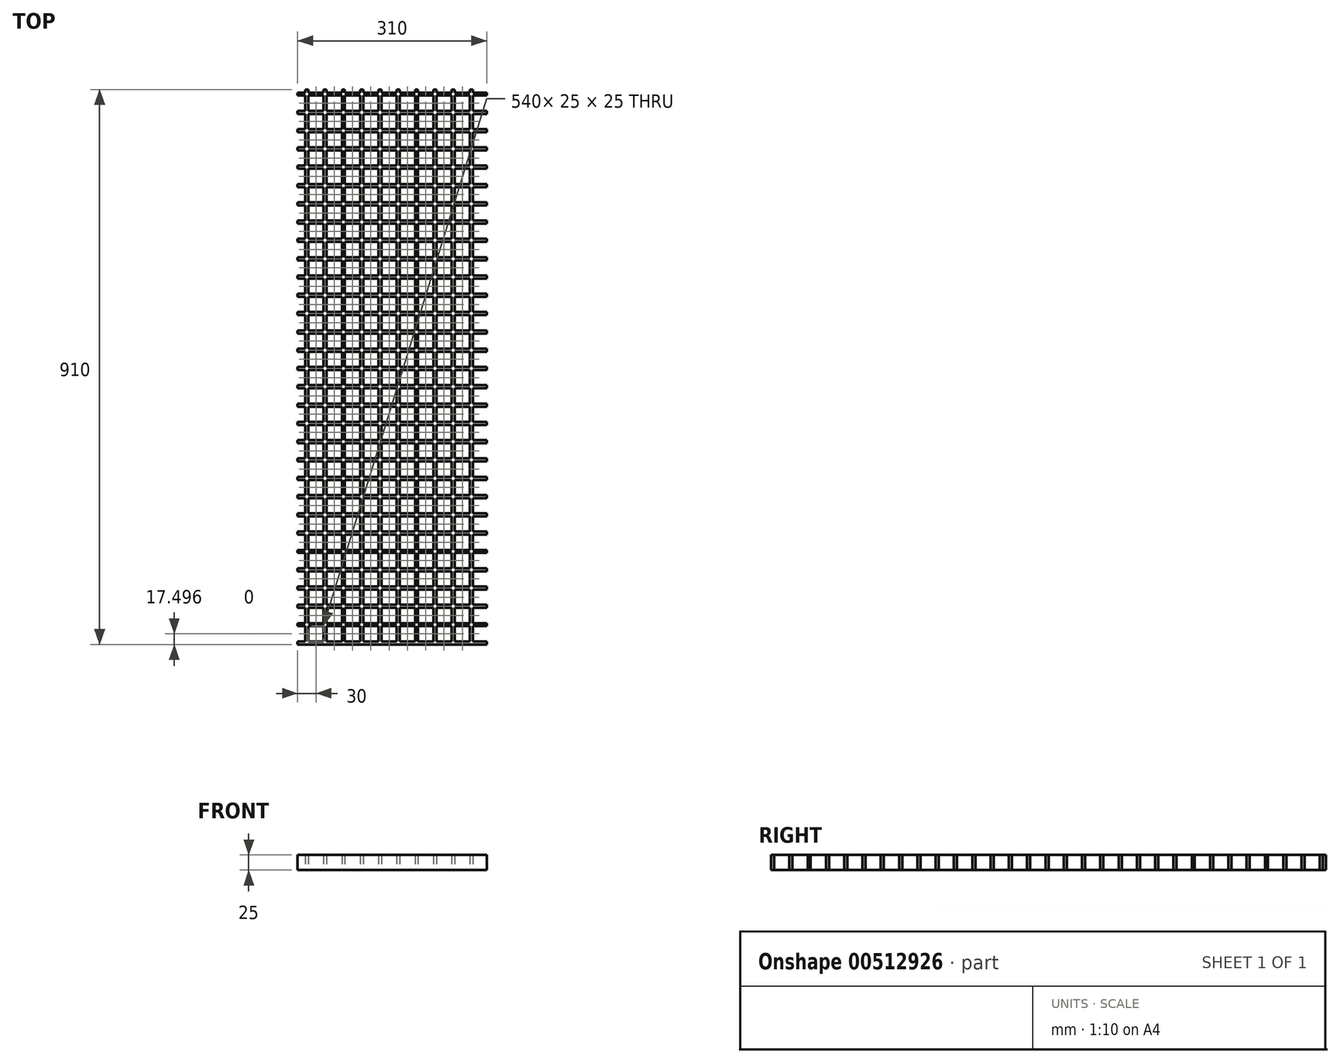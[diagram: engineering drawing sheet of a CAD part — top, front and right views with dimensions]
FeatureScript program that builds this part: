
annotation { "Feature Type Name" : "Feature", "Feature Type Description" : "" }
export const myFeature = defineFeature(function(context is Context, id is Id, definition is map)
    precondition{}
    {
        {
            var Q0;
            Q0=qCreatedBy(makeId("Top.planeOp"),FACE);
            var sketch = newSketch(context, id + "F0", { "sketchPlane" : qUnion([Q0])});
            skLineSegment(sketch, "E0.bottom", {"start": v(0, 20.3) * mm, "end": v(310, 20.3) * mm});
            skLineSegment(sketch, "E0.top", {"start": v(0, 930.3) * mm, "end": v(310, 930.3) * mm});
            skLineSegment(sketch, "E0.left", {"start": v(0, 20.3) * mm, "end": v(0, 930.3) * mm});
            skLineSegment(sketch, "E0.right", {"start": v(310, 20.3) * mm, "end": v(310, 930.3) * mm});
            skLineSegment(sketch, "E1.bottom", {"start": v(12.5, 25.3) * mm, "end": v(-12.5, 25.3) * mm});
            skLineSegment(sketch, "E1.top", {"start": v(12.5, 50.3) * mm, "end": v(-12.5, 50.3) * mm});
            skLineSegment(sketch, "E1.left", {"start": v(12.5, 25.3) * mm, "end": v(12.5, 50.3) * mm});
            skLineSegment(sketch, "E1.right", {"start": v(-12.5, 25.3) * mm, "end": v(-12.5, 50.3) * mm});
            skPoint(sketch, "E1.middle", {"position": v(0, 37.8) * mm});
            skLineSegment(sketch, "E2.0.1.0", {"start": v(12.5, 80.3) * mm, "end": v(-12.5, 80.3) * mm});
            skLineSegment(sketch, "E2.0.1.1", {"start": v(12.5, 55.3) * mm, "end": v(12.5, 80.3) * mm});
            skLineSegment(sketch, "E2.0.1.2", {"start": v(12.5, 55.3) * mm, "end": v(-12.5, 55.3) * mm});
            skLineSegment(sketch, "E2.0.1.3", {"start": v(-12.5, 55.3) * mm, "end": v(-12.5, 80.3) * mm});
            skLineSegment(sketch, "E2.0.2.0", {"start": v(12.5, 110.3) * mm, "end": v(-12.5, 110.3) * mm});
            skLineSegment(sketch, "E2.0.2.1", {"start": v(12.5, 85.3) * mm, "end": v(12.5, 110.3) * mm});
            skLineSegment(sketch, "E2.0.2.2", {"start": v(12.5, 85.3) * mm, "end": v(-12.5, 85.3) * mm});
            skLineSegment(sketch, "E2.0.2.3", {"start": v(-12.5, 85.3) * mm, "end": v(-12.5, 110.3) * mm});
            skLineSegment(sketch, "E2.0.3.0", {"start": v(12.5, 140.3) * mm, "end": v(-12.5, 140.3) * mm});
            skLineSegment(sketch, "E2.0.3.1", {"start": v(12.5, 115.3) * mm, "end": v(12.5, 140.3) * mm});
            skLineSegment(sketch, "E2.0.3.2", {"start": v(12.5, 115.3) * mm, "end": v(-12.5, 115.3) * mm});
            skLineSegment(sketch, "E2.0.3.3", {"start": v(-12.5, 115.3) * mm, "end": v(-12.5, 140.3) * mm});
            skLineSegment(sketch, "E2.0.4.0", {"start": v(12.5, 170.3) * mm, "end": v(-12.5, 170.3) * mm});
            skLineSegment(sketch, "E2.0.4.1", {"start": v(12.5, 145.3) * mm, "end": v(12.5, 170.3) * mm});
            skLineSegment(sketch, "E2.0.4.2", {"start": v(12.5, 145.3) * mm, "end": v(-12.5, 145.3) * mm});
            skLineSegment(sketch, "E2.0.4.3", {"start": v(-12.5, 145.3) * mm, "end": v(-12.5, 170.3) * mm});
            skLineSegment(sketch, "E2.0.5.0", {"start": v(12.5, 200.3) * mm, "end": v(-12.5, 200.3) * mm});
            skLineSegment(sketch, "E2.0.5.1", {"start": v(12.5, 175.3) * mm, "end": v(12.5, 200.3) * mm});
            skLineSegment(sketch, "E2.0.5.2", {"start": v(12.5, 175.3) * mm, "end": v(-12.5, 175.3) * mm});
            skLineSegment(sketch, "E2.0.5.3", {"start": v(-12.5, 175.3) * mm, "end": v(-12.5, 200.3) * mm});
            skLineSegment(sketch, "E2.0.6.0", {"start": v(12.5, 230.3) * mm, "end": v(-12.5, 230.3) * mm});
            skLineSegment(sketch, "E2.0.6.1", {"start": v(12.5, 205.3) * mm, "end": v(12.5, 230.3) * mm});
            skLineSegment(sketch, "E2.0.6.2", {"start": v(12.5, 205.3) * mm, "end": v(-12.5, 205.3) * mm});
            skLineSegment(sketch, "E2.0.6.3", {"start": v(-12.5, 205.3) * mm, "end": v(-12.5, 230.3) * mm});
            skLineSegment(sketch, "E2.0.7.0", {"start": v(12.5, 260.3) * mm, "end": v(-12.5, 260.3) * mm});
            skLineSegment(sketch, "E2.0.7.1", {"start": v(12.5, 235.3) * mm, "end": v(12.5, 260.3) * mm});
            skLineSegment(sketch, "E2.0.7.2", {"start": v(12.5, 235.3) * mm, "end": v(-12.5, 235.3) * mm});
            skLineSegment(sketch, "E2.0.7.3", {"start": v(-12.5, 235.3) * mm, "end": v(-12.5, 260.3) * mm});
            skLineSegment(sketch, "E2.0.8.0", {"start": v(12.5, 290.3) * mm, "end": v(-12.5, 290.3) * mm});
            skLineSegment(sketch, "E2.0.8.1", {"start": v(12.5, 265.3) * mm, "end": v(12.5, 290.3) * mm});
            skLineSegment(sketch, "E2.0.8.2", {"start": v(12.5, 265.3) * mm, "end": v(-12.5, 265.3) * mm});
            skLineSegment(sketch, "E2.0.8.3", {"start": v(-12.5, 265.3) * mm, "end": v(-12.5, 290.3) * mm});
            skLineSegment(sketch, "E2.0.9.0", {"start": v(12.5, 320.3) * mm, "end": v(-12.5, 320.3) * mm});
            skLineSegment(sketch, "E2.0.9.1", {"start": v(12.5, 295.3) * mm, "end": v(12.5, 320.3) * mm});
            skLineSegment(sketch, "E2.0.9.2", {"start": v(12.5, 295.3) * mm, "end": v(-12.5, 295.3) * mm});
            skLineSegment(sketch, "E2.0.9.3", {"start": v(-12.5, 295.3) * mm, "end": v(-12.5, 320.3) * mm});
            skLineSegment(sketch, "E2.0.10.0", {"start": v(12.5, 350.3) * mm, "end": v(-12.5, 350.3) * mm});
            skLineSegment(sketch, "E2.0.10.1", {"start": v(12.5, 325.3) * mm, "end": v(12.5, 350.3) * mm});
            skLineSegment(sketch, "E2.0.10.2", {"start": v(12.5, 325.3) * mm, "end": v(-12.5, 325.3) * mm});
            skLineSegment(sketch, "E2.0.10.3", {"start": v(-12.5, 325.3) * mm, "end": v(-12.5, 350.3) * mm});
            skLineSegment(sketch, "E2.0.11.0", {"start": v(12.5, 380.3) * mm, "end": v(-12.5, 380.3) * mm});
            skLineSegment(sketch, "E2.0.11.1", {"start": v(12.5, 355.3) * mm, "end": v(12.5, 380.3) * mm});
            skLineSegment(sketch, "E2.0.11.2", {"start": v(12.5, 355.3) * mm, "end": v(-12.5, 355.3) * mm});
            skLineSegment(sketch, "E2.0.11.3", {"start": v(-12.5, 355.3) * mm, "end": v(-12.5, 380.3) * mm});
            skLineSegment(sketch, "E2.0.12.0", {"start": v(12.5, 410.3) * mm, "end": v(-12.5, 410.3) * mm});
            skLineSegment(sketch, "E2.0.12.1", {"start": v(12.5, 385.3) * mm, "end": v(12.5, 410.3) * mm});
            skLineSegment(sketch, "E2.0.12.2", {"start": v(12.5, 385.3) * mm, "end": v(-12.5, 385.3) * mm});
            skLineSegment(sketch, "E2.0.12.3", {"start": v(-12.5, 385.3) * mm, "end": v(-12.5, 410.3) * mm});
            skLineSegment(sketch, "E2.0.13.0", {"start": v(12.5, 440.3) * mm, "end": v(-12.5, 440.3) * mm});
            skLineSegment(sketch, "E2.0.13.1", {"start": v(12.5, 415.3) * mm, "end": v(12.5, 440.3) * mm});
            skLineSegment(sketch, "E2.0.13.2", {"start": v(12.5, 415.3) * mm, "end": v(-12.5, 415.3) * mm});
            skLineSegment(sketch, "E2.0.13.3", {"start": v(-12.5, 415.3) * mm, "end": v(-12.5, 440.3) * mm});
            skLineSegment(sketch, "E2.0.14.0", {"start": v(12.5, 470.3) * mm, "end": v(-12.5, 470.3) * mm});
            skLineSegment(sketch, "E2.0.14.1", {"start": v(12.5, 445.3) * mm, "end": v(12.5, 470.3) * mm});
            skLineSegment(sketch, "E2.0.14.2", {"start": v(12.5, 445.3) * mm, "end": v(-12.5, 445.3) * mm});
            skLineSegment(sketch, "E2.0.14.3", {"start": v(-12.5, 445.3) * mm, "end": v(-12.5, 470.3) * mm});
            skLineSegment(sketch, "E2.0.15.0", {"start": v(12.5, 500.3) * mm, "end": v(-12.5, 500.3) * mm});
            skLineSegment(sketch, "E2.0.15.1", {"start": v(12.5, 475.3) * mm, "end": v(12.5, 500.3) * mm});
            skLineSegment(sketch, "E2.0.15.2", {"start": v(12.5, 475.3) * mm, "end": v(-12.5, 475.3) * mm});
            skLineSegment(sketch, "E2.0.15.3", {"start": v(-12.5, 475.3) * mm, "end": v(-12.5, 500.3) * mm});
            skLineSegment(sketch, "E2.0.16.0", {"start": v(12.5, 530.3) * mm, "end": v(-12.5, 530.3) * mm});
            skLineSegment(sketch, "E2.0.16.1", {"start": v(12.5, 505.3) * mm, "end": v(12.5, 530.3) * mm});
            skLineSegment(sketch, "E2.0.16.2", {"start": v(12.5, 505.3) * mm, "end": v(-12.5, 505.3) * mm});
            skLineSegment(sketch, "E2.0.16.3", {"start": v(-12.5, 505.3) * mm, "end": v(-12.5, 530.3) * mm});
            skLineSegment(sketch, "E2.0.17.0", {"start": v(12.5, 560.3) * mm, "end": v(-12.5, 560.3) * mm});
            skLineSegment(sketch, "E2.0.17.1", {"start": v(12.5, 535.3) * mm, "end": v(12.5, 560.3) * mm});
            skLineSegment(sketch, "E2.0.17.2", {"start": v(12.5, 535.3) * mm, "end": v(-12.5, 535.3) * mm});
            skLineSegment(sketch, "E2.0.17.3", {"start": v(-12.5, 535.3) * mm, "end": v(-12.5, 560.3) * mm});
            skLineSegment(sketch, "E2.0.18.0", {"start": v(12.5, 590.3) * mm, "end": v(-12.5, 590.3) * mm});
            skLineSegment(sketch, "E2.0.18.1", {"start": v(12.5, 565.3) * mm, "end": v(12.5, 590.3) * mm});
            skLineSegment(sketch, "E2.0.18.2", {"start": v(12.5, 565.3) * mm, "end": v(-12.5, 565.3) * mm});
            skLineSegment(sketch, "E2.0.18.3", {"start": v(-12.5, 565.3) * mm, "end": v(-12.5, 590.3) * mm});
            skLineSegment(sketch, "E2.0.19.0", {"start": v(12.5, 620.3) * mm, "end": v(-12.5, 620.3) * mm});
            skLineSegment(sketch, "E2.0.19.1", {"start": v(12.5, 595.3) * mm, "end": v(12.5, 620.3) * mm});
            skLineSegment(sketch, "E2.0.19.2", {"start": v(12.5, 595.3) * mm, "end": v(-12.5, 595.3) * mm});
            skLineSegment(sketch, "E2.0.19.3", {"start": v(-12.5, 595.3) * mm, "end": v(-12.5, 620.3) * mm});
            skLineSegment(sketch, "E2.0.20.0", {"start": v(12.5, 650.3) * mm, "end": v(-12.5, 650.3) * mm});
            skLineSegment(sketch, "E2.0.20.1", {"start": v(12.5, 625.3) * mm, "end": v(12.5, 650.3) * mm});
            skLineSegment(sketch, "E2.0.20.2", {"start": v(12.5, 625.3) * mm, "end": v(-12.5, 625.3) * mm});
            skLineSegment(sketch, "E2.0.20.3", {"start": v(-12.5, 625.3) * mm, "end": v(-12.5, 650.3) * mm});
            skLineSegment(sketch, "E2.0.21.0", {"start": v(12.5, 680.3) * mm, "end": v(-12.5, 680.3) * mm});
            skLineSegment(sketch, "E2.0.21.1", {"start": v(12.5, 655.3) * mm, "end": v(12.5, 680.3) * mm});
            skLineSegment(sketch, "E2.0.21.2", {"start": v(12.5, 655.3) * mm, "end": v(-12.5, 655.3) * mm});
            skLineSegment(sketch, "E2.0.21.3", {"start": v(-12.5, 655.3) * mm, "end": v(-12.5, 680.3) * mm});
            skLineSegment(sketch, "E2.0.22.0", {"start": v(12.5, 710.3) * mm, "end": v(-12.5, 710.3) * mm});
            skLineSegment(sketch, "E2.0.22.1", {"start": v(12.5, 685.3) * mm, "end": v(12.5, 710.3) * mm});
            skLineSegment(sketch, "E2.0.22.2", {"start": v(12.5, 685.3) * mm, "end": v(-12.5, 685.3) * mm});
            skLineSegment(sketch, "E2.0.22.3", {"start": v(-12.5, 685.3) * mm, "end": v(-12.5, 710.3) * mm});
            skLineSegment(sketch, "E2.0.23.0", {"start": v(12.5, 740.3) * mm, "end": v(-12.5, 740.3) * mm});
            skLineSegment(sketch, "E2.0.23.1", {"start": v(12.5, 715.3) * mm, "end": v(12.5, 740.3) * mm});
            skLineSegment(sketch, "E2.0.23.2", {"start": v(12.5, 715.3) * mm, "end": v(-12.5, 715.3) * mm});
            skLineSegment(sketch, "E2.0.23.3", {"start": v(-12.5, 715.3) * mm, "end": v(-12.5, 740.3) * mm});
            skLineSegment(sketch, "E2.0.24.0", {"start": v(12.5, 770.3) * mm, "end": v(-12.5, 770.3) * mm});
            skLineSegment(sketch, "E2.0.24.1", {"start": v(12.5, 745.3) * mm, "end": v(12.5, 770.3) * mm});
            skLineSegment(sketch, "E2.0.24.2", {"start": v(12.5, 745.3) * mm, "end": v(-12.5, 745.3) * mm});
            skLineSegment(sketch, "E2.0.24.3", {"start": v(-12.5, 745.3) * mm, "end": v(-12.5, 770.3) * mm});
            skLineSegment(sketch, "E2.0.25.0", {"start": v(12.5, 800.3) * mm, "end": v(-12.5, 800.3) * mm});
            skLineSegment(sketch, "E2.0.25.1", {"start": v(12.5, 775.3) * mm, "end": v(12.5, 800.3) * mm});
            skLineSegment(sketch, "E2.0.25.2", {"start": v(12.5, 775.3) * mm, "end": v(-12.5, 775.3) * mm});
            skLineSegment(sketch, "E2.0.25.3", {"start": v(-12.5, 775.3) * mm, "end": v(-12.5, 800.3) * mm});
            skLineSegment(sketch, "E2.0.26.0", {"start": v(12.5, 830.3) * mm, "end": v(-12.5, 830.3) * mm});
            skLineSegment(sketch, "E2.0.26.1", {"start": v(12.5, 805.3) * mm, "end": v(12.5, 830.3) * mm});
            skLineSegment(sketch, "E2.0.26.2", {"start": v(12.5, 805.3) * mm, "end": v(-12.5, 805.3) * mm});
            skLineSegment(sketch, "E2.0.26.3", {"start": v(-12.5, 805.3) * mm, "end": v(-12.5, 830.3) * mm});
            skLineSegment(sketch, "E2.0.27.0", {"start": v(12.5, 860.3) * mm, "end": v(-12.5, 860.3) * mm});
            skLineSegment(sketch, "E2.0.27.1", {"start": v(12.5, 835.3) * mm, "end": v(12.5, 860.3) * mm});
            skLineSegment(sketch, "E2.0.27.2", {"start": v(12.5, 835.3) * mm, "end": v(-12.5, 835.3) * mm});
            skLineSegment(sketch, "E2.0.27.3", {"start": v(-12.5, 835.3) * mm, "end": v(-12.5, 860.3) * mm});
            skLineSegment(sketch, "E2.0.28.0", {"start": v(12.5, 890.3) * mm, "end": v(-12.5, 890.3) * mm});
            skLineSegment(sketch, "E2.0.28.1", {"start": v(12.5, 865.3) * mm, "end": v(12.5, 890.3) * mm});
            skLineSegment(sketch, "E2.0.28.2", {"start": v(12.5, 865.3) * mm, "end": v(-12.5, 865.3) * mm});
            skLineSegment(sketch, "E2.0.28.3", {"start": v(-12.5, 865.3) * mm, "end": v(-12.5, 890.3) * mm});
            skLineSegment(sketch, "E2.0.29.0", {"start": v(12.5, 920.3) * mm, "end": v(-12.5, 920.3) * mm});
            skLineSegment(sketch, "E2.0.29.1", {"start": v(12.5, 895.3) * mm, "end": v(12.5, 920.3) * mm});
            skLineSegment(sketch, "E2.0.29.2", {"start": v(12.5, 895.3) * mm, "end": v(-12.5, 895.3) * mm});
            skLineSegment(sketch, "E2.0.29.3", {"start": v(-12.5, 895.3) * mm, "end": v(-12.5, 920.3) * mm});
            skLineSegment(sketch, "E2.0.30.0", {"start": v(12.5, 950.3) * mm, "end": v(-12.5, 950.3) * mm});
            skLineSegment(sketch, "E2.0.30.1", {"start": v(12.5, 925.3) * mm, "end": v(12.5, 950.3) * mm});
            skLineSegment(sketch, "E2.0.30.2", {"start": v(12.5, 925.3) * mm, "end": v(-12.5, 925.3) * mm});
            skLineSegment(sketch, "E2.0.30.3", {"start": v(-12.5, 925.3) * mm, "end": v(-12.5, 950.3) * mm});
            skLineSegment(sketch, "E2.1.0.0", {"start": v(42.5, 50.3) * mm, "end": v(17.5, 50.3) * mm});
            skLineSegment(sketch, "E2.1.0.1", {"start": v(42.5, 25.3) * mm, "end": v(42.5, 50.3) * mm});
            skLineSegment(sketch, "E2.1.0.2", {"start": v(42.5, 25.3) * mm, "end": v(17.5, 25.3) * mm});
            skLineSegment(sketch, "E2.1.0.3", {"start": v(17.5, 25.3) * mm, "end": v(17.5, 50.3) * mm});
            skLineSegment(sketch, "E2.1.1.0", {"start": v(42.5, 80.3) * mm, "end": v(17.5, 80.3) * mm});
            skLineSegment(sketch, "E2.1.1.1", {"start": v(42.5, 55.3) * mm, "end": v(42.5, 80.3) * mm});
            skLineSegment(sketch, "E2.1.1.2", {"start": v(42.5, 55.3) * mm, "end": v(17.5, 55.3) * mm});
            skLineSegment(sketch, "E2.1.1.3", {"start": v(17.5, 55.3) * mm, "end": v(17.5, 80.3) * mm});
            skLineSegment(sketch, "E2.1.2.0", {"start": v(42.5, 110.3) * mm, "end": v(17.5, 110.3) * mm});
            skLineSegment(sketch, "E2.1.2.1", {"start": v(42.5, 85.3) * mm, "end": v(42.5, 110.3) * mm});
            skLineSegment(sketch, "E2.1.2.2", {"start": v(42.5, 85.3) * mm, "end": v(17.5, 85.3) * mm});
            skLineSegment(sketch, "E2.1.2.3", {"start": v(17.5, 85.3) * mm, "end": v(17.5, 110.3) * mm});
            skLineSegment(sketch, "E2.1.3.0", {"start": v(42.5, 140.3) * mm, "end": v(17.5, 140.3) * mm});
            skLineSegment(sketch, "E2.1.3.1", {"start": v(42.5, 115.3) * mm, "end": v(42.5, 140.3) * mm});
            skLineSegment(sketch, "E2.1.3.2", {"start": v(42.5, 115.3) * mm, "end": v(17.5, 115.3) * mm});
            skLineSegment(sketch, "E2.1.3.3", {"start": v(17.5, 115.3) * mm, "end": v(17.5, 140.3) * mm});
            skLineSegment(sketch, "E2.1.4.0", {"start": v(42.5, 170.3) * mm, "end": v(17.5, 170.3) * mm});
            skLineSegment(sketch, "E2.1.4.1", {"start": v(42.5, 145.3) * mm, "end": v(42.5, 170.3) * mm});
            skLineSegment(sketch, "E2.1.4.2", {"start": v(42.5, 145.3) * mm, "end": v(17.5, 145.3) * mm});
            skLineSegment(sketch, "E2.1.4.3", {"start": v(17.5, 145.3) * mm, "end": v(17.5, 170.3) * mm});
            skLineSegment(sketch, "E2.1.5.0", {"start": v(42.5, 200.3) * mm, "end": v(17.5, 200.3) * mm});
            skLineSegment(sketch, "E2.1.5.1", {"start": v(42.5, 175.3) * mm, "end": v(42.5, 200.3) * mm});
            skLineSegment(sketch, "E2.1.5.2", {"start": v(42.5, 175.3) * mm, "end": v(17.5, 175.3) * mm});
            skLineSegment(sketch, "E2.1.5.3", {"start": v(17.5, 175.3) * mm, "end": v(17.5, 200.3) * mm});
            skLineSegment(sketch, "E2.1.6.0", {"start": v(42.5, 230.3) * mm, "end": v(17.5, 230.3) * mm});
            skLineSegment(sketch, "E2.1.6.1", {"start": v(42.5, 205.3) * mm, "end": v(42.5, 230.3) * mm});
            skLineSegment(sketch, "E2.1.6.2", {"start": v(42.5, 205.3) * mm, "end": v(17.5, 205.3) * mm});
            skLineSegment(sketch, "E2.1.6.3", {"start": v(17.5, 205.3) * mm, "end": v(17.5, 230.3) * mm});
            skLineSegment(sketch, "E2.1.7.0", {"start": v(42.5, 260.3) * mm, "end": v(17.5, 260.3) * mm});
            skLineSegment(sketch, "E2.1.7.1", {"start": v(42.5, 235.3) * mm, "end": v(42.5, 260.3) * mm});
            skLineSegment(sketch, "E2.1.7.2", {"start": v(42.5, 235.3) * mm, "end": v(17.5, 235.3) * mm});
            skLineSegment(sketch, "E2.1.7.3", {"start": v(17.5, 235.3) * mm, "end": v(17.5, 260.3) * mm});
            skLineSegment(sketch, "E2.1.8.0", {"start": v(42.5, 290.3) * mm, "end": v(17.5, 290.3) * mm});
            skLineSegment(sketch, "E2.1.8.1", {"start": v(42.5, 265.3) * mm, "end": v(42.5, 290.3) * mm});
            skLineSegment(sketch, "E2.1.8.2", {"start": v(42.5, 265.3) * mm, "end": v(17.5, 265.3) * mm});
            skLineSegment(sketch, "E2.1.8.3", {"start": v(17.5, 265.3) * mm, "end": v(17.5, 290.3) * mm});
            skLineSegment(sketch, "E2.1.9.0", {"start": v(42.5, 320.3) * mm, "end": v(17.5, 320.3) * mm});
            skLineSegment(sketch, "E2.1.9.1", {"start": v(42.5, 295.3) * mm, "end": v(42.5, 320.3) * mm});
            skLineSegment(sketch, "E2.1.9.2", {"start": v(42.5, 295.3) * mm, "end": v(17.5, 295.3) * mm});
            skLineSegment(sketch, "E2.1.9.3", {"start": v(17.5, 295.3) * mm, "end": v(17.5, 320.3) * mm});
            skLineSegment(sketch, "E2.1.10.0", {"start": v(42.5, 350.3) * mm, "end": v(17.5, 350.3) * mm});
            skLineSegment(sketch, "E2.1.10.1", {"start": v(42.5, 325.3) * mm, "end": v(42.5, 350.3) * mm});
            skLineSegment(sketch, "E2.1.10.2", {"start": v(42.5, 325.3) * mm, "end": v(17.5, 325.3) * mm});
            skLineSegment(sketch, "E2.1.10.3", {"start": v(17.5, 325.3) * mm, "end": v(17.5, 350.3) * mm});
            skLineSegment(sketch, "E2.1.11.0", {"start": v(42.5, 380.3) * mm, "end": v(17.5, 380.3) * mm});
            skLineSegment(sketch, "E2.1.11.1", {"start": v(42.5, 355.3) * mm, "end": v(42.5, 380.3) * mm});
            skLineSegment(sketch, "E2.1.11.2", {"start": v(42.5, 355.3) * mm, "end": v(17.5, 355.3) * mm});
            skLineSegment(sketch, "E2.1.11.3", {"start": v(17.5, 355.3) * mm, "end": v(17.5, 380.3) * mm});
            skLineSegment(sketch, "E2.1.12.0", {"start": v(42.5, 410.3) * mm, "end": v(17.5, 410.3) * mm});
            skLineSegment(sketch, "E2.1.12.1", {"start": v(42.5, 385.3) * mm, "end": v(42.5, 410.3) * mm});
            skLineSegment(sketch, "E2.1.12.2", {"start": v(42.5, 385.3) * mm, "end": v(17.5, 385.3) * mm});
            skLineSegment(sketch, "E2.1.12.3", {"start": v(17.5, 385.3) * mm, "end": v(17.5, 410.3) * mm});
            skLineSegment(sketch, "E2.1.13.0", {"start": v(42.5, 440.3) * mm, "end": v(17.5, 440.3) * mm});
            skLineSegment(sketch, "E2.1.13.1", {"start": v(42.5, 415.3) * mm, "end": v(42.5, 440.3) * mm});
            skLineSegment(sketch, "E2.1.13.2", {"start": v(42.5, 415.3) * mm, "end": v(17.5, 415.3) * mm});
            skLineSegment(sketch, "E2.1.13.3", {"start": v(17.5, 415.3) * mm, "end": v(17.5, 440.3) * mm});
            skLineSegment(sketch, "E2.1.14.0", {"start": v(42.5, 470.3) * mm, "end": v(17.5, 470.3) * mm});
            skLineSegment(sketch, "E2.1.14.1", {"start": v(42.5, 445.3) * mm, "end": v(42.5, 470.3) * mm});
            skLineSegment(sketch, "E2.1.14.2", {"start": v(42.5, 445.3) * mm, "end": v(17.5, 445.3) * mm});
            skLineSegment(sketch, "E2.1.14.3", {"start": v(17.5, 445.3) * mm, "end": v(17.5, 470.3) * mm});
            skLineSegment(sketch, "E2.1.15.0", {"start": v(42.5, 500.3) * mm, "end": v(17.5, 500.3) * mm});
            skLineSegment(sketch, "E2.1.15.1", {"start": v(42.5, 475.3) * mm, "end": v(42.5, 500.3) * mm});
            skLineSegment(sketch, "E2.1.15.2", {"start": v(42.5, 475.3) * mm, "end": v(17.5, 475.3) * mm});
            skLineSegment(sketch, "E2.1.15.3", {"start": v(17.5, 475.3) * mm, "end": v(17.5, 500.3) * mm});
            skLineSegment(sketch, "E2.1.16.0", {"start": v(42.5, 530.3) * mm, "end": v(17.5, 530.3) * mm});
            skLineSegment(sketch, "E2.1.16.1", {"start": v(42.5, 505.3) * mm, "end": v(42.5, 530.3) * mm});
            skLineSegment(sketch, "E2.1.16.2", {"start": v(42.5, 505.3) * mm, "end": v(17.5, 505.3) * mm});
            skLineSegment(sketch, "E2.1.16.3", {"start": v(17.5, 505.3) * mm, "end": v(17.5, 530.3) * mm});
            skLineSegment(sketch, "E2.1.17.0", {"start": v(42.5, 560.3) * mm, "end": v(17.5, 560.3) * mm});
            skLineSegment(sketch, "E2.1.17.1", {"start": v(42.5, 535.3) * mm, "end": v(42.5, 560.3) * mm});
            skLineSegment(sketch, "E2.1.17.2", {"start": v(42.5, 535.3) * mm, "end": v(17.5, 535.3) * mm});
            skLineSegment(sketch, "E2.1.17.3", {"start": v(17.5, 535.3) * mm, "end": v(17.5, 560.3) * mm});
            skLineSegment(sketch, "E2.1.18.0", {"start": v(42.5, 590.3) * mm, "end": v(17.5, 590.3) * mm});
            skLineSegment(sketch, "E2.1.18.1", {"start": v(42.5, 565.3) * mm, "end": v(42.5, 590.3) * mm});
            skLineSegment(sketch, "E2.1.18.2", {"start": v(42.5, 565.3) * mm, "end": v(17.5, 565.3) * mm});
            skLineSegment(sketch, "E2.1.18.3", {"start": v(17.5, 565.3) * mm, "end": v(17.5, 590.3) * mm});
            skLineSegment(sketch, "E2.1.19.0", {"start": v(42.5, 620.3) * mm, "end": v(17.5, 620.3) * mm});
            skLineSegment(sketch, "E2.1.19.1", {"start": v(42.5, 595.3) * mm, "end": v(42.5, 620.3) * mm});
            skLineSegment(sketch, "E2.1.19.2", {"start": v(42.5, 595.3) * mm, "end": v(17.5, 595.3) * mm});
            skLineSegment(sketch, "E2.1.19.3", {"start": v(17.5, 595.3) * mm, "end": v(17.5, 620.3) * mm});
            skLineSegment(sketch, "E2.1.20.0", {"start": v(42.5, 650.3) * mm, "end": v(17.5, 650.3) * mm});
            skLineSegment(sketch, "E2.1.20.1", {"start": v(42.5, 625.3) * mm, "end": v(42.5, 650.3) * mm});
            skLineSegment(sketch, "E2.1.20.2", {"start": v(42.5, 625.3) * mm, "end": v(17.5, 625.3) * mm});
            skLineSegment(sketch, "E2.1.20.3", {"start": v(17.5, 625.3) * mm, "end": v(17.5, 650.3) * mm});
            skLineSegment(sketch, "E2.1.21.0", {"start": v(42.5, 680.3) * mm, "end": v(17.5, 680.3) * mm});
            skLineSegment(sketch, "E2.1.21.1", {"start": v(42.5, 655.3) * mm, "end": v(42.5, 680.3) * mm});
            skLineSegment(sketch, "E2.1.21.2", {"start": v(42.5, 655.3) * mm, "end": v(17.5, 655.3) * mm});
            skLineSegment(sketch, "E2.1.21.3", {"start": v(17.5, 655.3) * mm, "end": v(17.5, 680.3) * mm});
            skLineSegment(sketch, "E2.1.22.0", {"start": v(42.5, 710.3) * mm, "end": v(17.5, 710.3) * mm});
            skLineSegment(sketch, "E2.1.22.1", {"start": v(42.5, 685.3) * mm, "end": v(42.5, 710.3) * mm});
            skLineSegment(sketch, "E2.1.22.2", {"start": v(42.5, 685.3) * mm, "end": v(17.5, 685.3) * mm});
            skLineSegment(sketch, "E2.1.22.3", {"start": v(17.5, 685.3) * mm, "end": v(17.5, 710.3) * mm});
            skLineSegment(sketch, "E2.1.23.0", {"start": v(42.5, 740.3) * mm, "end": v(17.5, 740.3) * mm});
            skLineSegment(sketch, "E2.1.23.1", {"start": v(42.5, 715.3) * mm, "end": v(42.5, 740.3) * mm});
            skLineSegment(sketch, "E2.1.23.2", {"start": v(42.5, 715.3) * mm, "end": v(17.5, 715.3) * mm});
            skLineSegment(sketch, "E2.1.23.3", {"start": v(17.5, 715.3) * mm, "end": v(17.5, 740.3) * mm});
            skLineSegment(sketch, "E2.1.24.0", {"start": v(42.5, 770.3) * mm, "end": v(17.5, 770.3) * mm});
            skLineSegment(sketch, "E2.1.24.1", {"start": v(42.5, 745.3) * mm, "end": v(42.5, 770.3) * mm});
            skLineSegment(sketch, "E2.1.24.2", {"start": v(42.5, 745.3) * mm, "end": v(17.5, 745.3) * mm});
            skLineSegment(sketch, "E2.1.24.3", {"start": v(17.5, 745.3) * mm, "end": v(17.5, 770.3) * mm});
            skLineSegment(sketch, "E2.1.25.0", {"start": v(42.5, 800.3) * mm, "end": v(17.5, 800.3) * mm});
            skLineSegment(sketch, "E2.1.25.1", {"start": v(42.5, 775.3) * mm, "end": v(42.5, 800.3) * mm});
            skLineSegment(sketch, "E2.1.25.2", {"start": v(42.5, 775.3) * mm, "end": v(17.5, 775.3) * mm});
            skLineSegment(sketch, "E2.1.25.3", {"start": v(17.5, 775.3) * mm, "end": v(17.5, 800.3) * mm});
            skLineSegment(sketch, "E2.1.26.0", {"start": v(42.5, 830.3) * mm, "end": v(17.5, 830.3) * mm});
            skLineSegment(sketch, "E2.1.26.1", {"start": v(42.5, 805.3) * mm, "end": v(42.5, 830.3) * mm});
            skLineSegment(sketch, "E2.1.26.2", {"start": v(42.5, 805.3) * mm, "end": v(17.5, 805.3) * mm});
            skLineSegment(sketch, "E2.1.26.3", {"start": v(17.5, 805.3) * mm, "end": v(17.5, 830.3) * mm});
            skLineSegment(sketch, "E2.1.27.0", {"start": v(42.5, 860.3) * mm, "end": v(17.5, 860.3) * mm});
            skLineSegment(sketch, "E2.1.27.1", {"start": v(42.5, 835.3) * mm, "end": v(42.5, 860.3) * mm});
            skLineSegment(sketch, "E2.1.27.2", {"start": v(42.5, 835.3) * mm, "end": v(17.5, 835.3) * mm});
            skLineSegment(sketch, "E2.1.27.3", {"start": v(17.5, 835.3) * mm, "end": v(17.5, 860.3) * mm});
            skLineSegment(sketch, "E2.1.28.0", {"start": v(42.5, 890.3) * mm, "end": v(17.5, 890.3) * mm});
            skLineSegment(sketch, "E2.1.28.1", {"start": v(42.5, 865.3) * mm, "end": v(42.5, 890.3) * mm});
            skLineSegment(sketch, "E2.1.28.2", {"start": v(42.5, 865.3) * mm, "end": v(17.5, 865.3) * mm});
            skLineSegment(sketch, "E2.1.28.3", {"start": v(17.5, 865.3) * mm, "end": v(17.5, 890.3) * mm});
            skLineSegment(sketch, "E2.1.29.0", {"start": v(42.5, 920.3) * mm, "end": v(17.5, 920.3) * mm});
            skLineSegment(sketch, "E2.1.29.1", {"start": v(42.5, 895.3) * mm, "end": v(42.5, 920.3) * mm});
            skLineSegment(sketch, "E2.1.29.2", {"start": v(42.5, 895.3) * mm, "end": v(17.5, 895.3) * mm});
            skLineSegment(sketch, "E2.1.29.3", {"start": v(17.5, 895.3) * mm, "end": v(17.5, 920.3) * mm});
            skLineSegment(sketch, "E2.1.30.0", {"start": v(42.5, 950.3) * mm, "end": v(17.5, 950.3) * mm});
            skLineSegment(sketch, "E2.1.30.1", {"start": v(42.5, 925.3) * mm, "end": v(42.5, 950.3) * mm});
            skLineSegment(sketch, "E2.1.30.2", {"start": v(42.5, 925.3) * mm, "end": v(17.5, 925.3) * mm});
            skLineSegment(sketch, "E2.1.30.3", {"start": v(17.5, 925.3) * mm, "end": v(17.5, 950.3) * mm});
            skLineSegment(sketch, "E2.2.0.0", {"start": v(72.5, 50.3) * mm, "end": v(47.5, 50.3) * mm});
            skLineSegment(sketch, "E2.2.0.1", {"start": v(72.5, 25.3) * mm, "end": v(72.5, 50.3) * mm});
            skLineSegment(sketch, "E2.2.0.2", {"start": v(72.5, 25.3) * mm, "end": v(47.5, 25.3) * mm});
            skLineSegment(sketch, "E2.2.0.3", {"start": v(47.5, 25.3) * mm, "end": v(47.5, 50.3) * mm});
            skLineSegment(sketch, "E2.2.1.0", {"start": v(72.5, 80.3) * mm, "end": v(47.5, 80.3) * mm});
            skLineSegment(sketch, "E2.2.1.1", {"start": v(72.5, 55.3) * mm, "end": v(72.5, 80.3) * mm});
            skLineSegment(sketch, "E2.2.1.2", {"start": v(72.5, 55.3) * mm, "end": v(47.5, 55.3) * mm});
            skLineSegment(sketch, "E2.2.1.3", {"start": v(47.5, 55.3) * mm, "end": v(47.5, 80.3) * mm});
            skLineSegment(sketch, "E2.2.2.0", {"start": v(72.5, 110.3) * mm, "end": v(47.5, 110.3) * mm});
            skLineSegment(sketch, "E2.2.2.1", {"start": v(72.5, 85.3) * mm, "end": v(72.5, 110.3) * mm});
            skLineSegment(sketch, "E2.2.2.2", {"start": v(72.5, 85.3) * mm, "end": v(47.5, 85.3) * mm});
            skLineSegment(sketch, "E2.2.2.3", {"start": v(47.5, 85.3) * mm, "end": v(47.5, 110.3) * mm});
            skLineSegment(sketch, "E2.2.3.0", {"start": v(72.5, 140.3) * mm, "end": v(47.5, 140.3) * mm});
            skLineSegment(sketch, "E2.2.3.1", {"start": v(72.5, 115.3) * mm, "end": v(72.5, 140.3) * mm});
            skLineSegment(sketch, "E2.2.3.2", {"start": v(72.5, 115.3) * mm, "end": v(47.5, 115.3) * mm});
            skLineSegment(sketch, "E2.2.3.3", {"start": v(47.5, 115.3) * mm, "end": v(47.5, 140.3) * mm});
            skLineSegment(sketch, "E2.2.4.0", {"start": v(72.5, 170.3) * mm, "end": v(47.5, 170.3) * mm});
            skLineSegment(sketch, "E2.2.4.1", {"start": v(72.5, 145.3) * mm, "end": v(72.5, 170.3) * mm});
            skLineSegment(sketch, "E2.2.4.2", {"start": v(72.5, 145.3) * mm, "end": v(47.5, 145.3) * mm});
            skLineSegment(sketch, "E2.2.4.3", {"start": v(47.5, 145.3) * mm, "end": v(47.5, 170.3) * mm});
            skLineSegment(sketch, "E2.2.5.0", {"start": v(72.5, 200.3) * mm, "end": v(47.5, 200.3) * mm});
            skLineSegment(sketch, "E2.2.5.1", {"start": v(72.5, 175.3) * mm, "end": v(72.5, 200.3) * mm});
            skLineSegment(sketch, "E2.2.5.2", {"start": v(72.5, 175.3) * mm, "end": v(47.5, 175.3) * mm});
            skLineSegment(sketch, "E2.2.5.3", {"start": v(47.5, 175.3) * mm, "end": v(47.5, 200.3) * mm});
            skLineSegment(sketch, "E2.2.6.0", {"start": v(72.5, 230.3) * mm, "end": v(47.5, 230.3) * mm});
            skLineSegment(sketch, "E2.2.6.1", {"start": v(72.5, 205.3) * mm, "end": v(72.5, 230.3) * mm});
            skLineSegment(sketch, "E2.2.6.2", {"start": v(72.5, 205.3) * mm, "end": v(47.5, 205.3) * mm});
            skLineSegment(sketch, "E2.2.6.3", {"start": v(47.5, 205.3) * mm, "end": v(47.5, 230.3) * mm});
            skLineSegment(sketch, "E2.2.7.0", {"start": v(72.5, 260.3) * mm, "end": v(47.5, 260.3) * mm});
            skLineSegment(sketch, "E2.2.7.1", {"start": v(72.5, 235.3) * mm, "end": v(72.5, 260.3) * mm});
            skLineSegment(sketch, "E2.2.7.2", {"start": v(72.5, 235.3) * mm, "end": v(47.5, 235.3) * mm});
            skLineSegment(sketch, "E2.2.7.3", {"start": v(47.5, 235.3) * mm, "end": v(47.5, 260.3) * mm});
            skLineSegment(sketch, "E2.2.8.0", {"start": v(72.5, 290.3) * mm, "end": v(47.5, 290.3) * mm});
            skLineSegment(sketch, "E2.2.8.1", {"start": v(72.5, 265.3) * mm, "end": v(72.5, 290.3) * mm});
            skLineSegment(sketch, "E2.2.8.2", {"start": v(72.5, 265.3) * mm, "end": v(47.5, 265.3) * mm});
            skLineSegment(sketch, "E2.2.8.3", {"start": v(47.5, 265.3) * mm, "end": v(47.5, 290.3) * mm});
            skLineSegment(sketch, "E2.2.9.0", {"start": v(72.5, 320.3) * mm, "end": v(47.5, 320.3) * mm});
            skLineSegment(sketch, "E2.2.9.1", {"start": v(72.5, 295.3) * mm, "end": v(72.5, 320.3) * mm});
            skLineSegment(sketch, "E2.2.9.2", {"start": v(72.5, 295.3) * mm, "end": v(47.5, 295.3) * mm});
            skLineSegment(sketch, "E2.2.9.3", {"start": v(47.5, 295.3) * mm, "end": v(47.5, 320.3) * mm});
            skLineSegment(sketch, "E2.2.10.0", {"start": v(72.5, 350.3) * mm, "end": v(47.5, 350.3) * mm});
            skLineSegment(sketch, "E2.2.10.1", {"start": v(72.5, 325.3) * mm, "end": v(72.5, 350.3) * mm});
            skLineSegment(sketch, "E2.2.10.2", {"start": v(72.5, 325.3) * mm, "end": v(47.5, 325.3) * mm});
            skLineSegment(sketch, "E2.2.10.3", {"start": v(47.5, 325.3) * mm, "end": v(47.5, 350.3) * mm});
            skLineSegment(sketch, "E2.2.11.0", {"start": v(72.5, 380.3) * mm, "end": v(47.5, 380.3) * mm});
            skLineSegment(sketch, "E2.2.11.1", {"start": v(72.5, 355.3) * mm, "end": v(72.5, 380.3) * mm});
            skLineSegment(sketch, "E2.2.11.2", {"start": v(72.5, 355.3) * mm, "end": v(47.5, 355.3) * mm});
            skLineSegment(sketch, "E2.2.11.3", {"start": v(47.5, 355.3) * mm, "end": v(47.5, 380.3) * mm});
            skLineSegment(sketch, "E2.2.12.0", {"start": v(72.5, 410.3) * mm, "end": v(47.5, 410.3) * mm});
            skLineSegment(sketch, "E2.2.12.1", {"start": v(72.5, 385.3) * mm, "end": v(72.5, 410.3) * mm});
            skLineSegment(sketch, "E2.2.12.2", {"start": v(72.5, 385.3) * mm, "end": v(47.5, 385.3) * mm});
            skLineSegment(sketch, "E2.2.12.3", {"start": v(47.5, 385.3) * mm, "end": v(47.5, 410.3) * mm});
            skLineSegment(sketch, "E2.2.13.0", {"start": v(72.5, 440.3) * mm, "end": v(47.5, 440.3) * mm});
            skLineSegment(sketch, "E2.2.13.1", {"start": v(72.5, 415.3) * mm, "end": v(72.5, 440.3) * mm});
            skLineSegment(sketch, "E2.2.13.2", {"start": v(72.5, 415.3) * mm, "end": v(47.5, 415.3) * mm});
            skLineSegment(sketch, "E2.2.13.3", {"start": v(47.5, 415.3) * mm, "end": v(47.5, 440.3) * mm});
            skLineSegment(sketch, "E2.2.14.0", {"start": v(72.5, 470.3) * mm, "end": v(47.5, 470.3) * mm});
            skLineSegment(sketch, "E2.2.14.1", {"start": v(72.5, 445.3) * mm, "end": v(72.5, 470.3) * mm});
            skLineSegment(sketch, "E2.2.14.2", {"start": v(72.5, 445.3) * mm, "end": v(47.5, 445.3) * mm});
            skLineSegment(sketch, "E2.2.14.3", {"start": v(47.5, 445.3) * mm, "end": v(47.5, 470.3) * mm});
            skLineSegment(sketch, "E2.2.15.0", {"start": v(72.5, 500.3) * mm, "end": v(47.5, 500.3) * mm});
            skLineSegment(sketch, "E2.2.15.1", {"start": v(72.5, 475.3) * mm, "end": v(72.5, 500.3) * mm});
            skLineSegment(sketch, "E2.2.15.2", {"start": v(72.5, 475.3) * mm, "end": v(47.5, 475.3) * mm});
            skLineSegment(sketch, "E2.2.15.3", {"start": v(47.5, 475.3) * mm, "end": v(47.5, 500.3) * mm});
            skLineSegment(sketch, "E2.2.16.0", {"start": v(72.5, 530.3) * mm, "end": v(47.5, 530.3) * mm});
            skLineSegment(sketch, "E2.2.16.1", {"start": v(72.5, 505.3) * mm, "end": v(72.5, 530.3) * mm});
            skLineSegment(sketch, "E2.2.16.2", {"start": v(72.5, 505.3) * mm, "end": v(47.5, 505.3) * mm});
            skLineSegment(sketch, "E2.2.16.3", {"start": v(47.5, 505.3) * mm, "end": v(47.5, 530.3) * mm});
            skLineSegment(sketch, "E2.2.17.0", {"start": v(72.5, 560.3) * mm, "end": v(47.5, 560.3) * mm});
            skLineSegment(sketch, "E2.2.17.1", {"start": v(72.5, 535.3) * mm, "end": v(72.5, 560.3) * mm});
            skLineSegment(sketch, "E2.2.17.2", {"start": v(72.5, 535.3) * mm, "end": v(47.5, 535.3) * mm});
            skLineSegment(sketch, "E2.2.17.3", {"start": v(47.5, 535.3) * mm, "end": v(47.5, 560.3) * mm});
            skLineSegment(sketch, "E2.2.18.0", {"start": v(72.5, 590.3) * mm, "end": v(47.5, 590.3) * mm});
            skLineSegment(sketch, "E2.2.18.1", {"start": v(72.5, 565.3) * mm, "end": v(72.5, 590.3) * mm});
            skLineSegment(sketch, "E2.2.18.2", {"start": v(72.5, 565.3) * mm, "end": v(47.5, 565.3) * mm});
            skLineSegment(sketch, "E2.2.18.3", {"start": v(47.5, 565.3) * mm, "end": v(47.5, 590.3) * mm});
            skLineSegment(sketch, "E2.2.19.0", {"start": v(72.5, 620.3) * mm, "end": v(47.5, 620.3) * mm});
            skLineSegment(sketch, "E2.2.19.1", {"start": v(72.5, 595.3) * mm, "end": v(72.5, 620.3) * mm});
            skLineSegment(sketch, "E2.2.19.2", {"start": v(72.5, 595.3) * mm, "end": v(47.5, 595.3) * mm});
            skLineSegment(sketch, "E2.2.19.3", {"start": v(47.5, 595.3) * mm, "end": v(47.5, 620.3) * mm});
            skLineSegment(sketch, "E2.2.20.0", {"start": v(72.5, 650.3) * mm, "end": v(47.5, 650.3) * mm});
            skLineSegment(sketch, "E2.2.20.1", {"start": v(72.5, 625.3) * mm, "end": v(72.5, 650.3) * mm});
            skLineSegment(sketch, "E2.2.20.2", {"start": v(72.5, 625.3) * mm, "end": v(47.5, 625.3) * mm});
            skLineSegment(sketch, "E2.2.20.3", {"start": v(47.5, 625.3) * mm, "end": v(47.5, 650.3) * mm});
            skLineSegment(sketch, "E2.2.21.0", {"start": v(72.5, 680.3) * mm, "end": v(47.5, 680.3) * mm});
            skLineSegment(sketch, "E2.2.21.1", {"start": v(72.5, 655.3) * mm, "end": v(72.5, 680.3) * mm});
            skLineSegment(sketch, "E2.2.21.2", {"start": v(72.5, 655.3) * mm, "end": v(47.5, 655.3) * mm});
            skLineSegment(sketch, "E2.2.21.3", {"start": v(47.5, 655.3) * mm, "end": v(47.5, 680.3) * mm});
            skLineSegment(sketch, "E2.2.22.0", {"start": v(72.5, 710.3) * mm, "end": v(47.5, 710.3) * mm});
            skLineSegment(sketch, "E2.2.22.1", {"start": v(72.5, 685.3) * mm, "end": v(72.5, 710.3) * mm});
            skLineSegment(sketch, "E2.2.22.2", {"start": v(72.5, 685.3) * mm, "end": v(47.5, 685.3) * mm});
            skLineSegment(sketch, "E2.2.22.3", {"start": v(47.5, 685.3) * mm, "end": v(47.5, 710.3) * mm});
            skLineSegment(sketch, "E2.2.23.0", {"start": v(72.5, 740.3) * mm, "end": v(47.5, 740.3) * mm});
            skLineSegment(sketch, "E2.2.23.1", {"start": v(72.5, 715.3) * mm, "end": v(72.5, 740.3) * mm});
            skLineSegment(sketch, "E2.2.23.2", {"start": v(72.5, 715.3) * mm, "end": v(47.5, 715.3) * mm});
            skLineSegment(sketch, "E2.2.23.3", {"start": v(47.5, 715.3) * mm, "end": v(47.5, 740.3) * mm});
            skLineSegment(sketch, "E2.2.24.0", {"start": v(72.5, 770.3) * mm, "end": v(47.5, 770.3) * mm});
            skLineSegment(sketch, "E2.2.24.1", {"start": v(72.5, 745.3) * mm, "end": v(72.5, 770.3) * mm});
            skLineSegment(sketch, "E2.2.24.2", {"start": v(72.5, 745.3) * mm, "end": v(47.5, 745.3) * mm});
            skLineSegment(sketch, "E2.2.24.3", {"start": v(47.5, 745.3) * mm, "end": v(47.5, 770.3) * mm});
            skLineSegment(sketch, "E2.2.25.0", {"start": v(72.5, 800.3) * mm, "end": v(47.5, 800.3) * mm});
            skLineSegment(sketch, "E2.2.25.1", {"start": v(72.5, 775.3) * mm, "end": v(72.5, 800.3) * mm});
            skLineSegment(sketch, "E2.2.25.2", {"start": v(72.5, 775.3) * mm, "end": v(47.5, 775.3) * mm});
            skLineSegment(sketch, "E2.2.25.3", {"start": v(47.5, 775.3) * mm, "end": v(47.5, 800.3) * mm});
            skLineSegment(sketch, "E2.2.26.0", {"start": v(72.5, 830.3) * mm, "end": v(47.5, 830.3) * mm});
            skLineSegment(sketch, "E2.2.26.1", {"start": v(72.5, 805.3) * mm, "end": v(72.5, 830.3) * mm});
            skLineSegment(sketch, "E2.2.26.2", {"start": v(72.5, 805.3) * mm, "end": v(47.5, 805.3) * mm});
            skLineSegment(sketch, "E2.2.26.3", {"start": v(47.5, 805.3) * mm, "end": v(47.5, 830.3) * mm});
            skLineSegment(sketch, "E2.2.27.0", {"start": v(72.5, 860.3) * mm, "end": v(47.5, 860.3) * mm});
            skLineSegment(sketch, "E2.2.27.1", {"start": v(72.5, 835.3) * mm, "end": v(72.5, 860.3) * mm});
            skLineSegment(sketch, "E2.2.27.2", {"start": v(72.5, 835.3) * mm, "end": v(47.5, 835.3) * mm});
            skLineSegment(sketch, "E2.2.27.3", {"start": v(47.5, 835.3) * mm, "end": v(47.5, 860.3) * mm});
            skLineSegment(sketch, "E2.2.28.0", {"start": v(72.5, 890.3) * mm, "end": v(47.5, 890.3) * mm});
            skLineSegment(sketch, "E2.2.28.1", {"start": v(72.5, 865.3) * mm, "end": v(72.5, 890.3) * mm});
            skLineSegment(sketch, "E2.2.28.2", {"start": v(72.5, 865.3) * mm, "end": v(47.5, 865.3) * mm});
            skLineSegment(sketch, "E2.2.28.3", {"start": v(47.5, 865.3) * mm, "end": v(47.5, 890.3) * mm});
            skLineSegment(sketch, "E2.2.29.0", {"start": v(72.5, 920.3) * mm, "end": v(47.5, 920.3) * mm});
            skLineSegment(sketch, "E2.2.29.1", {"start": v(72.5, 895.3) * mm, "end": v(72.5, 920.3) * mm});
            skLineSegment(sketch, "E2.2.29.2", {"start": v(72.5, 895.3) * mm, "end": v(47.5, 895.3) * mm});
            skLineSegment(sketch, "E2.2.29.3", {"start": v(47.5, 895.3) * mm, "end": v(47.5, 920.3) * mm});
            skLineSegment(sketch, "E2.2.30.0", {"start": v(72.5, 950.3) * mm, "end": v(47.5, 950.3) * mm});
            skLineSegment(sketch, "E2.2.30.1", {"start": v(72.5, 925.3) * mm, "end": v(72.5, 950.3) * mm});
            skLineSegment(sketch, "E2.2.30.2", {"start": v(72.5, 925.3) * mm, "end": v(47.5, 925.3) * mm});
            skLineSegment(sketch, "E2.2.30.3", {"start": v(47.5, 925.3) * mm, "end": v(47.5, 950.3) * mm});
            skLineSegment(sketch, "E2.3.0.0", {"start": v(102.5, 50.3) * mm, "end": v(77.5, 50.3) * mm});
            skLineSegment(sketch, "E2.3.0.1", {"start": v(102.5, 25.3) * mm, "end": v(102.5, 50.3) * mm});
            skLineSegment(sketch, "E2.3.0.2", {"start": v(102.5, 25.3) * mm, "end": v(77.5, 25.3) * mm});
            skLineSegment(sketch, "E2.3.0.3", {"start": v(77.5, 25.3) * mm, "end": v(77.5, 50.3) * mm});
            skLineSegment(sketch, "E2.3.1.0", {"start": v(102.5, 80.3) * mm, "end": v(77.5, 80.3) * mm});
            skLineSegment(sketch, "E2.3.1.1", {"start": v(102.5, 55.3) * mm, "end": v(102.5, 80.3) * mm});
            skLineSegment(sketch, "E2.3.1.2", {"start": v(102.5, 55.3) * mm, "end": v(77.5, 55.3) * mm});
            skLineSegment(sketch, "E2.3.1.3", {"start": v(77.5, 55.3) * mm, "end": v(77.5, 80.3) * mm});
            skLineSegment(sketch, "E2.3.2.0", {"start": v(102.5, 110.3) * mm, "end": v(77.5, 110.3) * mm});
            skLineSegment(sketch, "E2.3.2.1", {"start": v(102.5, 85.3) * mm, "end": v(102.5, 110.3) * mm});
            skLineSegment(sketch, "E2.3.2.2", {"start": v(102.5, 85.3) * mm, "end": v(77.5, 85.3) * mm});
            skLineSegment(sketch, "E2.3.2.3", {"start": v(77.5, 85.3) * mm, "end": v(77.5, 110.3) * mm});
            skLineSegment(sketch, "E2.3.3.0", {"start": v(102.5, 140.3) * mm, "end": v(77.5, 140.3) * mm});
            skLineSegment(sketch, "E2.3.3.1", {"start": v(102.5, 115.3) * mm, "end": v(102.5, 140.3) * mm});
            skLineSegment(sketch, "E2.3.3.2", {"start": v(102.5, 115.3) * mm, "end": v(77.5, 115.3) * mm});
            skLineSegment(sketch, "E2.3.3.3", {"start": v(77.5, 115.3) * mm, "end": v(77.5, 140.3) * mm});
            skLineSegment(sketch, "E2.3.4.0", {"start": v(102.5, 170.3) * mm, "end": v(77.5, 170.3) * mm});
            skLineSegment(sketch, "E2.3.4.1", {"start": v(102.5, 145.3) * mm, "end": v(102.5, 170.3) * mm});
            skLineSegment(sketch, "E2.3.4.2", {"start": v(102.5, 145.3) * mm, "end": v(77.5, 145.3) * mm});
            skLineSegment(sketch, "E2.3.4.3", {"start": v(77.5, 145.3) * mm, "end": v(77.5, 170.3) * mm});
            skLineSegment(sketch, "E2.3.5.0", {"start": v(102.5, 200.3) * mm, "end": v(77.5, 200.3) * mm});
            skLineSegment(sketch, "E2.3.5.1", {"start": v(102.5, 175.3) * mm, "end": v(102.5, 200.3) * mm});
            skLineSegment(sketch, "E2.3.5.2", {"start": v(102.5, 175.3) * mm, "end": v(77.5, 175.3) * mm});
            skLineSegment(sketch, "E2.3.5.3", {"start": v(77.5, 175.3) * mm, "end": v(77.5, 200.3) * mm});
            skLineSegment(sketch, "E2.3.6.0", {"start": v(102.5, 230.3) * mm, "end": v(77.5, 230.3) * mm});
            skLineSegment(sketch, "E2.3.6.1", {"start": v(102.5, 205.3) * mm, "end": v(102.5, 230.3) * mm});
            skLineSegment(sketch, "E2.3.6.2", {"start": v(102.5, 205.3) * mm, "end": v(77.5, 205.3) * mm});
            skLineSegment(sketch, "E2.3.6.3", {"start": v(77.5, 205.3) * mm, "end": v(77.5, 230.3) * mm});
            skLineSegment(sketch, "E2.3.7.0", {"start": v(102.5, 260.3) * mm, "end": v(77.5, 260.3) * mm});
            skLineSegment(sketch, "E2.3.7.1", {"start": v(102.5, 235.3) * mm, "end": v(102.5, 260.3) * mm});
            skLineSegment(sketch, "E2.3.7.2", {"start": v(102.5, 235.3) * mm, "end": v(77.5, 235.3) * mm});
            skLineSegment(sketch, "E2.3.7.3", {"start": v(77.5, 235.3) * mm, "end": v(77.5, 260.3) * mm});
            skLineSegment(sketch, "E2.3.8.0", {"start": v(102.5, 290.3) * mm, "end": v(77.5, 290.3) * mm});
            skLineSegment(sketch, "E2.3.8.1", {"start": v(102.5, 265.3) * mm, "end": v(102.5, 290.3) * mm});
            skLineSegment(sketch, "E2.3.8.2", {"start": v(102.5, 265.3) * mm, "end": v(77.5, 265.3) * mm});
            skLineSegment(sketch, "E2.3.8.3", {"start": v(77.5, 265.3) * mm, "end": v(77.5, 290.3) * mm});
            skLineSegment(sketch, "E2.3.9.0", {"start": v(102.5, 320.3) * mm, "end": v(77.5, 320.3) * mm});
            skLineSegment(sketch, "E2.3.9.1", {"start": v(102.5, 295.3) * mm, "end": v(102.5, 320.3) * mm});
            skLineSegment(sketch, "E2.3.9.2", {"start": v(102.5, 295.3) * mm, "end": v(77.5, 295.3) * mm});
            skLineSegment(sketch, "E2.3.9.3", {"start": v(77.5, 295.3) * mm, "end": v(77.5, 320.3) * mm});
            skLineSegment(sketch, "E2.3.10.0", {"start": v(102.5, 350.3) * mm, "end": v(77.5, 350.3) * mm});
            skLineSegment(sketch, "E2.3.10.1", {"start": v(102.5, 325.3) * mm, "end": v(102.5, 350.3) * mm});
            skLineSegment(sketch, "E2.3.10.2", {"start": v(102.5, 325.3) * mm, "end": v(77.5, 325.3) * mm});
            skLineSegment(sketch, "E2.3.10.3", {"start": v(77.5, 325.3) * mm, "end": v(77.5, 350.3) * mm});
            skLineSegment(sketch, "E2.3.11.0", {"start": v(102.5, 380.3) * mm, "end": v(77.5, 380.3) * mm});
            skLineSegment(sketch, "E2.3.11.1", {"start": v(102.5, 355.3) * mm, "end": v(102.5, 380.3) * mm});
            skLineSegment(sketch, "E2.3.11.2", {"start": v(102.5, 355.3) * mm, "end": v(77.5, 355.3) * mm});
            skLineSegment(sketch, "E2.3.11.3", {"start": v(77.5, 355.3) * mm, "end": v(77.5, 380.3) * mm});
            skLineSegment(sketch, "E2.3.12.0", {"start": v(102.5, 410.3) * mm, "end": v(77.5, 410.3) * mm});
            skLineSegment(sketch, "E2.3.12.1", {"start": v(102.5, 385.3) * mm, "end": v(102.5, 410.3) * mm});
            skLineSegment(sketch, "E2.3.12.2", {"start": v(102.5, 385.3) * mm, "end": v(77.5, 385.3) * mm});
            skLineSegment(sketch, "E2.3.12.3", {"start": v(77.5, 385.3) * mm, "end": v(77.5, 410.3) * mm});
            skLineSegment(sketch, "E2.3.13.0", {"start": v(102.5, 440.3) * mm, "end": v(77.5, 440.3) * mm});
            skLineSegment(sketch, "E2.3.13.1", {"start": v(102.5, 415.3) * mm, "end": v(102.5, 440.3) * mm});
            skLineSegment(sketch, "E2.3.13.2", {"start": v(102.5, 415.3) * mm, "end": v(77.5, 415.3) * mm});
            skLineSegment(sketch, "E2.3.13.3", {"start": v(77.5, 415.3) * mm, "end": v(77.5, 440.3) * mm});
            skLineSegment(sketch, "E2.3.14.0", {"start": v(102.5, 470.3) * mm, "end": v(77.5, 470.3) * mm});
            skLineSegment(sketch, "E2.3.14.1", {"start": v(102.5, 445.3) * mm, "end": v(102.5, 470.3) * mm});
            skLineSegment(sketch, "E2.3.14.2", {"start": v(102.5, 445.3) * mm, "end": v(77.5, 445.3) * mm});
            skLineSegment(sketch, "E2.3.14.3", {"start": v(77.5, 445.3) * mm, "end": v(77.5, 470.3) * mm});
            skLineSegment(sketch, "E2.3.15.0", {"start": v(102.5, 500.3) * mm, "end": v(77.5, 500.3) * mm});
            skLineSegment(sketch, "E2.3.15.1", {"start": v(102.5, 475.3) * mm, "end": v(102.5, 500.3) * mm});
            skLineSegment(sketch, "E2.3.15.2", {"start": v(102.5, 475.3) * mm, "end": v(77.5, 475.3) * mm});
            skLineSegment(sketch, "E2.3.15.3", {"start": v(77.5, 475.3) * mm, "end": v(77.5, 500.3) * mm});
            skLineSegment(sketch, "E2.3.16.0", {"start": v(102.5, 530.3) * mm, "end": v(77.5, 530.3) * mm});
            skLineSegment(sketch, "E2.3.16.1", {"start": v(102.5, 505.3) * mm, "end": v(102.5, 530.3) * mm});
            skLineSegment(sketch, "E2.3.16.2", {"start": v(102.5, 505.3) * mm, "end": v(77.5, 505.3) * mm});
            skLineSegment(sketch, "E2.3.16.3", {"start": v(77.5, 505.3) * mm, "end": v(77.5, 530.3) * mm});
            skLineSegment(sketch, "E2.3.17.0", {"start": v(102.5, 560.3) * mm, "end": v(77.5, 560.3) * mm});
            skLineSegment(sketch, "E2.3.17.1", {"start": v(102.5, 535.3) * mm, "end": v(102.5, 560.3) * mm});
            skLineSegment(sketch, "E2.3.17.2", {"start": v(102.5, 535.3) * mm, "end": v(77.5, 535.3) * mm});
            skLineSegment(sketch, "E2.3.17.3", {"start": v(77.5, 535.3) * mm, "end": v(77.5, 560.3) * mm});
            skLineSegment(sketch, "E2.3.18.0", {"start": v(102.5, 590.3) * mm, "end": v(77.5, 590.3) * mm});
            skLineSegment(sketch, "E2.3.18.1", {"start": v(102.5, 565.3) * mm, "end": v(102.5, 590.3) * mm});
            skLineSegment(sketch, "E2.3.18.2", {"start": v(102.5, 565.3) * mm, "end": v(77.5, 565.3) * mm});
            skLineSegment(sketch, "E2.3.18.3", {"start": v(77.5, 565.3) * mm, "end": v(77.5, 590.3) * mm});
            skLineSegment(sketch, "E2.3.19.0", {"start": v(102.5, 620.3) * mm, "end": v(77.5, 620.3) * mm});
            skLineSegment(sketch, "E2.3.19.1", {"start": v(102.5, 595.3) * mm, "end": v(102.5, 620.3) * mm});
            skLineSegment(sketch, "E2.3.19.2", {"start": v(102.5, 595.3) * mm, "end": v(77.5, 595.3) * mm});
            skLineSegment(sketch, "E2.3.19.3", {"start": v(77.5, 595.3) * mm, "end": v(77.5, 620.3) * mm});
            skLineSegment(sketch, "E2.3.20.0", {"start": v(102.5, 650.3) * mm, "end": v(77.5, 650.3) * mm});
            skLineSegment(sketch, "E2.3.20.1", {"start": v(102.5, 625.3) * mm, "end": v(102.5, 650.3) * mm});
            skLineSegment(sketch, "E2.3.20.2", {"start": v(102.5, 625.3) * mm, "end": v(77.5, 625.3) * mm});
            skLineSegment(sketch, "E2.3.20.3", {"start": v(77.5, 625.3) * mm, "end": v(77.5, 650.3) * mm});
            skLineSegment(sketch, "E2.3.21.0", {"start": v(102.5, 680.3) * mm, "end": v(77.5, 680.3) * mm});
            skLineSegment(sketch, "E2.3.21.1", {"start": v(102.5, 655.3) * mm, "end": v(102.5, 680.3) * mm});
            skLineSegment(sketch, "E2.3.21.2", {"start": v(102.5, 655.3) * mm, "end": v(77.5, 655.3) * mm});
            skLineSegment(sketch, "E2.3.21.3", {"start": v(77.5, 655.3) * mm, "end": v(77.5, 680.3) * mm});
            skLineSegment(sketch, "E2.3.22.0", {"start": v(102.5, 710.3) * mm, "end": v(77.5, 710.3) * mm});
            skLineSegment(sketch, "E2.3.22.1", {"start": v(102.5, 685.3) * mm, "end": v(102.5, 710.3) * mm});
            skLineSegment(sketch, "E2.3.22.2", {"start": v(102.5, 685.3) * mm, "end": v(77.5, 685.3) * mm});
            skLineSegment(sketch, "E2.3.22.3", {"start": v(77.5, 685.3) * mm, "end": v(77.5, 710.3) * mm});
            skLineSegment(sketch, "E2.3.23.0", {"start": v(102.5, 740.3) * mm, "end": v(77.5, 740.3) * mm});
            skLineSegment(sketch, "E2.3.23.1", {"start": v(102.5, 715.3) * mm, "end": v(102.5, 740.3) * mm});
            skLineSegment(sketch, "E2.3.23.2", {"start": v(102.5, 715.3) * mm, "end": v(77.5, 715.3) * mm});
            skLineSegment(sketch, "E2.3.23.3", {"start": v(77.5, 715.3) * mm, "end": v(77.5, 740.3) * mm});
            skLineSegment(sketch, "E2.3.24.0", {"start": v(102.5, 770.3) * mm, "end": v(77.5, 770.3) * mm});
            skLineSegment(sketch, "E2.3.24.1", {"start": v(102.5, 745.3) * mm, "end": v(102.5, 770.3) * mm});
            skLineSegment(sketch, "E2.3.24.2", {"start": v(102.5, 745.3) * mm, "end": v(77.5, 745.3) * mm});
            skLineSegment(sketch, "E2.3.24.3", {"start": v(77.5, 745.3) * mm, "end": v(77.5, 770.3) * mm});
            skLineSegment(sketch, "E2.3.25.0", {"start": v(102.5, 800.3) * mm, "end": v(77.5, 800.3) * mm});
            skLineSegment(sketch, "E2.3.25.1", {"start": v(102.5, 775.3) * mm, "end": v(102.5, 800.3) * mm});
            skLineSegment(sketch, "E2.3.25.2", {"start": v(102.5, 775.3) * mm, "end": v(77.5, 775.3) * mm});
            skLineSegment(sketch, "E2.3.25.3", {"start": v(77.5, 775.3) * mm, "end": v(77.5, 800.3) * mm});
            skLineSegment(sketch, "E2.3.26.0", {"start": v(102.5, 830.3) * mm, "end": v(77.5, 830.3) * mm});
            skLineSegment(sketch, "E2.3.26.1", {"start": v(102.5, 805.3) * mm, "end": v(102.5, 830.3) * mm});
            skLineSegment(sketch, "E2.3.26.2", {"start": v(102.5, 805.3) * mm, "end": v(77.5, 805.3) * mm});
            skLineSegment(sketch, "E2.3.26.3", {"start": v(77.5, 805.3) * mm, "end": v(77.5, 830.3) * mm});
            skLineSegment(sketch, "E2.3.27.0", {"start": v(102.5, 860.3) * mm, "end": v(77.5, 860.3) * mm});
            skLineSegment(sketch, "E2.3.27.1", {"start": v(102.5, 835.3) * mm, "end": v(102.5, 860.3) * mm});
            skLineSegment(sketch, "E2.3.27.2", {"start": v(102.5, 835.3) * mm, "end": v(77.5, 835.3) * mm});
            skLineSegment(sketch, "E2.3.27.3", {"start": v(77.5, 835.3) * mm, "end": v(77.5, 860.3) * mm});
            skLineSegment(sketch, "E2.3.28.0", {"start": v(102.5, 890.3) * mm, "end": v(77.5, 890.3) * mm});
            skLineSegment(sketch, "E2.3.28.1", {"start": v(102.5, 865.3) * mm, "end": v(102.5, 890.3) * mm});
            skLineSegment(sketch, "E2.3.28.2", {"start": v(102.5, 865.3) * mm, "end": v(77.5, 865.3) * mm});
            skLineSegment(sketch, "E2.3.28.3", {"start": v(77.5, 865.3) * mm, "end": v(77.5, 890.3) * mm});
            skLineSegment(sketch, "E2.3.29.0", {"start": v(102.5, 920.3) * mm, "end": v(77.5, 920.3) * mm});
            skLineSegment(sketch, "E2.3.29.1", {"start": v(102.5, 895.3) * mm, "end": v(102.5, 920.3) * mm});
            skLineSegment(sketch, "E2.3.29.2", {"start": v(102.5, 895.3) * mm, "end": v(77.5, 895.3) * mm});
            skLineSegment(sketch, "E2.3.29.3", {"start": v(77.5, 895.3) * mm, "end": v(77.5, 920.3) * mm});
            skLineSegment(sketch, "E2.3.30.0", {"start": v(102.5, 950.3) * mm, "end": v(77.5, 950.3) * mm});
            skLineSegment(sketch, "E2.3.30.1", {"start": v(102.5, 925.3) * mm, "end": v(102.5, 950.3) * mm});
            skLineSegment(sketch, "E2.3.30.2", {"start": v(102.5, 925.3) * mm, "end": v(77.5, 925.3) * mm});
            skLineSegment(sketch, "E2.3.30.3", {"start": v(77.5, 925.3) * mm, "end": v(77.5, 950.3) * mm});
            skLineSegment(sketch, "E2.4.0.0", {"start": v(132.5, 50.3) * mm, "end": v(107.5, 50.3) * mm});
            skLineSegment(sketch, "E2.4.0.1", {"start": v(132.5, 25.3) * mm, "end": v(132.5, 50.3) * mm});
            skLineSegment(sketch, "E2.4.0.2", {"start": v(132.5, 25.3) * mm, "end": v(107.5, 25.3) * mm});
            skLineSegment(sketch, "E2.4.0.3", {"start": v(107.5, 25.3) * mm, "end": v(107.5, 50.3) * mm});
            skLineSegment(sketch, "E2.4.1.0", {"start": v(132.5, 80.3) * mm, "end": v(107.5, 80.3) * mm});
            skLineSegment(sketch, "E2.4.1.1", {"start": v(132.5, 55.3) * mm, "end": v(132.5, 80.3) * mm});
            skLineSegment(sketch, "E2.4.1.2", {"start": v(132.5, 55.3) * mm, "end": v(107.5, 55.3) * mm});
            skLineSegment(sketch, "E2.4.1.3", {"start": v(107.5, 55.3) * mm, "end": v(107.5, 80.3) * mm});
            skLineSegment(sketch, "E2.4.2.0", {"start": v(132.5, 110.3) * mm, "end": v(107.5, 110.3) * mm});
            skLineSegment(sketch, "E2.4.2.1", {"start": v(132.5, 85.3) * mm, "end": v(132.5, 110.3) * mm});
            skLineSegment(sketch, "E2.4.2.2", {"start": v(132.5, 85.3) * mm, "end": v(107.5, 85.3) * mm});
            skLineSegment(sketch, "E2.4.2.3", {"start": v(107.5, 85.3) * mm, "end": v(107.5, 110.3) * mm});
            skLineSegment(sketch, "E2.4.3.0", {"start": v(132.5, 140.3) * mm, "end": v(107.5, 140.3) * mm});
            skLineSegment(sketch, "E2.4.3.1", {"start": v(132.5, 115.3) * mm, "end": v(132.5, 140.3) * mm});
            skLineSegment(sketch, "E2.4.3.2", {"start": v(132.5, 115.3) * mm, "end": v(107.5, 115.3) * mm});
            skLineSegment(sketch, "E2.4.3.3", {"start": v(107.5, 115.3) * mm, "end": v(107.5, 140.3) * mm});
            skLineSegment(sketch, "E2.4.4.0", {"start": v(132.5, 170.3) * mm, "end": v(107.5, 170.3) * mm});
            skLineSegment(sketch, "E2.4.4.1", {"start": v(132.5, 145.3) * mm, "end": v(132.5, 170.3) * mm});
            skLineSegment(sketch, "E2.4.4.2", {"start": v(132.5, 145.3) * mm, "end": v(107.5, 145.3) * mm});
            skLineSegment(sketch, "E2.4.4.3", {"start": v(107.5, 145.3) * mm, "end": v(107.5, 170.3) * mm});
            skLineSegment(sketch, "E2.4.5.0", {"start": v(132.5, 200.3) * mm, "end": v(107.5, 200.3) * mm});
            skLineSegment(sketch, "E2.4.5.1", {"start": v(132.5, 175.3) * mm, "end": v(132.5, 200.3) * mm});
            skLineSegment(sketch, "E2.4.5.2", {"start": v(132.5, 175.3) * mm, "end": v(107.5, 175.3) * mm});
            skLineSegment(sketch, "E2.4.5.3", {"start": v(107.5, 175.3) * mm, "end": v(107.5, 200.3) * mm});
            skLineSegment(sketch, "E2.4.6.0", {"start": v(132.5, 230.3) * mm, "end": v(107.5, 230.3) * mm});
            skLineSegment(sketch, "E2.4.6.1", {"start": v(132.5, 205.3) * mm, "end": v(132.5, 230.3) * mm});
            skLineSegment(sketch, "E2.4.6.2", {"start": v(132.5, 205.3) * mm, "end": v(107.5, 205.3) * mm});
            skLineSegment(sketch, "E2.4.6.3", {"start": v(107.5, 205.3) * mm, "end": v(107.5, 230.3) * mm});
            skLineSegment(sketch, "E2.4.7.0", {"start": v(132.5, 260.3) * mm, "end": v(107.5, 260.3) * mm});
            skLineSegment(sketch, "E2.4.7.1", {"start": v(132.5, 235.3) * mm, "end": v(132.5, 260.3) * mm});
            skLineSegment(sketch, "E2.4.7.2", {"start": v(132.5, 235.3) * mm, "end": v(107.5, 235.3) * mm});
            skLineSegment(sketch, "E2.4.7.3", {"start": v(107.5, 235.3) * mm, "end": v(107.5, 260.3) * mm});
            skLineSegment(sketch, "E2.4.8.0", {"start": v(132.5, 290.3) * mm, "end": v(107.5, 290.3) * mm});
            skLineSegment(sketch, "E2.4.8.1", {"start": v(132.5, 265.3) * mm, "end": v(132.5, 290.3) * mm});
            skLineSegment(sketch, "E2.4.8.2", {"start": v(132.5, 265.3) * mm, "end": v(107.5, 265.3) * mm});
            skLineSegment(sketch, "E2.4.8.3", {"start": v(107.5, 265.3) * mm, "end": v(107.5, 290.3) * mm});
            skLineSegment(sketch, "E2.4.9.0", {"start": v(132.5, 320.3) * mm, "end": v(107.5, 320.3) * mm});
            skLineSegment(sketch, "E2.4.9.1", {"start": v(132.5, 295.3) * mm, "end": v(132.5, 320.3) * mm});
            skLineSegment(sketch, "E2.4.9.2", {"start": v(132.5, 295.3) * mm, "end": v(107.5, 295.3) * mm});
            skLineSegment(sketch, "E2.4.9.3", {"start": v(107.5, 295.3) * mm, "end": v(107.5, 320.3) * mm});
            skLineSegment(sketch, "E2.4.10.0", {"start": v(132.5, 350.3) * mm, "end": v(107.5, 350.3) * mm});
            skLineSegment(sketch, "E2.4.10.1", {"start": v(132.5, 325.3) * mm, "end": v(132.5, 350.3) * mm});
            skLineSegment(sketch, "E2.4.10.2", {"start": v(132.5, 325.3) * mm, "end": v(107.5, 325.3) * mm});
            skLineSegment(sketch, "E2.4.10.3", {"start": v(107.5, 325.3) * mm, "end": v(107.5, 350.3) * mm});
            skLineSegment(sketch, "E2.4.11.0", {"start": v(132.5, 380.3) * mm, "end": v(107.5, 380.3) * mm});
            skLineSegment(sketch, "E2.4.11.1", {"start": v(132.5, 355.3) * mm, "end": v(132.5, 380.3) * mm});
            skLineSegment(sketch, "E2.4.11.2", {"start": v(132.5, 355.3) * mm, "end": v(107.5, 355.3) * mm});
            skLineSegment(sketch, "E2.4.11.3", {"start": v(107.5, 355.3) * mm, "end": v(107.5, 380.3) * mm});
            skLineSegment(sketch, "E2.4.12.0", {"start": v(132.5, 410.3) * mm, "end": v(107.5, 410.3) * mm});
            skLineSegment(sketch, "E2.4.12.1", {"start": v(132.5, 385.3) * mm, "end": v(132.5, 410.3) * mm});
            skLineSegment(sketch, "E2.4.12.2", {"start": v(132.5, 385.3) * mm, "end": v(107.5, 385.3) * mm});
            skLineSegment(sketch, "E2.4.12.3", {"start": v(107.5, 385.3) * mm, "end": v(107.5, 410.3) * mm});
            skLineSegment(sketch, "E2.4.13.0", {"start": v(132.5, 440.3) * mm, "end": v(107.5, 440.3) * mm});
            skLineSegment(sketch, "E2.4.13.1", {"start": v(132.5, 415.3) * mm, "end": v(132.5, 440.3) * mm});
            skLineSegment(sketch, "E2.4.13.2", {"start": v(132.5, 415.3) * mm, "end": v(107.5, 415.3) * mm});
            skLineSegment(sketch, "E2.4.13.3", {"start": v(107.5, 415.3) * mm, "end": v(107.5, 440.3) * mm});
            skLineSegment(sketch, "E2.4.14.0", {"start": v(132.5, 470.3) * mm, "end": v(107.5, 470.3) * mm});
            skLineSegment(sketch, "E2.4.14.1", {"start": v(132.5, 445.3) * mm, "end": v(132.5, 470.3) * mm});
            skLineSegment(sketch, "E2.4.14.2", {"start": v(132.5, 445.3) * mm, "end": v(107.5, 445.3) * mm});
            skLineSegment(sketch, "E2.4.14.3", {"start": v(107.5, 445.3) * mm, "end": v(107.5, 470.3) * mm});
            skLineSegment(sketch, "E2.4.15.0", {"start": v(132.5, 500.3) * mm, "end": v(107.5, 500.3) * mm});
            skLineSegment(sketch, "E2.4.15.1", {"start": v(132.5, 475.3) * mm, "end": v(132.5, 500.3) * mm});
            skLineSegment(sketch, "E2.4.15.2", {"start": v(132.5, 475.3) * mm, "end": v(107.5, 475.3) * mm});
            skLineSegment(sketch, "E2.4.15.3", {"start": v(107.5, 475.3) * mm, "end": v(107.5, 500.3) * mm});
            skLineSegment(sketch, "E2.4.16.0", {"start": v(132.5, 530.3) * mm, "end": v(107.5, 530.3) * mm});
            skLineSegment(sketch, "E2.4.16.1", {"start": v(132.5, 505.3) * mm, "end": v(132.5, 530.3) * mm});
            skLineSegment(sketch, "E2.4.16.2", {"start": v(132.5, 505.3) * mm, "end": v(107.5, 505.3) * mm});
            skLineSegment(sketch, "E2.4.16.3", {"start": v(107.5, 505.3) * mm, "end": v(107.5, 530.3) * mm});
            skLineSegment(sketch, "E2.4.17.0", {"start": v(132.5, 560.3) * mm, "end": v(107.5, 560.3) * mm});
            skLineSegment(sketch, "E2.4.17.1", {"start": v(132.5, 535.3) * mm, "end": v(132.5, 560.3) * mm});
            skLineSegment(sketch, "E2.4.17.2", {"start": v(132.5, 535.3) * mm, "end": v(107.5, 535.3) * mm});
            skLineSegment(sketch, "E2.4.17.3", {"start": v(107.5, 535.3) * mm, "end": v(107.5, 560.3) * mm});
            skLineSegment(sketch, "E2.4.18.0", {"start": v(132.5, 590.3) * mm, "end": v(107.5, 590.3) * mm});
            skLineSegment(sketch, "E2.4.18.1", {"start": v(132.5, 565.3) * mm, "end": v(132.5, 590.3) * mm});
            skLineSegment(sketch, "E2.4.18.2", {"start": v(132.5, 565.3) * mm, "end": v(107.5, 565.3) * mm});
            skLineSegment(sketch, "E2.4.18.3", {"start": v(107.5, 565.3) * mm, "end": v(107.5, 590.3) * mm});
            skLineSegment(sketch, "E2.4.19.0", {"start": v(132.5, 620.3) * mm, "end": v(107.5, 620.3) * mm});
            skLineSegment(sketch, "E2.4.19.1", {"start": v(132.5, 595.3) * mm, "end": v(132.5, 620.3) * mm});
            skLineSegment(sketch, "E2.4.19.2", {"start": v(132.5, 595.3) * mm, "end": v(107.5, 595.3) * mm});
            skLineSegment(sketch, "E2.4.19.3", {"start": v(107.5, 595.3) * mm, "end": v(107.5, 620.3) * mm});
            skLineSegment(sketch, "E2.4.20.0", {"start": v(132.5, 650.3) * mm, "end": v(107.5, 650.3) * mm});
            skLineSegment(sketch, "E2.4.20.1", {"start": v(132.5, 625.3) * mm, "end": v(132.5, 650.3) * mm});
            skLineSegment(sketch, "E2.4.20.2", {"start": v(132.5, 625.3) * mm, "end": v(107.5, 625.3) * mm});
            skLineSegment(sketch, "E2.4.20.3", {"start": v(107.5, 625.3) * mm, "end": v(107.5, 650.3) * mm});
            skLineSegment(sketch, "E2.4.21.0", {"start": v(132.5, 680.3) * mm, "end": v(107.5, 680.3) * mm});
            skLineSegment(sketch, "E2.4.21.1", {"start": v(132.5, 655.3) * mm, "end": v(132.5, 680.3) * mm});
            skLineSegment(sketch, "E2.4.21.2", {"start": v(132.5, 655.3) * mm, "end": v(107.5, 655.3) * mm});
            skLineSegment(sketch, "E2.4.21.3", {"start": v(107.5, 655.3) * mm, "end": v(107.5, 680.3) * mm});
            skLineSegment(sketch, "E2.4.22.0", {"start": v(132.5, 710.3) * mm, "end": v(107.5, 710.3) * mm});
            skLineSegment(sketch, "E2.4.22.1", {"start": v(132.5, 685.3) * mm, "end": v(132.5, 710.3) * mm});
            skLineSegment(sketch, "E2.4.22.2", {"start": v(132.5, 685.3) * mm, "end": v(107.5, 685.3) * mm});
            skLineSegment(sketch, "E2.4.22.3", {"start": v(107.5, 685.3) * mm, "end": v(107.5, 710.3) * mm});
            skLineSegment(sketch, "E2.4.23.0", {"start": v(132.5, 740.3) * mm, "end": v(107.5, 740.3) * mm});
            skLineSegment(sketch, "E2.4.23.1", {"start": v(132.5, 715.3) * mm, "end": v(132.5, 740.3) * mm});
            skLineSegment(sketch, "E2.4.23.2", {"start": v(132.5, 715.3) * mm, "end": v(107.5, 715.3) * mm});
            skLineSegment(sketch, "E2.4.23.3", {"start": v(107.5, 715.3) * mm, "end": v(107.5, 740.3) * mm});
            skLineSegment(sketch, "E2.4.24.0", {"start": v(132.5, 770.3) * mm, "end": v(107.5, 770.3) * mm});
            skLineSegment(sketch, "E2.4.24.1", {"start": v(132.5, 745.3) * mm, "end": v(132.5, 770.3) * mm});
            skLineSegment(sketch, "E2.4.24.2", {"start": v(132.5, 745.3) * mm, "end": v(107.5, 745.3) * mm});
            skLineSegment(sketch, "E2.4.24.3", {"start": v(107.5, 745.3) * mm, "end": v(107.5, 770.3) * mm});
            skLineSegment(sketch, "E2.4.25.0", {"start": v(132.5, 800.3) * mm, "end": v(107.5, 800.3) * mm});
            skLineSegment(sketch, "E2.4.25.1", {"start": v(132.5, 775.3) * mm, "end": v(132.5, 800.3) * mm});
            skLineSegment(sketch, "E2.4.25.2", {"start": v(132.5, 775.3) * mm, "end": v(107.5, 775.3) * mm});
            skLineSegment(sketch, "E2.4.25.3", {"start": v(107.5, 775.3) * mm, "end": v(107.5, 800.3) * mm});
            skLineSegment(sketch, "E2.4.26.0", {"start": v(132.5, 830.3) * mm, "end": v(107.5, 830.3) * mm});
            skLineSegment(sketch, "E2.4.26.1", {"start": v(132.5, 805.3) * mm, "end": v(132.5, 830.3) * mm});
            skLineSegment(sketch, "E2.4.26.2", {"start": v(132.5, 805.3) * mm, "end": v(107.5, 805.3) * mm});
            skLineSegment(sketch, "E2.4.26.3", {"start": v(107.5, 805.3) * mm, "end": v(107.5, 830.3) * mm});
            skLineSegment(sketch, "E2.4.27.0", {"start": v(132.5, 860.3) * mm, "end": v(107.5, 860.3) * mm});
            skLineSegment(sketch, "E2.4.27.1", {"start": v(132.5, 835.3) * mm, "end": v(132.5, 860.3) * mm});
            skLineSegment(sketch, "E2.4.27.2", {"start": v(132.5, 835.3) * mm, "end": v(107.5, 835.3) * mm});
            skLineSegment(sketch, "E2.4.27.3", {"start": v(107.5, 835.3) * mm, "end": v(107.5, 860.3) * mm});
            skLineSegment(sketch, "E2.4.28.0", {"start": v(132.5, 890.3) * mm, "end": v(107.5, 890.3) * mm});
            skLineSegment(sketch, "E2.4.28.1", {"start": v(132.5, 865.3) * mm, "end": v(132.5, 890.3) * mm});
            skLineSegment(sketch, "E2.4.28.2", {"start": v(132.5, 865.3) * mm, "end": v(107.5, 865.3) * mm});
            skLineSegment(sketch, "E2.4.28.3", {"start": v(107.5, 865.3) * mm, "end": v(107.5, 890.3) * mm});
            skLineSegment(sketch, "E2.4.29.0", {"start": v(132.5, 920.3) * mm, "end": v(107.5, 920.3) * mm});
            skLineSegment(sketch, "E2.4.29.1", {"start": v(132.5, 895.3) * mm, "end": v(132.5, 920.3) * mm});
            skLineSegment(sketch, "E2.4.29.2", {"start": v(132.5, 895.3) * mm, "end": v(107.5, 895.3) * mm});
            skLineSegment(sketch, "E2.4.29.3", {"start": v(107.5, 895.3) * mm, "end": v(107.5, 920.3) * mm});
            skLineSegment(sketch, "E2.4.30.0", {"start": v(132.5, 950.3) * mm, "end": v(107.5, 950.3) * mm});
            skLineSegment(sketch, "E2.4.30.1", {"start": v(132.5, 925.3) * mm, "end": v(132.5, 950.3) * mm});
            skLineSegment(sketch, "E2.4.30.2", {"start": v(132.5, 925.3) * mm, "end": v(107.5, 925.3) * mm});
            skLineSegment(sketch, "E2.4.30.3", {"start": v(107.5, 925.3) * mm, "end": v(107.5, 950.3) * mm});
            skLineSegment(sketch, "E2.5.0.0", {"start": v(162.5, 50.3) * mm, "end": v(137.5, 50.3) * mm});
            skLineSegment(sketch, "E2.5.0.1", {"start": v(162.5, 25.3) * mm, "end": v(162.5, 50.3) * mm});
            skLineSegment(sketch, "E2.5.0.2", {"start": v(162.5, 25.3) * mm, "end": v(137.5, 25.3) * mm});
            skLineSegment(sketch, "E2.5.0.3", {"start": v(137.5, 25.3) * mm, "end": v(137.5, 50.3) * mm});
            skLineSegment(sketch, "E2.5.1.0", {"start": v(162.5, 80.3) * mm, "end": v(137.5, 80.3) * mm});
            skLineSegment(sketch, "E2.5.1.1", {"start": v(162.5, 55.3) * mm, "end": v(162.5, 80.3) * mm});
            skLineSegment(sketch, "E2.5.1.2", {"start": v(162.5, 55.3) * mm, "end": v(137.5, 55.3) * mm});
            skLineSegment(sketch, "E2.5.1.3", {"start": v(137.5, 55.3) * mm, "end": v(137.5, 80.3) * mm});
            skLineSegment(sketch, "E2.5.2.0", {"start": v(162.5, 110.3) * mm, "end": v(137.5, 110.3) * mm});
            skLineSegment(sketch, "E2.5.2.1", {"start": v(162.5, 85.3) * mm, "end": v(162.5, 110.3) * mm});
            skLineSegment(sketch, "E2.5.2.2", {"start": v(162.5, 85.3) * mm, "end": v(137.5, 85.3) * mm});
            skLineSegment(sketch, "E2.5.2.3", {"start": v(137.5, 85.3) * mm, "end": v(137.5, 110.3) * mm});
            skLineSegment(sketch, "E2.5.3.0", {"start": v(162.5, 140.3) * mm, "end": v(137.5, 140.3) * mm});
            skLineSegment(sketch, "E2.5.3.1", {"start": v(162.5, 115.3) * mm, "end": v(162.5, 140.3) * mm});
            skLineSegment(sketch, "E2.5.3.2", {"start": v(162.5, 115.3) * mm, "end": v(137.5, 115.3) * mm});
            skLineSegment(sketch, "E2.5.3.3", {"start": v(137.5, 115.3) * mm, "end": v(137.5, 140.3) * mm});
            skLineSegment(sketch, "E2.5.4.0", {"start": v(162.5, 170.3) * mm, "end": v(137.5, 170.3) * mm});
            skLineSegment(sketch, "E2.5.4.1", {"start": v(162.5, 145.3) * mm, "end": v(162.5, 170.3) * mm});
            skLineSegment(sketch, "E2.5.4.2", {"start": v(162.5, 145.3) * mm, "end": v(137.5, 145.3) * mm});
            skLineSegment(sketch, "E2.5.4.3", {"start": v(137.5, 145.3) * mm, "end": v(137.5, 170.3) * mm});
            skLineSegment(sketch, "E2.5.5.0", {"start": v(162.5, 200.3) * mm, "end": v(137.5, 200.3) * mm});
            skLineSegment(sketch, "E2.5.5.1", {"start": v(162.5, 175.3) * mm, "end": v(162.5, 200.3) * mm});
            skLineSegment(sketch, "E2.5.5.2", {"start": v(162.5, 175.3) * mm, "end": v(137.5, 175.3) * mm});
            skLineSegment(sketch, "E2.5.5.3", {"start": v(137.5, 175.3) * mm, "end": v(137.5, 200.3) * mm});
            skLineSegment(sketch, "E2.5.6.0", {"start": v(162.5, 230.3) * mm, "end": v(137.5, 230.3) * mm});
            skLineSegment(sketch, "E2.5.6.1", {"start": v(162.5, 205.3) * mm, "end": v(162.5, 230.3) * mm});
            skLineSegment(sketch, "E2.5.6.2", {"start": v(162.5, 205.3) * mm, "end": v(137.5, 205.3) * mm});
            skLineSegment(sketch, "E2.5.6.3", {"start": v(137.5, 205.3) * mm, "end": v(137.5, 230.3) * mm});
            skLineSegment(sketch, "E2.5.7.0", {"start": v(162.5, 260.3) * mm, "end": v(137.5, 260.3) * mm});
            skLineSegment(sketch, "E2.5.7.1", {"start": v(162.5, 235.3) * mm, "end": v(162.5, 260.3) * mm});
            skLineSegment(sketch, "E2.5.7.2", {"start": v(162.5, 235.3) * mm, "end": v(137.5, 235.3) * mm});
            skLineSegment(sketch, "E2.5.7.3", {"start": v(137.5, 235.3) * mm, "end": v(137.5, 260.3) * mm});
            skLineSegment(sketch, "E2.5.8.0", {"start": v(162.5, 290.3) * mm, "end": v(137.5, 290.3) * mm});
            skLineSegment(sketch, "E2.5.8.1", {"start": v(162.5, 265.3) * mm, "end": v(162.5, 290.3) * mm});
            skLineSegment(sketch, "E2.5.8.2", {"start": v(162.5, 265.3) * mm, "end": v(137.5, 265.3) * mm});
            skLineSegment(sketch, "E2.5.8.3", {"start": v(137.5, 265.3) * mm, "end": v(137.5, 290.3) * mm});
            skLineSegment(sketch, "E2.5.9.0", {"start": v(162.5, 320.3) * mm, "end": v(137.5, 320.3) * mm});
            skLineSegment(sketch, "E2.5.9.1", {"start": v(162.5, 295.3) * mm, "end": v(162.5, 320.3) * mm});
            skLineSegment(sketch, "E2.5.9.2", {"start": v(162.5, 295.3) * mm, "end": v(137.5, 295.3) * mm});
            skLineSegment(sketch, "E2.5.9.3", {"start": v(137.5, 295.3) * mm, "end": v(137.5, 320.3) * mm});
            skLineSegment(sketch, "E2.5.10.0", {"start": v(162.5, 350.3) * mm, "end": v(137.5, 350.3) * mm});
            skLineSegment(sketch, "E2.5.10.1", {"start": v(162.5, 325.3) * mm, "end": v(162.5, 350.3) * mm});
            skLineSegment(sketch, "E2.5.10.2", {"start": v(162.5, 325.3) * mm, "end": v(137.5, 325.3) * mm});
            skLineSegment(sketch, "E2.5.10.3", {"start": v(137.5, 325.3) * mm, "end": v(137.5, 350.3) * mm});
            skLineSegment(sketch, "E2.5.11.0", {"start": v(162.5, 380.3) * mm, "end": v(137.5, 380.3) * mm});
            skLineSegment(sketch, "E2.5.11.1", {"start": v(162.5, 355.3) * mm, "end": v(162.5, 380.3) * mm});
            skLineSegment(sketch, "E2.5.11.2", {"start": v(162.5, 355.3) * mm, "end": v(137.5, 355.3) * mm});
            skLineSegment(sketch, "E2.5.11.3", {"start": v(137.5, 355.3) * mm, "end": v(137.5, 380.3) * mm});
            skLineSegment(sketch, "E2.5.12.0", {"start": v(162.5, 410.3) * mm, "end": v(137.5, 410.3) * mm});
            skLineSegment(sketch, "E2.5.12.1", {"start": v(162.5, 385.3) * mm, "end": v(162.5, 410.3) * mm});
            skLineSegment(sketch, "E2.5.12.2", {"start": v(162.5, 385.3) * mm, "end": v(137.5, 385.3) * mm});
            skLineSegment(sketch, "E2.5.12.3", {"start": v(137.5, 385.3) * mm, "end": v(137.5, 410.3) * mm});
            skLineSegment(sketch, "E2.5.13.0", {"start": v(162.5, 440.3) * mm, "end": v(137.5, 440.3) * mm});
            skLineSegment(sketch, "E2.5.13.1", {"start": v(162.5, 415.3) * mm, "end": v(162.5, 440.3) * mm});
            skLineSegment(sketch, "E2.5.13.2", {"start": v(162.5, 415.3) * mm, "end": v(137.5, 415.3) * mm});
            skLineSegment(sketch, "E2.5.13.3", {"start": v(137.5, 415.3) * mm, "end": v(137.5, 440.3) * mm});
            skLineSegment(sketch, "E2.5.14.0", {"start": v(162.5, 470.3) * mm, "end": v(137.5, 470.3) * mm});
            skLineSegment(sketch, "E2.5.14.1", {"start": v(162.5, 445.3) * mm, "end": v(162.5, 470.3) * mm});
            skLineSegment(sketch, "E2.5.14.2", {"start": v(162.5, 445.3) * mm, "end": v(137.5, 445.3) * mm});
            skLineSegment(sketch, "E2.5.14.3", {"start": v(137.5, 445.3) * mm, "end": v(137.5, 470.3) * mm});
            skLineSegment(sketch, "E2.5.15.0", {"start": v(162.5, 500.3) * mm, "end": v(137.5, 500.3) * mm});
            skLineSegment(sketch, "E2.5.15.1", {"start": v(162.5, 475.3) * mm, "end": v(162.5, 500.3) * mm});
            skLineSegment(sketch, "E2.5.15.2", {"start": v(162.5, 475.3) * mm, "end": v(137.5, 475.3) * mm});
            skLineSegment(sketch, "E2.5.15.3", {"start": v(137.5, 475.3) * mm, "end": v(137.5, 500.3) * mm});
            skLineSegment(sketch, "E2.5.16.0", {"start": v(162.5, 530.3) * mm, "end": v(137.5, 530.3) * mm});
            skLineSegment(sketch, "E2.5.16.1", {"start": v(162.5, 505.3) * mm, "end": v(162.5, 530.3) * mm});
            skLineSegment(sketch, "E2.5.16.2", {"start": v(162.5, 505.3) * mm, "end": v(137.5, 505.3) * mm});
            skLineSegment(sketch, "E2.5.16.3", {"start": v(137.5, 505.3) * mm, "end": v(137.5, 530.3) * mm});
            skLineSegment(sketch, "E2.5.17.0", {"start": v(162.5, 560.3) * mm, "end": v(137.5, 560.3) * mm});
            skLineSegment(sketch, "E2.5.17.1", {"start": v(162.5, 535.3) * mm, "end": v(162.5, 560.3) * mm});
            skLineSegment(sketch, "E2.5.17.2", {"start": v(162.5, 535.3) * mm, "end": v(137.5, 535.3) * mm});
            skLineSegment(sketch, "E2.5.17.3", {"start": v(137.5, 535.3) * mm, "end": v(137.5, 560.3) * mm});
            skLineSegment(sketch, "E2.5.18.0", {"start": v(162.5, 590.3) * mm, "end": v(137.5, 590.3) * mm});
            skLineSegment(sketch, "E2.5.18.1", {"start": v(162.5, 565.3) * mm, "end": v(162.5, 590.3) * mm});
            skLineSegment(sketch, "E2.5.18.2", {"start": v(162.5, 565.3) * mm, "end": v(137.5, 565.3) * mm});
            skLineSegment(sketch, "E2.5.18.3", {"start": v(137.5, 565.3) * mm, "end": v(137.5, 590.3) * mm});
            skLineSegment(sketch, "E2.5.19.0", {"start": v(162.5, 620.3) * mm, "end": v(137.5, 620.3) * mm});
            skLineSegment(sketch, "E2.5.19.1", {"start": v(162.5, 595.3) * mm, "end": v(162.5, 620.3) * mm});
            skLineSegment(sketch, "E2.5.19.2", {"start": v(162.5, 595.3) * mm, "end": v(137.5, 595.3) * mm});
            skLineSegment(sketch, "E2.5.19.3", {"start": v(137.5, 595.3) * mm, "end": v(137.5, 620.3) * mm});
            skLineSegment(sketch, "E2.5.20.0", {"start": v(162.5, 650.3) * mm, "end": v(137.5, 650.3) * mm});
            skLineSegment(sketch, "E2.5.20.1", {"start": v(162.5, 625.3) * mm, "end": v(162.5, 650.3) * mm});
            skLineSegment(sketch, "E2.5.20.2", {"start": v(162.5, 625.3) * mm, "end": v(137.5, 625.3) * mm});
            skLineSegment(sketch, "E2.5.20.3", {"start": v(137.5, 625.3) * mm, "end": v(137.5, 650.3) * mm});
            skLineSegment(sketch, "E2.5.21.0", {"start": v(162.5, 680.3) * mm, "end": v(137.5, 680.3) * mm});
            skLineSegment(sketch, "E2.5.21.1", {"start": v(162.5, 655.3) * mm, "end": v(162.5, 680.3) * mm});
            skLineSegment(sketch, "E2.5.21.2", {"start": v(162.5, 655.3) * mm, "end": v(137.5, 655.3) * mm});
            skLineSegment(sketch, "E2.5.21.3", {"start": v(137.5, 655.3) * mm, "end": v(137.5, 680.3) * mm});
            skLineSegment(sketch, "E2.5.22.0", {"start": v(162.5, 710.3) * mm, "end": v(137.5, 710.3) * mm});
            skLineSegment(sketch, "E2.5.22.1", {"start": v(162.5, 685.3) * mm, "end": v(162.5, 710.3) * mm});
            skLineSegment(sketch, "E2.5.22.2", {"start": v(162.5, 685.3) * mm, "end": v(137.5, 685.3) * mm});
            skLineSegment(sketch, "E2.5.22.3", {"start": v(137.5, 685.3) * mm, "end": v(137.5, 710.3) * mm});
            skLineSegment(sketch, "E2.5.23.0", {"start": v(162.5, 740.3) * mm, "end": v(137.5, 740.3) * mm});
            skLineSegment(sketch, "E2.5.23.1", {"start": v(162.5, 715.3) * mm, "end": v(162.5, 740.3) * mm});
            skLineSegment(sketch, "E2.5.23.2", {"start": v(162.5, 715.3) * mm, "end": v(137.5, 715.3) * mm});
            skLineSegment(sketch, "E2.5.23.3", {"start": v(137.5, 715.3) * mm, "end": v(137.5, 740.3) * mm});
            skLineSegment(sketch, "E2.5.24.0", {"start": v(162.5, 770.3) * mm, "end": v(137.5, 770.3) * mm});
            skLineSegment(sketch, "E2.5.24.1", {"start": v(162.5, 745.3) * mm, "end": v(162.5, 770.3) * mm});
            skLineSegment(sketch, "E2.5.24.2", {"start": v(162.5, 745.3) * mm, "end": v(137.5, 745.3) * mm});
            skLineSegment(sketch, "E2.5.24.3", {"start": v(137.5, 745.3) * mm, "end": v(137.5, 770.3) * mm});
            skLineSegment(sketch, "E2.5.25.0", {"start": v(162.5, 800.3) * mm, "end": v(137.5, 800.3) * mm});
            skLineSegment(sketch, "E2.5.25.1", {"start": v(162.5, 775.3) * mm, "end": v(162.5, 800.3) * mm});
            skLineSegment(sketch, "E2.5.25.2", {"start": v(162.5, 775.3) * mm, "end": v(137.5, 775.3) * mm});
            skLineSegment(sketch, "E2.5.25.3", {"start": v(137.5, 775.3) * mm, "end": v(137.5, 800.3) * mm});
            skLineSegment(sketch, "E2.5.26.0", {"start": v(162.5, 830.3) * mm, "end": v(137.5, 830.3) * mm});
            skLineSegment(sketch, "E2.5.26.1", {"start": v(162.5, 805.3) * mm, "end": v(162.5, 830.3) * mm});
            skLineSegment(sketch, "E2.5.26.2", {"start": v(162.5, 805.3) * mm, "end": v(137.5, 805.3) * mm});
            skLineSegment(sketch, "E2.5.26.3", {"start": v(137.5, 805.3) * mm, "end": v(137.5, 830.3) * mm});
            skLineSegment(sketch, "E2.5.27.0", {"start": v(162.5, 860.3) * mm, "end": v(137.5, 860.3) * mm});
            skLineSegment(sketch, "E2.5.27.1", {"start": v(162.5, 835.3) * mm, "end": v(162.5, 860.3) * mm});
            skLineSegment(sketch, "E2.5.27.2", {"start": v(162.5, 835.3) * mm, "end": v(137.5, 835.3) * mm});
            skLineSegment(sketch, "E2.5.27.3", {"start": v(137.5, 835.3) * mm, "end": v(137.5, 860.3) * mm});
            skLineSegment(sketch, "E2.5.28.0", {"start": v(162.5, 890.3) * mm, "end": v(137.5, 890.3) * mm});
            skLineSegment(sketch, "E2.5.28.1", {"start": v(162.5, 865.3) * mm, "end": v(162.5, 890.3) * mm});
            skLineSegment(sketch, "E2.5.28.2", {"start": v(162.5, 865.3) * mm, "end": v(137.5, 865.3) * mm});
            skLineSegment(sketch, "E2.5.28.3", {"start": v(137.5, 865.3) * mm, "end": v(137.5, 890.3) * mm});
            skLineSegment(sketch, "E2.5.29.0", {"start": v(162.5, 920.3) * mm, "end": v(137.5, 920.3) * mm});
            skLineSegment(sketch, "E2.5.29.1", {"start": v(162.5, 895.3) * mm, "end": v(162.5, 920.3) * mm});
            skLineSegment(sketch, "E2.5.29.2", {"start": v(162.5, 895.3) * mm, "end": v(137.5, 895.3) * mm});
            skLineSegment(sketch, "E2.5.29.3", {"start": v(137.5, 895.3) * mm, "end": v(137.5, 920.3) * mm});
            skLineSegment(sketch, "E2.5.30.0", {"start": v(162.5, 950.3) * mm, "end": v(137.5, 950.3) * mm});
            skLineSegment(sketch, "E2.5.30.1", {"start": v(162.5, 925.3) * mm, "end": v(162.5, 950.3) * mm});
            skLineSegment(sketch, "E2.5.30.2", {"start": v(162.5, 925.3) * mm, "end": v(137.5, 925.3) * mm});
            skLineSegment(sketch, "E2.5.30.3", {"start": v(137.5, 925.3) * mm, "end": v(137.5, 950.3) * mm});
            skLineSegment(sketch, "E2.6.0.0", {"start": v(192.5, 50.3) * mm, "end": v(167.5, 50.3) * mm});
            skLineSegment(sketch, "E2.6.0.1", {"start": v(192.5, 25.3) * mm, "end": v(192.5, 50.3) * mm});
            skLineSegment(sketch, "E2.6.0.2", {"start": v(192.5, 25.3) * mm, "end": v(167.5, 25.3) * mm});
            skLineSegment(sketch, "E2.6.0.3", {"start": v(167.5, 25.3) * mm, "end": v(167.5, 50.3) * mm});
            skLineSegment(sketch, "E2.6.1.0", {"start": v(192.5, 80.3) * mm, "end": v(167.5, 80.3) * mm});
            skLineSegment(sketch, "E2.6.1.1", {"start": v(192.5, 55.3) * mm, "end": v(192.5, 80.3) * mm});
            skLineSegment(sketch, "E2.6.1.2", {"start": v(192.5, 55.3) * mm, "end": v(167.5, 55.3) * mm});
            skLineSegment(sketch, "E2.6.1.3", {"start": v(167.5, 55.3) * mm, "end": v(167.5, 80.3) * mm});
            skLineSegment(sketch, "E2.6.2.0", {"start": v(192.5, 110.3) * mm, "end": v(167.5, 110.3) * mm});
            skLineSegment(sketch, "E2.6.2.1", {"start": v(192.5, 85.3) * mm, "end": v(192.5, 110.3) * mm});
            skLineSegment(sketch, "E2.6.2.2", {"start": v(192.5, 85.3) * mm, "end": v(167.5, 85.3) * mm});
            skLineSegment(sketch, "E2.6.2.3", {"start": v(167.5, 85.3) * mm, "end": v(167.5, 110.3) * mm});
            skLineSegment(sketch, "E2.6.3.0", {"start": v(192.5, 140.3) * mm, "end": v(167.5, 140.3) * mm});
            skLineSegment(sketch, "E2.6.3.1", {"start": v(192.5, 115.3) * mm, "end": v(192.5, 140.3) * mm});
            skLineSegment(sketch, "E2.6.3.2", {"start": v(192.5, 115.3) * mm, "end": v(167.5, 115.3) * mm});
            skLineSegment(sketch, "E2.6.3.3", {"start": v(167.5, 115.3) * mm, "end": v(167.5, 140.3) * mm});
            skLineSegment(sketch, "E2.6.4.0", {"start": v(192.5, 170.3) * mm, "end": v(167.5, 170.3) * mm});
            skLineSegment(sketch, "E2.6.4.1", {"start": v(192.5, 145.3) * mm, "end": v(192.5, 170.3) * mm});
            skLineSegment(sketch, "E2.6.4.2", {"start": v(192.5, 145.3) * mm, "end": v(167.5, 145.3) * mm});
            skLineSegment(sketch, "E2.6.4.3", {"start": v(167.5, 145.3) * mm, "end": v(167.5, 170.3) * mm});
            skLineSegment(sketch, "E2.6.5.0", {"start": v(192.5, 200.3) * mm, "end": v(167.5, 200.3) * mm});
            skLineSegment(sketch, "E2.6.5.1", {"start": v(192.5, 175.3) * mm, "end": v(192.5, 200.3) * mm});
            skLineSegment(sketch, "E2.6.5.2", {"start": v(192.5, 175.3) * mm, "end": v(167.5, 175.3) * mm});
            skLineSegment(sketch, "E2.6.5.3", {"start": v(167.5, 175.3) * mm, "end": v(167.5, 200.3) * mm});
            skLineSegment(sketch, "E2.6.6.0", {"start": v(192.5, 230.3) * mm, "end": v(167.5, 230.3) * mm});
            skLineSegment(sketch, "E2.6.6.1", {"start": v(192.5, 205.3) * mm, "end": v(192.5, 230.3) * mm});
            skLineSegment(sketch, "E2.6.6.2", {"start": v(192.5, 205.3) * mm, "end": v(167.5, 205.3) * mm});
            skLineSegment(sketch, "E2.6.6.3", {"start": v(167.5, 205.3) * mm, "end": v(167.5, 230.3) * mm});
            skLineSegment(sketch, "E2.6.7.0", {"start": v(192.5, 260.3) * mm, "end": v(167.5, 260.3) * mm});
            skLineSegment(sketch, "E2.6.7.1", {"start": v(192.5, 235.3) * mm, "end": v(192.5, 260.3) * mm});
            skLineSegment(sketch, "E2.6.7.2", {"start": v(192.5, 235.3) * mm, "end": v(167.5, 235.3) * mm});
            skLineSegment(sketch, "E2.6.7.3", {"start": v(167.5, 235.3) * mm, "end": v(167.5, 260.3) * mm});
            skLineSegment(sketch, "E2.6.8.0", {"start": v(192.5, 290.3) * mm, "end": v(167.5, 290.3) * mm});
            skLineSegment(sketch, "E2.6.8.1", {"start": v(192.5, 265.3) * mm, "end": v(192.5, 290.3) * mm});
            skLineSegment(sketch, "E2.6.8.2", {"start": v(192.5, 265.3) * mm, "end": v(167.5, 265.3) * mm});
            skLineSegment(sketch, "E2.6.8.3", {"start": v(167.5, 265.3) * mm, "end": v(167.5, 290.3) * mm});
            skLineSegment(sketch, "E2.6.9.0", {"start": v(192.5, 320.3) * mm, "end": v(167.5, 320.3) * mm});
            skLineSegment(sketch, "E2.6.9.1", {"start": v(192.5, 295.3) * mm, "end": v(192.5, 320.3) * mm});
            skLineSegment(sketch, "E2.6.9.2", {"start": v(192.5, 295.3) * mm, "end": v(167.5, 295.3) * mm});
            skLineSegment(sketch, "E2.6.9.3", {"start": v(167.5, 295.3) * mm, "end": v(167.5, 320.3) * mm});
            skLineSegment(sketch, "E2.6.10.0", {"start": v(192.5, 350.3) * mm, "end": v(167.5, 350.3) * mm});
            skLineSegment(sketch, "E2.6.10.1", {"start": v(192.5, 325.3) * mm, "end": v(192.5, 350.3) * mm});
            skLineSegment(sketch, "E2.6.10.2", {"start": v(192.5, 325.3) * mm, "end": v(167.5, 325.3) * mm});
            skLineSegment(sketch, "E2.6.10.3", {"start": v(167.5, 325.3) * mm, "end": v(167.5, 350.3) * mm});
            skLineSegment(sketch, "E2.6.11.0", {"start": v(192.5, 380.3) * mm, "end": v(167.5, 380.3) * mm});
            skLineSegment(sketch, "E2.6.11.1", {"start": v(192.5, 355.3) * mm, "end": v(192.5, 380.3) * mm});
            skLineSegment(sketch, "E2.6.11.2", {"start": v(192.5, 355.3) * mm, "end": v(167.5, 355.3) * mm});
            skLineSegment(sketch, "E2.6.11.3", {"start": v(167.5, 355.3) * mm, "end": v(167.5, 380.3) * mm});
            skLineSegment(sketch, "E2.6.12.0", {"start": v(192.5, 410.3) * mm, "end": v(167.5, 410.3) * mm});
            skLineSegment(sketch, "E2.6.12.1", {"start": v(192.5, 385.3) * mm, "end": v(192.5, 410.3) * mm});
            skLineSegment(sketch, "E2.6.12.2", {"start": v(192.5, 385.3) * mm, "end": v(167.5, 385.3) * mm});
            skLineSegment(sketch, "E2.6.12.3", {"start": v(167.5, 385.3) * mm, "end": v(167.5, 410.3) * mm});
            skLineSegment(sketch, "E2.6.13.0", {"start": v(192.5, 440.3) * mm, "end": v(167.5, 440.3) * mm});
            skLineSegment(sketch, "E2.6.13.1", {"start": v(192.5, 415.3) * mm, "end": v(192.5, 440.3) * mm});
            skLineSegment(sketch, "E2.6.13.2", {"start": v(192.5, 415.3) * mm, "end": v(167.5, 415.3) * mm});
            skLineSegment(sketch, "E2.6.13.3", {"start": v(167.5, 415.3) * mm, "end": v(167.5, 440.3) * mm});
            skLineSegment(sketch, "E2.6.14.0", {"start": v(192.5, 470.3) * mm, "end": v(167.5, 470.3) * mm});
            skLineSegment(sketch, "E2.6.14.1", {"start": v(192.5, 445.3) * mm, "end": v(192.5, 470.3) * mm});
            skLineSegment(sketch, "E2.6.14.2", {"start": v(192.5, 445.3) * mm, "end": v(167.5, 445.3) * mm});
            skLineSegment(sketch, "E2.6.14.3", {"start": v(167.5, 445.3) * mm, "end": v(167.5, 470.3) * mm});
            skLineSegment(sketch, "E2.6.15.0", {"start": v(192.5, 500.3) * mm, "end": v(167.5, 500.3) * mm});
            skLineSegment(sketch, "E2.6.15.1", {"start": v(192.5, 475.3) * mm, "end": v(192.5, 500.3) * mm});
            skLineSegment(sketch, "E2.6.15.2", {"start": v(192.5, 475.3) * mm, "end": v(167.5, 475.3) * mm});
            skLineSegment(sketch, "E2.6.15.3", {"start": v(167.5, 475.3) * mm, "end": v(167.5, 500.3) * mm});
            skLineSegment(sketch, "E2.6.16.0", {"start": v(192.5, 530.3) * mm, "end": v(167.5, 530.3) * mm});
            skLineSegment(sketch, "E2.6.16.1", {"start": v(192.5, 505.3) * mm, "end": v(192.5, 530.3) * mm});
            skLineSegment(sketch, "E2.6.16.2", {"start": v(192.5, 505.3) * mm, "end": v(167.5, 505.3) * mm});
            skLineSegment(sketch, "E2.6.16.3", {"start": v(167.5, 505.3) * mm, "end": v(167.5, 530.3) * mm});
            skLineSegment(sketch, "E2.6.17.0", {"start": v(192.5, 560.3) * mm, "end": v(167.5, 560.3) * mm});
            skLineSegment(sketch, "E2.6.17.1", {"start": v(192.5, 535.3) * mm, "end": v(192.5, 560.3) * mm});
            skLineSegment(sketch, "E2.6.17.2", {"start": v(192.5, 535.3) * mm, "end": v(167.5, 535.3) * mm});
            skLineSegment(sketch, "E2.6.17.3", {"start": v(167.5, 535.3) * mm, "end": v(167.5, 560.3) * mm});
            skLineSegment(sketch, "E2.6.18.0", {"start": v(192.5, 590.3) * mm, "end": v(167.5, 590.3) * mm});
            skLineSegment(sketch, "E2.6.18.1", {"start": v(192.5, 565.3) * mm, "end": v(192.5, 590.3) * mm});
            skLineSegment(sketch, "E2.6.18.2", {"start": v(192.5, 565.3) * mm, "end": v(167.5, 565.3) * mm});
            skLineSegment(sketch, "E2.6.18.3", {"start": v(167.5, 565.3) * mm, "end": v(167.5, 590.3) * mm});
            skLineSegment(sketch, "E2.6.19.0", {"start": v(192.5, 620.3) * mm, "end": v(167.5, 620.3) * mm});
            skLineSegment(sketch, "E2.6.19.1", {"start": v(192.5, 595.3) * mm, "end": v(192.5, 620.3) * mm});
            skLineSegment(sketch, "E2.6.19.2", {"start": v(192.5, 595.3) * mm, "end": v(167.5, 595.3) * mm});
            skLineSegment(sketch, "E2.6.19.3", {"start": v(167.5, 595.3) * mm, "end": v(167.5, 620.3) * mm});
            skLineSegment(sketch, "E2.6.20.0", {"start": v(192.5, 650.3) * mm, "end": v(167.5, 650.3) * mm});
            skLineSegment(sketch, "E2.6.20.1", {"start": v(192.5, 625.3) * mm, "end": v(192.5, 650.3) * mm});
            skLineSegment(sketch, "E2.6.20.2", {"start": v(192.5, 625.3) * mm, "end": v(167.5, 625.3) * mm});
            skLineSegment(sketch, "E2.6.20.3", {"start": v(167.5, 625.3) * mm, "end": v(167.5, 650.3) * mm});
            skLineSegment(sketch, "E2.6.21.0", {"start": v(192.5, 680.3) * mm, "end": v(167.5, 680.3) * mm});
            skLineSegment(sketch, "E2.6.21.1", {"start": v(192.5, 655.3) * mm, "end": v(192.5, 680.3) * mm});
            skLineSegment(sketch, "E2.6.21.2", {"start": v(192.5, 655.3) * mm, "end": v(167.5, 655.3) * mm});
            skLineSegment(sketch, "E2.6.21.3", {"start": v(167.5, 655.3) * mm, "end": v(167.5, 680.3) * mm});
            skLineSegment(sketch, "E2.6.22.0", {"start": v(192.5, 710.3) * mm, "end": v(167.5, 710.3) * mm});
            skLineSegment(sketch, "E2.6.22.1", {"start": v(192.5, 685.3) * mm, "end": v(192.5, 710.3) * mm});
            skLineSegment(sketch, "E2.6.22.2", {"start": v(192.5, 685.3) * mm, "end": v(167.5, 685.3) * mm});
            skLineSegment(sketch, "E2.6.22.3", {"start": v(167.5, 685.3) * mm, "end": v(167.5, 710.3) * mm});
            skLineSegment(sketch, "E2.6.23.0", {"start": v(192.5, 740.3) * mm, "end": v(167.5, 740.3) * mm});
            skLineSegment(sketch, "E2.6.23.1", {"start": v(192.5, 715.3) * mm, "end": v(192.5, 740.3) * mm});
            skLineSegment(sketch, "E2.6.23.2", {"start": v(192.5, 715.3) * mm, "end": v(167.5, 715.3) * mm});
            skLineSegment(sketch, "E2.6.23.3", {"start": v(167.5, 715.3) * mm, "end": v(167.5, 740.3) * mm});
            skLineSegment(sketch, "E2.6.24.0", {"start": v(192.5, 770.3) * mm, "end": v(167.5, 770.3) * mm});
            skLineSegment(sketch, "E2.6.24.1", {"start": v(192.5, 745.3) * mm, "end": v(192.5, 770.3) * mm});
            skLineSegment(sketch, "E2.6.24.2", {"start": v(192.5, 745.3) * mm, "end": v(167.5, 745.3) * mm});
            skLineSegment(sketch, "E2.6.24.3", {"start": v(167.5, 745.3) * mm, "end": v(167.5, 770.3) * mm});
            skLineSegment(sketch, "E2.6.25.0", {"start": v(192.5, 800.3) * mm, "end": v(167.5, 800.3) * mm});
            skLineSegment(sketch, "E2.6.25.1", {"start": v(192.5, 775.3) * mm, "end": v(192.5, 800.3) * mm});
            skLineSegment(sketch, "E2.6.25.2", {"start": v(192.5, 775.3) * mm, "end": v(167.5, 775.3) * mm});
            skLineSegment(sketch, "E2.6.25.3", {"start": v(167.5, 775.3) * mm, "end": v(167.5, 800.3) * mm});
            skLineSegment(sketch, "E2.6.26.0", {"start": v(192.5, 830.3) * mm, "end": v(167.5, 830.3) * mm});
            skLineSegment(sketch, "E2.6.26.1", {"start": v(192.5, 805.3) * mm, "end": v(192.5, 830.3) * mm});
            skLineSegment(sketch, "E2.6.26.2", {"start": v(192.5, 805.3) * mm, "end": v(167.5, 805.3) * mm});
            skLineSegment(sketch, "E2.6.26.3", {"start": v(167.5, 805.3) * mm, "end": v(167.5, 830.3) * mm});
            skLineSegment(sketch, "E2.6.27.0", {"start": v(192.5, 860.3) * mm, "end": v(167.5, 860.3) * mm});
            skLineSegment(sketch, "E2.6.27.1", {"start": v(192.5, 835.3) * mm, "end": v(192.5, 860.3) * mm});
            skLineSegment(sketch, "E2.6.27.2", {"start": v(192.5, 835.3) * mm, "end": v(167.5, 835.3) * mm});
            skLineSegment(sketch, "E2.6.27.3", {"start": v(167.5, 835.3) * mm, "end": v(167.5, 860.3) * mm});
            skLineSegment(sketch, "E2.6.28.0", {"start": v(192.5, 890.3) * mm, "end": v(167.5, 890.3) * mm});
            skLineSegment(sketch, "E2.6.28.1", {"start": v(192.5, 865.3) * mm, "end": v(192.5, 890.3) * mm});
            skLineSegment(sketch, "E2.6.28.2", {"start": v(192.5, 865.3) * mm, "end": v(167.5, 865.3) * mm});
            skLineSegment(sketch, "E2.6.28.3", {"start": v(167.5, 865.3) * mm, "end": v(167.5, 890.3) * mm});
            skLineSegment(sketch, "E2.6.29.0", {"start": v(192.5, 920.3) * mm, "end": v(167.5, 920.3) * mm});
            skLineSegment(sketch, "E2.6.29.1", {"start": v(192.5, 895.3) * mm, "end": v(192.5, 920.3) * mm});
            skLineSegment(sketch, "E2.6.29.2", {"start": v(192.5, 895.3) * mm, "end": v(167.5, 895.3) * mm});
            skLineSegment(sketch, "E2.6.29.3", {"start": v(167.5, 895.3) * mm, "end": v(167.5, 920.3) * mm});
            skLineSegment(sketch, "E2.6.30.0", {"start": v(192.5, 950.3) * mm, "end": v(167.5, 950.3) * mm});
            skLineSegment(sketch, "E2.6.30.1", {"start": v(192.5, 925.3) * mm, "end": v(192.5, 950.3) * mm});
            skLineSegment(sketch, "E2.6.30.2", {"start": v(192.5, 925.3) * mm, "end": v(167.5, 925.3) * mm});
            skLineSegment(sketch, "E2.6.30.3", {"start": v(167.5, 925.3) * mm, "end": v(167.5, 950.3) * mm});
            skLineSegment(sketch, "E2.7.0.0", {"start": v(222.5, 50.3) * mm, "end": v(197.5, 50.3) * mm});
            skLineSegment(sketch, "E2.7.0.1", {"start": v(222.5, 25.3) * mm, "end": v(222.5, 50.3) * mm});
            skLineSegment(sketch, "E2.7.0.2", {"start": v(222.5, 25.3) * mm, "end": v(197.5, 25.3) * mm});
            skLineSegment(sketch, "E2.7.0.3", {"start": v(197.5, 25.3) * mm, "end": v(197.5, 50.3) * mm});
            skLineSegment(sketch, "E2.7.1.0", {"start": v(222.5, 80.3) * mm, "end": v(197.5, 80.3) * mm});
            skLineSegment(sketch, "E2.7.1.1", {"start": v(222.5, 55.3) * mm, "end": v(222.5, 80.3) * mm});
            skLineSegment(sketch, "E2.7.1.2", {"start": v(222.5, 55.3) * mm, "end": v(197.5, 55.3) * mm});
            skLineSegment(sketch, "E2.7.1.3", {"start": v(197.5, 55.3) * mm, "end": v(197.5, 80.3) * mm});
            skLineSegment(sketch, "E2.7.2.0", {"start": v(222.5, 110.3) * mm, "end": v(197.5, 110.3) * mm});
            skLineSegment(sketch, "E2.7.2.1", {"start": v(222.5, 85.3) * mm, "end": v(222.5, 110.3) * mm});
            skLineSegment(sketch, "E2.7.2.2", {"start": v(222.5, 85.3) * mm, "end": v(197.5, 85.3) * mm});
            skLineSegment(sketch, "E2.7.2.3", {"start": v(197.5, 85.3) * mm, "end": v(197.5, 110.3) * mm});
            skLineSegment(sketch, "E2.7.3.0", {"start": v(222.5, 140.3) * mm, "end": v(197.5, 140.3) * mm});
            skLineSegment(sketch, "E2.7.3.1", {"start": v(222.5, 115.3) * mm, "end": v(222.5, 140.3) * mm});
            skLineSegment(sketch, "E2.7.3.2", {"start": v(222.5, 115.3) * mm, "end": v(197.5, 115.3) * mm});
            skLineSegment(sketch, "E2.7.3.3", {"start": v(197.5, 115.3) * mm, "end": v(197.5, 140.3) * mm});
            skLineSegment(sketch, "E2.7.4.0", {"start": v(222.5, 170.3) * mm, "end": v(197.5, 170.3) * mm});
            skLineSegment(sketch, "E2.7.4.1", {"start": v(222.5, 145.3) * mm, "end": v(222.5, 170.3) * mm});
            skLineSegment(sketch, "E2.7.4.2", {"start": v(222.5, 145.3) * mm, "end": v(197.5, 145.3) * mm});
            skLineSegment(sketch, "E2.7.4.3", {"start": v(197.5, 145.3) * mm, "end": v(197.5, 170.3) * mm});
            skLineSegment(sketch, "E2.7.5.0", {"start": v(222.5, 200.3) * mm, "end": v(197.5, 200.3) * mm});
            skLineSegment(sketch, "E2.7.5.1", {"start": v(222.5, 175.3) * mm, "end": v(222.5, 200.3) * mm});
            skLineSegment(sketch, "E2.7.5.2", {"start": v(222.5, 175.3) * mm, "end": v(197.5, 175.3) * mm});
            skLineSegment(sketch, "E2.7.5.3", {"start": v(197.5, 175.3) * mm, "end": v(197.5, 200.3) * mm});
            skLineSegment(sketch, "E2.7.6.0", {"start": v(222.5, 230.3) * mm, "end": v(197.5, 230.3) * mm});
            skLineSegment(sketch, "E2.7.6.1", {"start": v(222.5, 205.3) * mm, "end": v(222.5, 230.3) * mm});
            skLineSegment(sketch, "E2.7.6.2", {"start": v(222.5, 205.3) * mm, "end": v(197.5, 205.3) * mm});
            skLineSegment(sketch, "E2.7.6.3", {"start": v(197.5, 205.3) * mm, "end": v(197.5, 230.3) * mm});
            skLineSegment(sketch, "E2.7.7.0", {"start": v(222.5, 260.3) * mm, "end": v(197.5, 260.3) * mm});
            skLineSegment(sketch, "E2.7.7.1", {"start": v(222.5, 235.3) * mm, "end": v(222.5, 260.3) * mm});
            skLineSegment(sketch, "E2.7.7.2", {"start": v(222.5, 235.3) * mm, "end": v(197.5, 235.3) * mm});
            skLineSegment(sketch, "E2.7.7.3", {"start": v(197.5, 235.3) * mm, "end": v(197.5, 260.3) * mm});
            skLineSegment(sketch, "E2.7.8.0", {"start": v(222.5, 290.3) * mm, "end": v(197.5, 290.3) * mm});
            skLineSegment(sketch, "E2.7.8.1", {"start": v(222.5, 265.3) * mm, "end": v(222.5, 290.3) * mm});
            skLineSegment(sketch, "E2.7.8.2", {"start": v(222.5, 265.3) * mm, "end": v(197.5, 265.3) * mm});
            skLineSegment(sketch, "E2.7.8.3", {"start": v(197.5, 265.3) * mm, "end": v(197.5, 290.3) * mm});
            skLineSegment(sketch, "E2.7.9.0", {"start": v(222.5, 320.3) * mm, "end": v(197.5, 320.3) * mm});
            skLineSegment(sketch, "E2.7.9.1", {"start": v(222.5, 295.3) * mm, "end": v(222.5, 320.3) * mm});
            skLineSegment(sketch, "E2.7.9.2", {"start": v(222.5, 295.3) * mm, "end": v(197.5, 295.3) * mm});
            skLineSegment(sketch, "E2.7.9.3", {"start": v(197.5, 295.3) * mm, "end": v(197.5, 320.3) * mm});
            skLineSegment(sketch, "E2.7.10.0", {"start": v(222.5, 350.3) * mm, "end": v(197.5, 350.3) * mm});
            skLineSegment(sketch, "E2.7.10.1", {"start": v(222.5, 325.3) * mm, "end": v(222.5, 350.3) * mm});
            skLineSegment(sketch, "E2.7.10.2", {"start": v(222.5, 325.3) * mm, "end": v(197.5, 325.3) * mm});
            skLineSegment(sketch, "E2.7.10.3", {"start": v(197.5, 325.3) * mm, "end": v(197.5, 350.3) * mm});
            skLineSegment(sketch, "E2.7.11.0", {"start": v(222.5, 380.3) * mm, "end": v(197.5, 380.3) * mm});
            skLineSegment(sketch, "E2.7.11.1", {"start": v(222.5, 355.3) * mm, "end": v(222.5, 380.3) * mm});
            skLineSegment(sketch, "E2.7.11.2", {"start": v(222.5, 355.3) * mm, "end": v(197.5, 355.3) * mm});
            skLineSegment(sketch, "E2.7.11.3", {"start": v(197.5, 355.3) * mm, "end": v(197.5, 380.3) * mm});
            skLineSegment(sketch, "E2.7.12.0", {"start": v(222.5, 410.3) * mm, "end": v(197.5, 410.3) * mm});
            skLineSegment(sketch, "E2.7.12.1", {"start": v(222.5, 385.3) * mm, "end": v(222.5, 410.3) * mm});
            skLineSegment(sketch, "E2.7.12.2", {"start": v(222.5, 385.3) * mm, "end": v(197.5, 385.3) * mm});
            skLineSegment(sketch, "E2.7.12.3", {"start": v(197.5, 385.3) * mm, "end": v(197.5, 410.3) * mm});
            skLineSegment(sketch, "E2.7.13.0", {"start": v(222.5, 440.3) * mm, "end": v(197.5, 440.3) * mm});
            skLineSegment(sketch, "E2.7.13.1", {"start": v(222.5, 415.3) * mm, "end": v(222.5, 440.3) * mm});
            skLineSegment(sketch, "E2.7.13.2", {"start": v(222.5, 415.3) * mm, "end": v(197.5, 415.3) * mm});
            skLineSegment(sketch, "E2.7.13.3", {"start": v(197.5, 415.3) * mm, "end": v(197.5, 440.3) * mm});
            skLineSegment(sketch, "E2.7.14.0", {"start": v(222.5, 470.3) * mm, "end": v(197.5, 470.3) * mm});
            skLineSegment(sketch, "E2.7.14.1", {"start": v(222.5, 445.3) * mm, "end": v(222.5, 470.3) * mm});
            skLineSegment(sketch, "E2.7.14.2", {"start": v(222.5, 445.3) * mm, "end": v(197.5, 445.3) * mm});
            skLineSegment(sketch, "E2.7.14.3", {"start": v(197.5, 445.3) * mm, "end": v(197.5, 470.3) * mm});
            skLineSegment(sketch, "E2.7.15.0", {"start": v(222.5, 500.3) * mm, "end": v(197.5, 500.3) * mm});
            skLineSegment(sketch, "E2.7.15.1", {"start": v(222.5, 475.3) * mm, "end": v(222.5, 500.3) * mm});
            skLineSegment(sketch, "E2.7.15.2", {"start": v(222.5, 475.3) * mm, "end": v(197.5, 475.3) * mm});
            skLineSegment(sketch, "E2.7.15.3", {"start": v(197.5, 475.3) * mm, "end": v(197.5, 500.3) * mm});
            skLineSegment(sketch, "E2.7.16.0", {"start": v(222.5, 530.3) * mm, "end": v(197.5, 530.3) * mm});
            skLineSegment(sketch, "E2.7.16.1", {"start": v(222.5, 505.3) * mm, "end": v(222.5, 530.3) * mm});
            skLineSegment(sketch, "E2.7.16.2", {"start": v(222.5, 505.3) * mm, "end": v(197.5, 505.3) * mm});
            skLineSegment(sketch, "E2.7.16.3", {"start": v(197.5, 505.3) * mm, "end": v(197.5, 530.3) * mm});
            skLineSegment(sketch, "E2.7.17.0", {"start": v(222.5, 560.3) * mm, "end": v(197.5, 560.3) * mm});
            skLineSegment(sketch, "E2.7.17.1", {"start": v(222.5, 535.3) * mm, "end": v(222.5, 560.3) * mm});
            skLineSegment(sketch, "E2.7.17.2", {"start": v(222.5, 535.3) * mm, "end": v(197.5, 535.3) * mm});
            skLineSegment(sketch, "E2.7.17.3", {"start": v(197.5, 535.3) * mm, "end": v(197.5, 560.3) * mm});
            skLineSegment(sketch, "E2.7.18.0", {"start": v(222.5, 590.3) * mm, "end": v(197.5, 590.3) * mm});
            skLineSegment(sketch, "E2.7.18.1", {"start": v(222.5, 565.3) * mm, "end": v(222.5, 590.3) * mm});
            skLineSegment(sketch, "E2.7.18.2", {"start": v(222.5, 565.3) * mm, "end": v(197.5, 565.3) * mm});
            skLineSegment(sketch, "E2.7.18.3", {"start": v(197.5, 565.3) * mm, "end": v(197.5, 590.3) * mm});
            skLineSegment(sketch, "E2.7.19.0", {"start": v(222.5, 620.3) * mm, "end": v(197.5, 620.3) * mm});
            skLineSegment(sketch, "E2.7.19.1", {"start": v(222.5, 595.3) * mm, "end": v(222.5, 620.3) * mm});
            skLineSegment(sketch, "E2.7.19.2", {"start": v(222.5, 595.3) * mm, "end": v(197.5, 595.3) * mm});
            skLineSegment(sketch, "E2.7.19.3", {"start": v(197.5, 595.3) * mm, "end": v(197.5, 620.3) * mm});
            skLineSegment(sketch, "E2.7.20.0", {"start": v(222.5, 650.3) * mm, "end": v(197.5, 650.3) * mm});
            skLineSegment(sketch, "E2.7.20.1", {"start": v(222.5, 625.3) * mm, "end": v(222.5, 650.3) * mm});
            skLineSegment(sketch, "E2.7.20.2", {"start": v(222.5, 625.3) * mm, "end": v(197.5, 625.3) * mm});
            skLineSegment(sketch, "E2.7.20.3", {"start": v(197.5, 625.3) * mm, "end": v(197.5, 650.3) * mm});
            skLineSegment(sketch, "E2.7.21.0", {"start": v(222.5, 680.3) * mm, "end": v(197.5, 680.3) * mm});
            skLineSegment(sketch, "E2.7.21.1", {"start": v(222.5, 655.3) * mm, "end": v(222.5, 680.3) * mm});
            skLineSegment(sketch, "E2.7.21.2", {"start": v(222.5, 655.3) * mm, "end": v(197.5, 655.3) * mm});
            skLineSegment(sketch, "E2.7.21.3", {"start": v(197.5, 655.3) * mm, "end": v(197.5, 680.3) * mm});
            skLineSegment(sketch, "E2.7.22.0", {"start": v(222.5, 710.3) * mm, "end": v(197.5, 710.3) * mm});
            skLineSegment(sketch, "E2.7.22.1", {"start": v(222.5, 685.3) * mm, "end": v(222.5, 710.3) * mm});
            skLineSegment(sketch, "E2.7.22.2", {"start": v(222.5, 685.3) * mm, "end": v(197.5, 685.3) * mm});
            skLineSegment(sketch, "E2.7.22.3", {"start": v(197.5, 685.3) * mm, "end": v(197.5, 710.3) * mm});
            skLineSegment(sketch, "E2.7.23.0", {"start": v(222.5, 740.3) * mm, "end": v(197.5, 740.3) * mm});
            skLineSegment(sketch, "E2.7.23.1", {"start": v(222.5, 715.3) * mm, "end": v(222.5, 740.3) * mm});
            skLineSegment(sketch, "E2.7.23.2", {"start": v(222.5, 715.3) * mm, "end": v(197.5, 715.3) * mm});
            skLineSegment(sketch, "E2.7.23.3", {"start": v(197.5, 715.3) * mm, "end": v(197.5, 740.3) * mm});
            skLineSegment(sketch, "E2.7.24.0", {"start": v(222.5, 770.3) * mm, "end": v(197.5, 770.3) * mm});
            skLineSegment(sketch, "E2.7.24.1", {"start": v(222.5, 745.3) * mm, "end": v(222.5, 770.3) * mm});
            skLineSegment(sketch, "E2.7.24.2", {"start": v(222.5, 745.3) * mm, "end": v(197.5, 745.3) * mm});
            skLineSegment(sketch, "E2.7.24.3", {"start": v(197.5, 745.3) * mm, "end": v(197.5, 770.3) * mm});
            skLineSegment(sketch, "E2.7.25.0", {"start": v(222.5, 800.3) * mm, "end": v(197.5, 800.3) * mm});
            skLineSegment(sketch, "E2.7.25.1", {"start": v(222.5, 775.3) * mm, "end": v(222.5, 800.3) * mm});
            skLineSegment(sketch, "E2.7.25.2", {"start": v(222.5, 775.3) * mm, "end": v(197.5, 775.3) * mm});
            skLineSegment(sketch, "E2.7.25.3", {"start": v(197.5, 775.3) * mm, "end": v(197.5, 800.3) * mm});
            skLineSegment(sketch, "E2.7.26.0", {"start": v(222.5, 830.3) * mm, "end": v(197.5, 830.3) * mm});
            skLineSegment(sketch, "E2.7.26.1", {"start": v(222.5, 805.3) * mm, "end": v(222.5, 830.3) * mm});
            skLineSegment(sketch, "E2.7.26.2", {"start": v(222.5, 805.3) * mm, "end": v(197.5, 805.3) * mm});
            skLineSegment(sketch, "E2.7.26.3", {"start": v(197.5, 805.3) * mm, "end": v(197.5, 830.3) * mm});
            skLineSegment(sketch, "E2.7.27.0", {"start": v(222.5, 860.3) * mm, "end": v(197.5, 860.3) * mm});
            skLineSegment(sketch, "E2.7.27.1", {"start": v(222.5, 835.3) * mm, "end": v(222.5, 860.3) * mm});
            skLineSegment(sketch, "E2.7.27.2", {"start": v(222.5, 835.3) * mm, "end": v(197.5, 835.3) * mm});
            skLineSegment(sketch, "E2.7.27.3", {"start": v(197.5, 835.3) * mm, "end": v(197.5, 860.3) * mm});
            skLineSegment(sketch, "E2.7.28.0", {"start": v(222.5, 890.3) * mm, "end": v(197.5, 890.3) * mm});
            skLineSegment(sketch, "E2.7.28.1", {"start": v(222.5, 865.3) * mm, "end": v(222.5, 890.3) * mm});
            skLineSegment(sketch, "E2.7.28.2", {"start": v(222.5, 865.3) * mm, "end": v(197.5, 865.3) * mm});
            skLineSegment(sketch, "E2.7.28.3", {"start": v(197.5, 865.3) * mm, "end": v(197.5, 890.3) * mm});
            skLineSegment(sketch, "E2.7.29.0", {"start": v(222.5, 920.3) * mm, "end": v(197.5, 920.3) * mm});
            skLineSegment(sketch, "E2.7.29.1", {"start": v(222.5, 895.3) * mm, "end": v(222.5, 920.3) * mm});
            skLineSegment(sketch, "E2.7.29.2", {"start": v(222.5, 895.3) * mm, "end": v(197.5, 895.3) * mm});
            skLineSegment(sketch, "E2.7.29.3", {"start": v(197.5, 895.3) * mm, "end": v(197.5, 920.3) * mm});
            skLineSegment(sketch, "E2.7.30.0", {"start": v(222.5, 950.3) * mm, "end": v(197.5, 950.3) * mm});
            skLineSegment(sketch, "E2.7.30.1", {"start": v(222.5, 925.3) * mm, "end": v(222.5, 950.3) * mm});
            skLineSegment(sketch, "E2.7.30.2", {"start": v(222.5, 925.3) * mm, "end": v(197.5, 925.3) * mm});
            skLineSegment(sketch, "E2.7.30.3", {"start": v(197.5, 925.3) * mm, "end": v(197.5, 950.3) * mm});
            skLineSegment(sketch, "E2.8.0.0", {"start": v(252.5, 50.3) * mm, "end": v(227.5, 50.3) * mm});
            skLineSegment(sketch, "E2.8.0.1", {"start": v(252.5, 25.3) * mm, "end": v(252.5, 50.3) * mm});
            skLineSegment(sketch, "E2.8.0.2", {"start": v(252.5, 25.3) * mm, "end": v(227.5, 25.3) * mm});
            skLineSegment(sketch, "E2.8.0.3", {"start": v(227.5, 25.3) * mm, "end": v(227.5, 50.3) * mm});
            skLineSegment(sketch, "E2.8.1.0", {"start": v(252.5, 80.3) * mm, "end": v(227.5, 80.3) * mm});
            skLineSegment(sketch, "E2.8.1.1", {"start": v(252.5, 55.3) * mm, "end": v(252.5, 80.3) * mm});
            skLineSegment(sketch, "E2.8.1.2", {"start": v(252.5, 55.3) * mm, "end": v(227.5, 55.3) * mm});
            skLineSegment(sketch, "E2.8.1.3", {"start": v(227.5, 55.3) * mm, "end": v(227.5, 80.3) * mm});
            skLineSegment(sketch, "E2.8.2.0", {"start": v(252.5, 110.3) * mm, "end": v(227.5, 110.3) * mm});
            skLineSegment(sketch, "E2.8.2.1", {"start": v(252.5, 85.3) * mm, "end": v(252.5, 110.3) * mm});
            skLineSegment(sketch, "E2.8.2.2", {"start": v(252.5, 85.3) * mm, "end": v(227.5, 85.3) * mm});
            skLineSegment(sketch, "E2.8.2.3", {"start": v(227.5, 85.3) * mm, "end": v(227.5, 110.3) * mm});
            skLineSegment(sketch, "E2.8.3.0", {"start": v(252.5, 140.3) * mm, "end": v(227.5, 140.3) * mm});
            skLineSegment(sketch, "E2.8.3.1", {"start": v(252.5, 115.3) * mm, "end": v(252.5, 140.3) * mm});
            skLineSegment(sketch, "E2.8.3.2", {"start": v(252.5, 115.3) * mm, "end": v(227.5, 115.3) * mm});
            skLineSegment(sketch, "E2.8.3.3", {"start": v(227.5, 115.3) * mm, "end": v(227.5, 140.3) * mm});
            skLineSegment(sketch, "E2.8.4.0", {"start": v(252.5, 170.3) * mm, "end": v(227.5, 170.3) * mm});
            skLineSegment(sketch, "E2.8.4.1", {"start": v(252.5, 145.3) * mm, "end": v(252.5, 170.3) * mm});
            skLineSegment(sketch, "E2.8.4.2", {"start": v(252.5, 145.3) * mm, "end": v(227.5, 145.3) * mm});
            skLineSegment(sketch, "E2.8.4.3", {"start": v(227.5, 145.3) * mm, "end": v(227.5, 170.3) * mm});
            skLineSegment(sketch, "E2.8.5.0", {"start": v(252.5, 200.3) * mm, "end": v(227.5, 200.3) * mm});
            skLineSegment(sketch, "E2.8.5.1", {"start": v(252.5, 175.3) * mm, "end": v(252.5, 200.3) * mm});
            skLineSegment(sketch, "E2.8.5.2", {"start": v(252.5, 175.3) * mm, "end": v(227.5, 175.3) * mm});
            skLineSegment(sketch, "E2.8.5.3", {"start": v(227.5, 175.3) * mm, "end": v(227.5, 200.3) * mm});
            skLineSegment(sketch, "E2.8.6.0", {"start": v(252.5, 230.3) * mm, "end": v(227.5, 230.3) * mm});
            skLineSegment(sketch, "E2.8.6.1", {"start": v(252.5, 205.3) * mm, "end": v(252.5, 230.3) * mm});
            skLineSegment(sketch, "E2.8.6.2", {"start": v(252.5, 205.3) * mm, "end": v(227.5, 205.3) * mm});
            skLineSegment(sketch, "E2.8.6.3", {"start": v(227.5, 205.3) * mm, "end": v(227.5, 230.3) * mm});
            skLineSegment(sketch, "E2.8.7.0", {"start": v(252.5, 260.3) * mm, "end": v(227.5, 260.3) * mm});
            skLineSegment(sketch, "E2.8.7.1", {"start": v(252.5, 235.3) * mm, "end": v(252.5, 260.3) * mm});
            skLineSegment(sketch, "E2.8.7.2", {"start": v(252.5, 235.3) * mm, "end": v(227.5, 235.3) * mm});
            skLineSegment(sketch, "E2.8.7.3", {"start": v(227.5, 235.3) * mm, "end": v(227.5, 260.3) * mm});
            skLineSegment(sketch, "E2.8.8.0", {"start": v(252.5, 290.3) * mm, "end": v(227.5, 290.3) * mm});
            skLineSegment(sketch, "E2.8.8.1", {"start": v(252.5, 265.3) * mm, "end": v(252.5, 290.3) * mm});
            skLineSegment(sketch, "E2.8.8.2", {"start": v(252.5, 265.3) * mm, "end": v(227.5, 265.3) * mm});
            skLineSegment(sketch, "E2.8.8.3", {"start": v(227.5, 265.3) * mm, "end": v(227.5, 290.3) * mm});
            skLineSegment(sketch, "E2.8.9.0", {"start": v(252.5, 320.3) * mm, "end": v(227.5, 320.3) * mm});
            skLineSegment(sketch, "E2.8.9.1", {"start": v(252.5, 295.3) * mm, "end": v(252.5, 320.3) * mm});
            skLineSegment(sketch, "E2.8.9.2", {"start": v(252.5, 295.3) * mm, "end": v(227.5, 295.3) * mm});
            skLineSegment(sketch, "E2.8.9.3", {"start": v(227.5, 295.3) * mm, "end": v(227.5, 320.3) * mm});
            skLineSegment(sketch, "E2.8.10.0", {"start": v(252.5, 350.3) * mm, "end": v(227.5, 350.3) * mm});
            skLineSegment(sketch, "E2.8.10.1", {"start": v(252.5, 325.3) * mm, "end": v(252.5, 350.3) * mm});
            skLineSegment(sketch, "E2.8.10.2", {"start": v(252.5, 325.3) * mm, "end": v(227.5, 325.3) * mm});
            skLineSegment(sketch, "E2.8.10.3", {"start": v(227.5, 325.3) * mm, "end": v(227.5, 350.3) * mm});
            skLineSegment(sketch, "E2.8.11.0", {"start": v(252.5, 380.3) * mm, "end": v(227.5, 380.3) * mm});
            skLineSegment(sketch, "E2.8.11.1", {"start": v(252.5, 355.3) * mm, "end": v(252.5, 380.3) * mm});
            skLineSegment(sketch, "E2.8.11.2", {"start": v(252.5, 355.3) * mm, "end": v(227.5, 355.3) * mm});
            skLineSegment(sketch, "E2.8.11.3", {"start": v(227.5, 355.3) * mm, "end": v(227.5, 380.3) * mm});
            skLineSegment(sketch, "E2.8.12.0", {"start": v(252.5, 410.3) * mm, "end": v(227.5, 410.3) * mm});
            skLineSegment(sketch, "E2.8.12.1", {"start": v(252.5, 385.3) * mm, "end": v(252.5, 410.3) * mm});
            skLineSegment(sketch, "E2.8.12.2", {"start": v(252.5, 385.3) * mm, "end": v(227.5, 385.3) * mm});
            skLineSegment(sketch, "E2.8.12.3", {"start": v(227.5, 385.3) * mm, "end": v(227.5, 410.3) * mm});
            skLineSegment(sketch, "E2.8.13.0", {"start": v(252.5, 440.3) * mm, "end": v(227.5, 440.3) * mm});
            skLineSegment(sketch, "E2.8.13.1", {"start": v(252.5, 415.3) * mm, "end": v(252.5, 440.3) * mm});
            skLineSegment(sketch, "E2.8.13.2", {"start": v(252.5, 415.3) * mm, "end": v(227.5, 415.3) * mm});
            skLineSegment(sketch, "E2.8.13.3", {"start": v(227.5, 415.3) * mm, "end": v(227.5, 440.3) * mm});
            skLineSegment(sketch, "E2.8.14.0", {"start": v(252.5, 470.3) * mm, "end": v(227.5, 470.3) * mm});
            skLineSegment(sketch, "E2.8.14.1", {"start": v(252.5, 445.3) * mm, "end": v(252.5, 470.3) * mm});
            skLineSegment(sketch, "E2.8.14.2", {"start": v(252.5, 445.3) * mm, "end": v(227.5, 445.3) * mm});
            skLineSegment(sketch, "E2.8.14.3", {"start": v(227.5, 445.3) * mm, "end": v(227.5, 470.3) * mm});
            skLineSegment(sketch, "E2.8.15.0", {"start": v(252.5, 500.3) * mm, "end": v(227.5, 500.3) * mm});
            skLineSegment(sketch, "E2.8.15.1", {"start": v(252.5, 475.3) * mm, "end": v(252.5, 500.3) * mm});
            skLineSegment(sketch, "E2.8.15.2", {"start": v(252.5, 475.3) * mm, "end": v(227.5, 475.3) * mm});
            skLineSegment(sketch, "E2.8.15.3", {"start": v(227.5, 475.3) * mm, "end": v(227.5, 500.3) * mm});
            skLineSegment(sketch, "E2.8.16.0", {"start": v(252.5, 530.3) * mm, "end": v(227.5, 530.3) * mm});
            skLineSegment(sketch, "E2.8.16.1", {"start": v(252.5, 505.3) * mm, "end": v(252.5, 530.3) * mm});
            skLineSegment(sketch, "E2.8.16.2", {"start": v(252.5, 505.3) * mm, "end": v(227.5, 505.3) * mm});
            skLineSegment(sketch, "E2.8.16.3", {"start": v(227.5, 505.3) * mm, "end": v(227.5, 530.3) * mm});
            skLineSegment(sketch, "E2.8.17.0", {"start": v(252.5, 560.3) * mm, "end": v(227.5, 560.3) * mm});
            skLineSegment(sketch, "E2.8.17.1", {"start": v(252.5, 535.3) * mm, "end": v(252.5, 560.3) * mm});
            skLineSegment(sketch, "E2.8.17.2", {"start": v(252.5, 535.3) * mm, "end": v(227.5, 535.3) * mm});
            skLineSegment(sketch, "E2.8.17.3", {"start": v(227.5, 535.3) * mm, "end": v(227.5, 560.3) * mm});
            skLineSegment(sketch, "E2.8.18.0", {"start": v(252.5, 590.3) * mm, "end": v(227.5, 590.3) * mm});
            skLineSegment(sketch, "E2.8.18.1", {"start": v(252.5, 565.3) * mm, "end": v(252.5, 590.3) * mm});
            skLineSegment(sketch, "E2.8.18.2", {"start": v(252.5, 565.3) * mm, "end": v(227.5, 565.3) * mm});
            skLineSegment(sketch, "E2.8.18.3", {"start": v(227.5, 565.3) * mm, "end": v(227.5, 590.3) * mm});
            skLineSegment(sketch, "E2.8.19.0", {"start": v(252.5, 620.3) * mm, "end": v(227.5, 620.3) * mm});
            skLineSegment(sketch, "E2.8.19.1", {"start": v(252.5, 595.3) * mm, "end": v(252.5, 620.3) * mm});
            skLineSegment(sketch, "E2.8.19.2", {"start": v(252.5, 595.3) * mm, "end": v(227.5, 595.3) * mm});
            skLineSegment(sketch, "E2.8.19.3", {"start": v(227.5, 595.3) * mm, "end": v(227.5, 620.3) * mm});
            skLineSegment(sketch, "E2.8.20.0", {"start": v(252.5, 650.3) * mm, "end": v(227.5, 650.3) * mm});
            skLineSegment(sketch, "E2.8.20.1", {"start": v(252.5, 625.3) * mm, "end": v(252.5, 650.3) * mm});
            skLineSegment(sketch, "E2.8.20.2", {"start": v(252.5, 625.3) * mm, "end": v(227.5, 625.3) * mm});
            skLineSegment(sketch, "E2.8.20.3", {"start": v(227.5, 625.3) * mm, "end": v(227.5, 650.3) * mm});
            skLineSegment(sketch, "E2.8.21.0", {"start": v(252.5, 680.3) * mm, "end": v(227.5, 680.3) * mm});
            skLineSegment(sketch, "E2.8.21.1", {"start": v(252.5, 655.3) * mm, "end": v(252.5, 680.3) * mm});
            skLineSegment(sketch, "E2.8.21.2", {"start": v(252.5, 655.3) * mm, "end": v(227.5, 655.3) * mm});
            skLineSegment(sketch, "E2.8.21.3", {"start": v(227.5, 655.3) * mm, "end": v(227.5, 680.3) * mm});
            skLineSegment(sketch, "E2.8.22.0", {"start": v(252.5, 710.3) * mm, "end": v(227.5, 710.3) * mm});
            skLineSegment(sketch, "E2.8.22.1", {"start": v(252.5, 685.3) * mm, "end": v(252.5, 710.3) * mm});
            skLineSegment(sketch, "E2.8.22.2", {"start": v(252.5, 685.3) * mm, "end": v(227.5, 685.3) * mm});
            skLineSegment(sketch, "E2.8.22.3", {"start": v(227.5, 685.3) * mm, "end": v(227.5, 710.3) * mm});
            skLineSegment(sketch, "E2.8.23.0", {"start": v(252.5, 740.3) * mm, "end": v(227.5, 740.3) * mm});
            skLineSegment(sketch, "E2.8.23.1", {"start": v(252.5, 715.3) * mm, "end": v(252.5, 740.3) * mm});
            skLineSegment(sketch, "E2.8.23.2", {"start": v(252.5, 715.3) * mm, "end": v(227.5, 715.3) * mm});
            skLineSegment(sketch, "E2.8.23.3", {"start": v(227.5, 715.3) * mm, "end": v(227.5, 740.3) * mm});
            skLineSegment(sketch, "E2.8.24.0", {"start": v(252.5, 770.3) * mm, "end": v(227.5, 770.3) * mm});
            skLineSegment(sketch, "E2.8.24.1", {"start": v(252.5, 745.3) * mm, "end": v(252.5, 770.3) * mm});
            skLineSegment(sketch, "E2.8.24.2", {"start": v(252.5, 745.3) * mm, "end": v(227.5, 745.3) * mm});
            skLineSegment(sketch, "E2.8.24.3", {"start": v(227.5, 745.3) * mm, "end": v(227.5, 770.3) * mm});
            skLineSegment(sketch, "E2.8.25.0", {"start": v(252.5, 800.3) * mm, "end": v(227.5, 800.3) * mm});
            skLineSegment(sketch, "E2.8.25.1", {"start": v(252.5, 775.3) * mm, "end": v(252.5, 800.3) * mm});
            skLineSegment(sketch, "E2.8.25.2", {"start": v(252.5, 775.3) * mm, "end": v(227.5, 775.3) * mm});
            skLineSegment(sketch, "E2.8.25.3", {"start": v(227.5, 775.3) * mm, "end": v(227.5, 800.3) * mm});
            skLineSegment(sketch, "E2.8.26.0", {"start": v(252.5, 830.3) * mm, "end": v(227.5, 830.3) * mm});
            skLineSegment(sketch, "E2.8.26.1", {"start": v(252.5, 805.3) * mm, "end": v(252.5, 830.3) * mm});
            skLineSegment(sketch, "E2.8.26.2", {"start": v(252.5, 805.3) * mm, "end": v(227.5, 805.3) * mm});
            skLineSegment(sketch, "E2.8.26.3", {"start": v(227.5, 805.3) * mm, "end": v(227.5, 830.3) * mm});
            skLineSegment(sketch, "E2.8.27.0", {"start": v(252.5, 860.3) * mm, "end": v(227.5, 860.3) * mm});
            skLineSegment(sketch, "E2.8.27.1", {"start": v(252.5, 835.3) * mm, "end": v(252.5, 860.3) * mm});
            skLineSegment(sketch, "E2.8.27.2", {"start": v(252.5, 835.3) * mm, "end": v(227.5, 835.3) * mm});
            skLineSegment(sketch, "E2.8.27.3", {"start": v(227.5, 835.3) * mm, "end": v(227.5, 860.3) * mm});
            skLineSegment(sketch, "E2.8.28.0", {"start": v(252.5, 890.3) * mm, "end": v(227.5, 890.3) * mm});
            skLineSegment(sketch, "E2.8.28.1", {"start": v(252.5, 865.3) * mm, "end": v(252.5, 890.3) * mm});
            skLineSegment(sketch, "E2.8.28.2", {"start": v(252.5, 865.3) * mm, "end": v(227.5, 865.3) * mm});
            skLineSegment(sketch, "E2.8.28.3", {"start": v(227.5, 865.3) * mm, "end": v(227.5, 890.3) * mm});
            skLineSegment(sketch, "E2.8.29.0", {"start": v(252.5, 920.3) * mm, "end": v(227.5, 920.3) * mm});
            skLineSegment(sketch, "E2.8.29.1", {"start": v(252.5, 895.3) * mm, "end": v(252.5, 920.3) * mm});
            skLineSegment(sketch, "E2.8.29.2", {"start": v(252.5, 895.3) * mm, "end": v(227.5, 895.3) * mm});
            skLineSegment(sketch, "E2.8.29.3", {"start": v(227.5, 895.3) * mm, "end": v(227.5, 920.3) * mm});
            skLineSegment(sketch, "E2.8.30.0", {"start": v(252.5, 950.3) * mm, "end": v(227.5, 950.3) * mm});
            skLineSegment(sketch, "E2.8.30.1", {"start": v(252.5, 925.3) * mm, "end": v(252.5, 950.3) * mm});
            skLineSegment(sketch, "E2.8.30.2", {"start": v(252.5, 925.3) * mm, "end": v(227.5, 925.3) * mm});
            skLineSegment(sketch, "E2.8.30.3", {"start": v(227.5, 925.3) * mm, "end": v(227.5, 950.3) * mm});
            skLineSegment(sketch, "E2.9.0.0", {"start": v(282.5, 50.3) * mm, "end": v(257.5, 50.3) * mm});
            skLineSegment(sketch, "E2.9.0.1", {"start": v(282.5, 25.3) * mm, "end": v(282.5, 50.3) * mm});
            skLineSegment(sketch, "E2.9.0.2", {"start": v(282.5, 25.3) * mm, "end": v(257.5, 25.3) * mm});
            skLineSegment(sketch, "E2.9.0.3", {"start": v(257.5, 25.3) * mm, "end": v(257.5, 50.3) * mm});
            skLineSegment(sketch, "E2.9.1.0", {"start": v(282.5, 80.3) * mm, "end": v(257.5, 80.3) * mm});
            skLineSegment(sketch, "E2.9.1.1", {"start": v(282.5, 55.3) * mm, "end": v(282.5, 80.3) * mm});
            skLineSegment(sketch, "E2.9.1.2", {"start": v(282.5, 55.3) * mm, "end": v(257.5, 55.3) * mm});
            skLineSegment(sketch, "E2.9.1.3", {"start": v(257.5, 55.3) * mm, "end": v(257.5, 80.3) * mm});
            skLineSegment(sketch, "E2.9.2.0", {"start": v(282.5, 110.3) * mm, "end": v(257.5, 110.3) * mm});
            skLineSegment(sketch, "E2.9.2.1", {"start": v(282.5, 85.3) * mm, "end": v(282.5, 110.3) * mm});
            skLineSegment(sketch, "E2.9.2.2", {"start": v(282.5, 85.3) * mm, "end": v(257.5, 85.3) * mm});
            skLineSegment(sketch, "E2.9.2.3", {"start": v(257.5, 85.3) * mm, "end": v(257.5, 110.3) * mm});
            skLineSegment(sketch, "E2.9.3.0", {"start": v(282.5, 140.3) * mm, "end": v(257.5, 140.3) * mm});
            skLineSegment(sketch, "E2.9.3.1", {"start": v(282.5, 115.3) * mm, "end": v(282.5, 140.3) * mm});
            skLineSegment(sketch, "E2.9.3.2", {"start": v(282.5, 115.3) * mm, "end": v(257.5, 115.3) * mm});
            skLineSegment(sketch, "E2.9.3.3", {"start": v(257.5, 115.3) * mm, "end": v(257.5, 140.3) * mm});
            skLineSegment(sketch, "E2.9.4.0", {"start": v(282.5, 170.3) * mm, "end": v(257.5, 170.3) * mm});
            skLineSegment(sketch, "E2.9.4.1", {"start": v(282.5, 145.3) * mm, "end": v(282.5, 170.3) * mm});
            skLineSegment(sketch, "E2.9.4.2", {"start": v(282.5, 145.3) * mm, "end": v(257.5, 145.3) * mm});
            skLineSegment(sketch, "E2.9.4.3", {"start": v(257.5, 145.3) * mm, "end": v(257.5, 170.3) * mm});
            skLineSegment(sketch, "E2.9.5.0", {"start": v(282.5, 200.3) * mm, "end": v(257.5, 200.3) * mm});
            skLineSegment(sketch, "E2.9.5.1", {"start": v(282.5, 175.3) * mm, "end": v(282.5, 200.3) * mm});
            skLineSegment(sketch, "E2.9.5.2", {"start": v(282.5, 175.3) * mm, "end": v(257.5, 175.3) * mm});
            skLineSegment(sketch, "E2.9.5.3", {"start": v(257.5, 175.3) * mm, "end": v(257.5, 200.3) * mm});
            skLineSegment(sketch, "E2.9.6.0", {"start": v(282.5, 230.3) * mm, "end": v(257.5, 230.3) * mm});
            skLineSegment(sketch, "E2.9.6.1", {"start": v(282.5, 205.3) * mm, "end": v(282.5, 230.3) * mm});
            skLineSegment(sketch, "E2.9.6.2", {"start": v(282.5, 205.3) * mm, "end": v(257.5, 205.3) * mm});
            skLineSegment(sketch, "E2.9.6.3", {"start": v(257.5, 205.3) * mm, "end": v(257.5, 230.3) * mm});
            skLineSegment(sketch, "E2.9.7.0", {"start": v(282.5, 260.3) * mm, "end": v(257.5, 260.3) * mm});
            skLineSegment(sketch, "E2.9.7.1", {"start": v(282.5, 235.3) * mm, "end": v(282.5, 260.3) * mm});
            skLineSegment(sketch, "E2.9.7.2", {"start": v(282.5, 235.3) * mm, "end": v(257.5, 235.3) * mm});
            skLineSegment(sketch, "E2.9.7.3", {"start": v(257.5, 235.3) * mm, "end": v(257.5, 260.3) * mm});
            skLineSegment(sketch, "E2.9.8.0", {"start": v(282.5, 290.3) * mm, "end": v(257.5, 290.3) * mm});
            skLineSegment(sketch, "E2.9.8.1", {"start": v(282.5, 265.3) * mm, "end": v(282.5, 290.3) * mm});
            skLineSegment(sketch, "E2.9.8.2", {"start": v(282.5, 265.3) * mm, "end": v(257.5, 265.3) * mm});
            skLineSegment(sketch, "E2.9.8.3", {"start": v(257.5, 265.3) * mm, "end": v(257.5, 290.3) * mm});
            skLineSegment(sketch, "E2.9.9.0", {"start": v(282.5, 320.3) * mm, "end": v(257.5, 320.3) * mm});
            skLineSegment(sketch, "E2.9.9.1", {"start": v(282.5, 295.3) * mm, "end": v(282.5, 320.3) * mm});
            skLineSegment(sketch, "E2.9.9.2", {"start": v(282.5, 295.3) * mm, "end": v(257.5, 295.3) * mm});
            skLineSegment(sketch, "E2.9.9.3", {"start": v(257.5, 295.3) * mm, "end": v(257.5, 320.3) * mm});
            skLineSegment(sketch, "E2.9.10.0", {"start": v(282.5, 350.3) * mm, "end": v(257.5, 350.3) * mm});
            skLineSegment(sketch, "E2.9.10.1", {"start": v(282.5, 325.3) * mm, "end": v(282.5, 350.3) * mm});
            skLineSegment(sketch, "E2.9.10.2", {"start": v(282.5, 325.3) * mm, "end": v(257.5, 325.3) * mm});
            skLineSegment(sketch, "E2.9.10.3", {"start": v(257.5, 325.3) * mm, "end": v(257.5, 350.3) * mm});
            skLineSegment(sketch, "E2.9.11.0", {"start": v(282.5, 380.3) * mm, "end": v(257.5, 380.3) * mm});
            skLineSegment(sketch, "E2.9.11.1", {"start": v(282.5, 355.3) * mm, "end": v(282.5, 380.3) * mm});
            skLineSegment(sketch, "E2.9.11.2", {"start": v(282.5, 355.3) * mm, "end": v(257.5, 355.3) * mm});
            skLineSegment(sketch, "E2.9.11.3", {"start": v(257.5, 355.3) * mm, "end": v(257.5, 380.3) * mm});
            skLineSegment(sketch, "E2.9.12.0", {"start": v(282.5, 410.3) * mm, "end": v(257.5, 410.3) * mm});
            skLineSegment(sketch, "E2.9.12.1", {"start": v(282.5, 385.3) * mm, "end": v(282.5, 410.3) * mm});
            skLineSegment(sketch, "E2.9.12.2", {"start": v(282.5, 385.3) * mm, "end": v(257.5, 385.3) * mm});
            skLineSegment(sketch, "E2.9.12.3", {"start": v(257.5, 385.3) * mm, "end": v(257.5, 410.3) * mm});
            skLineSegment(sketch, "E2.9.13.0", {"start": v(282.5, 440.3) * mm, "end": v(257.5, 440.3) * mm});
            skLineSegment(sketch, "E2.9.13.1", {"start": v(282.5, 415.3) * mm, "end": v(282.5, 440.3) * mm});
            skLineSegment(sketch, "E2.9.13.2", {"start": v(282.5, 415.3) * mm, "end": v(257.5, 415.3) * mm});
            skLineSegment(sketch, "E2.9.13.3", {"start": v(257.5, 415.3) * mm, "end": v(257.5, 440.3) * mm});
            skLineSegment(sketch, "E2.9.14.0", {"start": v(282.5, 470.3) * mm, "end": v(257.5, 470.3) * mm});
            skLineSegment(sketch, "E2.9.14.1", {"start": v(282.5, 445.3) * mm, "end": v(282.5, 470.3) * mm});
            skLineSegment(sketch, "E2.9.14.2", {"start": v(282.5, 445.3) * mm, "end": v(257.5, 445.3) * mm});
            skLineSegment(sketch, "E2.9.14.3", {"start": v(257.5, 445.3) * mm, "end": v(257.5, 470.3) * mm});
            skLineSegment(sketch, "E2.9.15.0", {"start": v(282.5, 500.3) * mm, "end": v(257.5, 500.3) * mm});
            skLineSegment(sketch, "E2.9.15.1", {"start": v(282.5, 475.3) * mm, "end": v(282.5, 500.3) * mm});
            skLineSegment(sketch, "E2.9.15.2", {"start": v(282.5, 475.3) * mm, "end": v(257.5, 475.3) * mm});
            skLineSegment(sketch, "E2.9.15.3", {"start": v(257.5, 475.3) * mm, "end": v(257.5, 500.3) * mm});
            skLineSegment(sketch, "E2.9.16.0", {"start": v(282.5, 530.3) * mm, "end": v(257.5, 530.3) * mm});
            skLineSegment(sketch, "E2.9.16.1", {"start": v(282.5, 505.3) * mm, "end": v(282.5, 530.3) * mm});
            skLineSegment(sketch, "E2.9.16.2", {"start": v(282.5, 505.3) * mm, "end": v(257.5, 505.3) * mm});
            skLineSegment(sketch, "E2.9.16.3", {"start": v(257.5, 505.3) * mm, "end": v(257.5, 530.3) * mm});
            skLineSegment(sketch, "E2.9.17.0", {"start": v(282.5, 560.3) * mm, "end": v(257.5, 560.3) * mm});
            skLineSegment(sketch, "E2.9.17.1", {"start": v(282.5, 535.3) * mm, "end": v(282.5, 560.3) * mm});
            skLineSegment(sketch, "E2.9.17.2", {"start": v(282.5, 535.3) * mm, "end": v(257.5, 535.3) * mm});
            skLineSegment(sketch, "E2.9.17.3", {"start": v(257.5, 535.3) * mm, "end": v(257.5, 560.3) * mm});
            skLineSegment(sketch, "E2.9.18.0", {"start": v(282.5, 590.3) * mm, "end": v(257.5, 590.3) * mm});
            skLineSegment(sketch, "E2.9.18.1", {"start": v(282.5, 565.3) * mm, "end": v(282.5, 590.3) * mm});
            skLineSegment(sketch, "E2.9.18.2", {"start": v(282.5, 565.3) * mm, "end": v(257.5, 565.3) * mm});
            skLineSegment(sketch, "E2.9.18.3", {"start": v(257.5, 565.3) * mm, "end": v(257.5, 590.3) * mm});
            skLineSegment(sketch, "E2.9.19.0", {"start": v(282.5, 620.3) * mm, "end": v(257.5, 620.3) * mm});
            skLineSegment(sketch, "E2.9.19.1", {"start": v(282.5, 595.3) * mm, "end": v(282.5, 620.3) * mm});
            skLineSegment(sketch, "E2.9.19.2", {"start": v(282.5, 595.3) * mm, "end": v(257.5, 595.3) * mm});
            skLineSegment(sketch, "E2.9.19.3", {"start": v(257.5, 595.3) * mm, "end": v(257.5, 620.3) * mm});
            skLineSegment(sketch, "E2.9.20.0", {"start": v(282.5, 650.3) * mm, "end": v(257.5, 650.3) * mm});
            skLineSegment(sketch, "E2.9.20.1", {"start": v(282.5, 625.3) * mm, "end": v(282.5, 650.3) * mm});
            skLineSegment(sketch, "E2.9.20.2", {"start": v(282.5, 625.3) * mm, "end": v(257.5, 625.3) * mm});
            skLineSegment(sketch, "E2.9.20.3", {"start": v(257.5, 625.3) * mm, "end": v(257.5, 650.3) * mm});
            skLineSegment(sketch, "E2.9.21.0", {"start": v(282.5, 680.3) * mm, "end": v(257.5, 680.3) * mm});
            skLineSegment(sketch, "E2.9.21.1", {"start": v(282.5, 655.3) * mm, "end": v(282.5, 680.3) * mm});
            skLineSegment(sketch, "E2.9.21.2", {"start": v(282.5, 655.3) * mm, "end": v(257.5, 655.3) * mm});
            skLineSegment(sketch, "E2.9.21.3", {"start": v(257.5, 655.3) * mm, "end": v(257.5, 680.3) * mm});
            skLineSegment(sketch, "E2.9.22.0", {"start": v(282.5, 710.3) * mm, "end": v(257.5, 710.3) * mm});
            skLineSegment(sketch, "E2.9.22.1", {"start": v(282.5, 685.3) * mm, "end": v(282.5, 710.3) * mm});
            skLineSegment(sketch, "E2.9.22.2", {"start": v(282.5, 685.3) * mm, "end": v(257.5, 685.3) * mm});
            skLineSegment(sketch, "E2.9.22.3", {"start": v(257.5, 685.3) * mm, "end": v(257.5, 710.3) * mm});
            skLineSegment(sketch, "E2.9.23.0", {"start": v(282.5, 740.3) * mm, "end": v(257.5, 740.3) * mm});
            skLineSegment(sketch, "E2.9.23.1", {"start": v(282.5, 715.3) * mm, "end": v(282.5, 740.3) * mm});
            skLineSegment(sketch, "E2.9.23.2", {"start": v(282.5, 715.3) * mm, "end": v(257.5, 715.3) * mm});
            skLineSegment(sketch, "E2.9.23.3", {"start": v(257.5, 715.3) * mm, "end": v(257.5, 740.3) * mm});
            skLineSegment(sketch, "E2.9.24.0", {"start": v(282.5, 770.3) * mm, "end": v(257.5, 770.3) * mm});
            skLineSegment(sketch, "E2.9.24.1", {"start": v(282.5, 745.3) * mm, "end": v(282.5, 770.3) * mm});
            skLineSegment(sketch, "E2.9.24.2", {"start": v(282.5, 745.3) * mm, "end": v(257.5, 745.3) * mm});
            skLineSegment(sketch, "E2.9.24.3", {"start": v(257.5, 745.3) * mm, "end": v(257.5, 770.3) * mm});
            skLineSegment(sketch, "E2.9.25.0", {"start": v(282.5, 800.3) * mm, "end": v(257.5, 800.3) * mm});
            skLineSegment(sketch, "E2.9.25.1", {"start": v(282.5, 775.3) * mm, "end": v(282.5, 800.3) * mm});
            skLineSegment(sketch, "E2.9.25.2", {"start": v(282.5, 775.3) * mm, "end": v(257.5, 775.3) * mm});
            skLineSegment(sketch, "E2.9.25.3", {"start": v(257.5, 775.3) * mm, "end": v(257.5, 800.3) * mm});
            skLineSegment(sketch, "E2.9.26.0", {"start": v(282.5, 830.3) * mm, "end": v(257.5, 830.3) * mm});
            skLineSegment(sketch, "E2.9.26.1", {"start": v(282.5, 805.3) * mm, "end": v(282.5, 830.3) * mm});
            skLineSegment(sketch, "E2.9.26.2", {"start": v(282.5, 805.3) * mm, "end": v(257.5, 805.3) * mm});
            skLineSegment(sketch, "E2.9.26.3", {"start": v(257.5, 805.3) * mm, "end": v(257.5, 830.3) * mm});
            skLineSegment(sketch, "E2.9.27.0", {"start": v(282.5, 860.3) * mm, "end": v(257.5, 860.3) * mm});
            skLineSegment(sketch, "E2.9.27.1", {"start": v(282.5, 835.3) * mm, "end": v(282.5, 860.3) * mm});
            skLineSegment(sketch, "E2.9.27.2", {"start": v(282.5, 835.3) * mm, "end": v(257.5, 835.3) * mm});
            skLineSegment(sketch, "E2.9.27.3", {"start": v(257.5, 835.3) * mm, "end": v(257.5, 860.3) * mm});
            skLineSegment(sketch, "E2.9.28.0", {"start": v(282.5, 890.3) * mm, "end": v(257.5, 890.3) * mm});
            skLineSegment(sketch, "E2.9.28.1", {"start": v(282.5, 865.3) * mm, "end": v(282.5, 890.3) * mm});
            skLineSegment(sketch, "E2.9.28.2", {"start": v(282.5, 865.3) * mm, "end": v(257.5, 865.3) * mm});
            skLineSegment(sketch, "E2.9.28.3", {"start": v(257.5, 865.3) * mm, "end": v(257.5, 890.3) * mm});
            skLineSegment(sketch, "E2.9.29.0", {"start": v(282.5, 920.3) * mm, "end": v(257.5, 920.3) * mm});
            skLineSegment(sketch, "E2.9.29.1", {"start": v(282.5, 895.3) * mm, "end": v(282.5, 920.3) * mm});
            skLineSegment(sketch, "E2.9.29.2", {"start": v(282.5, 895.3) * mm, "end": v(257.5, 895.3) * mm});
            skLineSegment(sketch, "E2.9.29.3", {"start": v(257.5, 895.3) * mm, "end": v(257.5, 920.3) * mm});
            skLineSegment(sketch, "E2.9.30.0", {"start": v(282.5, 950.3) * mm, "end": v(257.5, 950.3) * mm});
            skLineSegment(sketch, "E2.9.30.1", {"start": v(282.5, 925.3) * mm, "end": v(282.5, 950.3) * mm});
            skLineSegment(sketch, "E2.9.30.2", {"start": v(282.5, 925.3) * mm, "end": v(257.5, 925.3) * mm});
            skLineSegment(sketch, "E2.9.30.3", {"start": v(257.5, 925.3) * mm, "end": v(257.5, 950.3) * mm});
            skLineSegment(sketch, "E2.10.0.0", {"start": v(312.5, 50.3) * mm, "end": v(287.5, 50.3) * mm});
            skLineSegment(sketch, "E2.10.0.1", {"start": v(312.5, 25.3) * mm, "end": v(312.5, 50.3) * mm});
            skLineSegment(sketch, "E2.10.0.2", {"start": v(312.5, 25.3) * mm, "end": v(287.5, 25.3) * mm});
            skLineSegment(sketch, "E2.10.0.3", {"start": v(287.5, 25.3) * mm, "end": v(287.5, 50.3) * mm});
            skLineSegment(sketch, "E2.10.1.0", {"start": v(312.5, 80.3) * mm, "end": v(287.5, 80.3) * mm});
            skLineSegment(sketch, "E2.10.1.1", {"start": v(312.5, 55.3) * mm, "end": v(312.5, 80.3) * mm});
            skLineSegment(sketch, "E2.10.1.2", {"start": v(312.5, 55.3) * mm, "end": v(287.5, 55.3) * mm});
            skLineSegment(sketch, "E2.10.1.3", {"start": v(287.5, 55.3) * mm, "end": v(287.5, 80.3) * mm});
            skLineSegment(sketch, "E2.10.2.0", {"start": v(312.5, 110.3) * mm, "end": v(287.5, 110.3) * mm});
            skLineSegment(sketch, "E2.10.2.1", {"start": v(312.5, 85.3) * mm, "end": v(312.5, 110.3) * mm});
            skLineSegment(sketch, "E2.10.2.2", {"start": v(312.5, 85.3) * mm, "end": v(287.5, 85.3) * mm});
            skLineSegment(sketch, "E2.10.2.3", {"start": v(287.5, 85.3) * mm, "end": v(287.5, 110.3) * mm});
            skLineSegment(sketch, "E2.10.3.0", {"start": v(312.5, 140.3) * mm, "end": v(287.5, 140.3) * mm});
            skLineSegment(sketch, "E2.10.3.1", {"start": v(312.5, 115.3) * mm, "end": v(312.5, 140.3) * mm});
            skLineSegment(sketch, "E2.10.3.2", {"start": v(312.5, 115.3) * mm, "end": v(287.5, 115.3) * mm});
            skLineSegment(sketch, "E2.10.3.3", {"start": v(287.5, 115.3) * mm, "end": v(287.5, 140.3) * mm});
            skLineSegment(sketch, "E2.10.4.0", {"start": v(312.5, 170.3) * mm, "end": v(287.5, 170.3) * mm});
            skLineSegment(sketch, "E2.10.4.1", {"start": v(312.5, 145.3) * mm, "end": v(312.5, 170.3) * mm});
            skLineSegment(sketch, "E2.10.4.2", {"start": v(312.5, 145.3) * mm, "end": v(287.5, 145.3) * mm});
            skLineSegment(sketch, "E2.10.4.3", {"start": v(287.5, 145.3) * mm, "end": v(287.5, 170.3) * mm});
            skLineSegment(sketch, "E2.10.5.0", {"start": v(312.5, 200.3) * mm, "end": v(287.5, 200.3) * mm});
            skLineSegment(sketch, "E2.10.5.1", {"start": v(312.5, 175.3) * mm, "end": v(312.5, 200.3) * mm});
            skLineSegment(sketch, "E2.10.5.2", {"start": v(312.5, 175.3) * mm, "end": v(287.5, 175.3) * mm});
            skLineSegment(sketch, "E2.10.5.3", {"start": v(287.5, 175.3) * mm, "end": v(287.5, 200.3) * mm});
            skLineSegment(sketch, "E2.10.6.0", {"start": v(312.5, 230.3) * mm, "end": v(287.5, 230.3) * mm});
            skLineSegment(sketch, "E2.10.6.1", {"start": v(312.5, 205.3) * mm, "end": v(312.5, 230.3) * mm});
            skLineSegment(sketch, "E2.10.6.2", {"start": v(312.5, 205.3) * mm, "end": v(287.5, 205.3) * mm});
            skLineSegment(sketch, "E2.10.6.3", {"start": v(287.5, 205.3) * mm, "end": v(287.5, 230.3) * mm});
            skLineSegment(sketch, "E2.10.7.0", {"start": v(312.5, 260.3) * mm, "end": v(287.5, 260.3) * mm});
            skLineSegment(sketch, "E2.10.7.1", {"start": v(312.5, 235.3) * mm, "end": v(312.5, 260.3) * mm});
            skLineSegment(sketch, "E2.10.7.2", {"start": v(312.5, 235.3) * mm, "end": v(287.5, 235.3) * mm});
            skLineSegment(sketch, "E2.10.7.3", {"start": v(287.5, 235.3) * mm, "end": v(287.5, 260.3) * mm});
            skLineSegment(sketch, "E2.10.8.0", {"start": v(312.5, 290.3) * mm, "end": v(287.5, 290.3) * mm});
            skLineSegment(sketch, "E2.10.8.1", {"start": v(312.5, 265.3) * mm, "end": v(312.5, 290.3) * mm});
            skLineSegment(sketch, "E2.10.8.2", {"start": v(312.5, 265.3) * mm, "end": v(287.5, 265.3) * mm});
            skLineSegment(sketch, "E2.10.8.3", {"start": v(287.5, 265.3) * mm, "end": v(287.5, 290.3) * mm});
            skLineSegment(sketch, "E2.10.9.0", {"start": v(312.5, 320.3) * mm, "end": v(287.5, 320.3) * mm});
            skLineSegment(sketch, "E2.10.9.1", {"start": v(312.5, 295.3) * mm, "end": v(312.5, 320.3) * mm});
            skLineSegment(sketch, "E2.10.9.2", {"start": v(312.5, 295.3) * mm, "end": v(287.5, 295.3) * mm});
            skLineSegment(sketch, "E2.10.9.3", {"start": v(287.5, 295.3) * mm, "end": v(287.5, 320.3) * mm});
            skLineSegment(sketch, "E2.10.10.0", {"start": v(312.5, 350.3) * mm, "end": v(287.5, 350.3) * mm});
            skLineSegment(sketch, "E2.10.10.1", {"start": v(312.5, 325.3) * mm, "end": v(312.5, 350.3) * mm});
            skLineSegment(sketch, "E2.10.10.2", {"start": v(312.5, 325.3) * mm, "end": v(287.5, 325.3) * mm});
            skLineSegment(sketch, "E2.10.10.3", {"start": v(287.5, 325.3) * mm, "end": v(287.5, 350.3) * mm});
            skLineSegment(sketch, "E2.10.11.0", {"start": v(312.5, 380.3) * mm, "end": v(287.5, 380.3) * mm});
            skLineSegment(sketch, "E2.10.11.1", {"start": v(312.5, 355.3) * mm, "end": v(312.5, 380.3) * mm});
            skLineSegment(sketch, "E2.10.11.2", {"start": v(312.5, 355.3) * mm, "end": v(287.5, 355.3) * mm});
            skLineSegment(sketch, "E2.10.11.3", {"start": v(287.5, 355.3) * mm, "end": v(287.5, 380.3) * mm});
            skLineSegment(sketch, "E2.10.12.0", {"start": v(312.5, 410.3) * mm, "end": v(287.5, 410.3) * mm});
            skLineSegment(sketch, "E2.10.12.1", {"start": v(312.5, 385.3) * mm, "end": v(312.5, 410.3) * mm});
            skLineSegment(sketch, "E2.10.12.2", {"start": v(312.5, 385.3) * mm, "end": v(287.5, 385.3) * mm});
            skLineSegment(sketch, "E2.10.12.3", {"start": v(287.5, 385.3) * mm, "end": v(287.5, 410.3) * mm});
            skLineSegment(sketch, "E2.10.13.0", {"start": v(312.5, 440.3) * mm, "end": v(287.5, 440.3) * mm});
            skLineSegment(sketch, "E2.10.13.1", {"start": v(312.5, 415.3) * mm, "end": v(312.5, 440.3) * mm});
            skLineSegment(sketch, "E2.10.13.2", {"start": v(312.5, 415.3) * mm, "end": v(287.5, 415.3) * mm});
            skLineSegment(sketch, "E2.10.13.3", {"start": v(287.5, 415.3) * mm, "end": v(287.5, 440.3) * mm});
            skLineSegment(sketch, "E2.10.14.0", {"start": v(312.5, 470.3) * mm, "end": v(287.5, 470.3) * mm});
            skLineSegment(sketch, "E2.10.14.1", {"start": v(312.5, 445.3) * mm, "end": v(312.5, 470.3) * mm});
            skLineSegment(sketch, "E2.10.14.2", {"start": v(312.5, 445.3) * mm, "end": v(287.5, 445.3) * mm});
            skLineSegment(sketch, "E2.10.14.3", {"start": v(287.5, 445.3) * mm, "end": v(287.5, 470.3) * mm});
            skLineSegment(sketch, "E2.10.15.0", {"start": v(312.5, 500.3) * mm, "end": v(287.5, 500.3) * mm});
            skLineSegment(sketch, "E2.10.15.1", {"start": v(312.5, 475.3) * mm, "end": v(312.5, 500.3) * mm});
            skLineSegment(sketch, "E2.10.15.2", {"start": v(312.5, 475.3) * mm, "end": v(287.5, 475.3) * mm});
            skLineSegment(sketch, "E2.10.15.3", {"start": v(287.5, 475.3) * mm, "end": v(287.5, 500.3) * mm});
            skLineSegment(sketch, "E2.10.16.0", {"start": v(312.5, 530.3) * mm, "end": v(287.5, 530.3) * mm});
            skLineSegment(sketch, "E2.10.16.1", {"start": v(312.5, 505.3) * mm, "end": v(312.5, 530.3) * mm});
            skLineSegment(sketch, "E2.10.16.2", {"start": v(312.5, 505.3) * mm, "end": v(287.5, 505.3) * mm});
            skLineSegment(sketch, "E2.10.16.3", {"start": v(287.5, 505.3) * mm, "end": v(287.5, 530.3) * mm});
            skLineSegment(sketch, "E2.10.17.0", {"start": v(312.5, 560.3) * mm, "end": v(287.5, 560.3) * mm});
            skLineSegment(sketch, "E2.10.17.1", {"start": v(312.5, 535.3) * mm, "end": v(312.5, 560.3) * mm});
            skLineSegment(sketch, "E2.10.17.2", {"start": v(312.5, 535.3) * mm, "end": v(287.5, 535.3) * mm});
            skLineSegment(sketch, "E2.10.17.3", {"start": v(287.5, 535.3) * mm, "end": v(287.5, 560.3) * mm});
            skLineSegment(sketch, "E2.10.18.0", {"start": v(312.5, 590.3) * mm, "end": v(287.5, 590.3) * mm});
            skLineSegment(sketch, "E2.10.18.1", {"start": v(312.5, 565.3) * mm, "end": v(312.5, 590.3) * mm});
            skLineSegment(sketch, "E2.10.18.2", {"start": v(312.5, 565.3) * mm, "end": v(287.5, 565.3) * mm});
            skLineSegment(sketch, "E2.10.18.3", {"start": v(287.5, 565.3) * mm, "end": v(287.5, 590.3) * mm});
            skLineSegment(sketch, "E2.10.19.0", {"start": v(312.5, 620.3) * mm, "end": v(287.5, 620.3) * mm});
            skLineSegment(sketch, "E2.10.19.1", {"start": v(312.5, 595.3) * mm, "end": v(312.5, 620.3) * mm});
            skLineSegment(sketch, "E2.10.19.2", {"start": v(312.5, 595.3) * mm, "end": v(287.5, 595.3) * mm});
            skLineSegment(sketch, "E2.10.19.3", {"start": v(287.5, 595.3) * mm, "end": v(287.5, 620.3) * mm});
            skLineSegment(sketch, "E2.10.20.0", {"start": v(312.5, 650.3) * mm, "end": v(287.5, 650.3) * mm});
            skLineSegment(sketch, "E2.10.20.1", {"start": v(312.5, 625.3) * mm, "end": v(312.5, 650.3) * mm});
            skLineSegment(sketch, "E2.10.20.2", {"start": v(312.5, 625.3) * mm, "end": v(287.5, 625.3) * mm});
            skLineSegment(sketch, "E2.10.20.3", {"start": v(287.5, 625.3) * mm, "end": v(287.5, 650.3) * mm});
            skLineSegment(sketch, "E2.10.21.0", {"start": v(312.5, 680.3) * mm, "end": v(287.5, 680.3) * mm});
            skLineSegment(sketch, "E2.10.21.1", {"start": v(312.5, 655.3) * mm, "end": v(312.5, 680.3) * mm});
            skLineSegment(sketch, "E2.10.21.2", {"start": v(312.5, 655.3) * mm, "end": v(287.5, 655.3) * mm});
            skLineSegment(sketch, "E2.10.21.3", {"start": v(287.5, 655.3) * mm, "end": v(287.5, 680.3) * mm});
            skLineSegment(sketch, "E2.10.22.0", {"start": v(312.5, 710.3) * mm, "end": v(287.5, 710.3) * mm});
            skLineSegment(sketch, "E2.10.22.1", {"start": v(312.5, 685.3) * mm, "end": v(312.5, 710.3) * mm});
            skLineSegment(sketch, "E2.10.22.2", {"start": v(312.5, 685.3) * mm, "end": v(287.5, 685.3) * mm});
            skLineSegment(sketch, "E2.10.22.3", {"start": v(287.5, 685.3) * mm, "end": v(287.5, 710.3) * mm});
            skLineSegment(sketch, "E2.10.23.0", {"start": v(312.5, 740.3) * mm, "end": v(287.5, 740.3) * mm});
            skLineSegment(sketch, "E2.10.23.1", {"start": v(312.5, 715.3) * mm, "end": v(312.5, 740.3) * mm});
            skLineSegment(sketch, "E2.10.23.2", {"start": v(312.5, 715.3) * mm, "end": v(287.5, 715.3) * mm});
            skLineSegment(sketch, "E2.10.23.3", {"start": v(287.5, 715.3) * mm, "end": v(287.5, 740.3) * mm});
            skLineSegment(sketch, "E2.10.24.0", {"start": v(312.5, 770.3) * mm, "end": v(287.5, 770.3) * mm});
            skLineSegment(sketch, "E2.10.24.1", {"start": v(312.5, 745.3) * mm, "end": v(312.5, 770.3) * mm});
            skLineSegment(sketch, "E2.10.24.2", {"start": v(312.5, 745.3) * mm, "end": v(287.5, 745.3) * mm});
            skLineSegment(sketch, "E2.10.24.3", {"start": v(287.5, 745.3) * mm, "end": v(287.5, 770.3) * mm});
            skLineSegment(sketch, "E2.10.25.0", {"start": v(312.5, 800.3) * mm, "end": v(287.5, 800.3) * mm});
            skLineSegment(sketch, "E2.10.25.1", {"start": v(312.5, 775.3) * mm, "end": v(312.5, 800.3) * mm});
            skLineSegment(sketch, "E2.10.25.2", {"start": v(312.5, 775.3) * mm, "end": v(287.5, 775.3) * mm});
            skLineSegment(sketch, "E2.10.25.3", {"start": v(287.5, 775.3) * mm, "end": v(287.5, 800.3) * mm});
            skLineSegment(sketch, "E2.10.26.0", {"start": v(312.5, 830.3) * mm, "end": v(287.5, 830.3) * mm});
            skLineSegment(sketch, "E2.10.26.1", {"start": v(312.5, 805.3) * mm, "end": v(312.5, 830.3) * mm});
            skLineSegment(sketch, "E2.10.26.2", {"start": v(312.5, 805.3) * mm, "end": v(287.5, 805.3) * mm});
            skLineSegment(sketch, "E2.10.26.3", {"start": v(287.5, 805.3) * mm, "end": v(287.5, 830.3) * mm});
            skLineSegment(sketch, "E2.10.27.0", {"start": v(312.5, 860.3) * mm, "end": v(287.5, 860.3) * mm});
            skLineSegment(sketch, "E2.10.27.1", {"start": v(312.5, 835.3) * mm, "end": v(312.5, 860.3) * mm});
            skLineSegment(sketch, "E2.10.27.2", {"start": v(312.5, 835.3) * mm, "end": v(287.5, 835.3) * mm});
            skLineSegment(sketch, "E2.10.27.3", {"start": v(287.5, 835.3) * mm, "end": v(287.5, 860.3) * mm});
            skLineSegment(sketch, "E2.10.28.0", {"start": v(312.5, 890.3) * mm, "end": v(287.5, 890.3) * mm});
            skLineSegment(sketch, "E2.10.28.1", {"start": v(312.5, 865.3) * mm, "end": v(312.5, 890.3) * mm});
            skLineSegment(sketch, "E2.10.28.2", {"start": v(312.5, 865.3) * mm, "end": v(287.5, 865.3) * mm});
            skLineSegment(sketch, "E2.10.28.3", {"start": v(287.5, 865.3) * mm, "end": v(287.5, 890.3) * mm});
            skLineSegment(sketch, "E2.10.29.0", {"start": v(312.5, 920.3) * mm, "end": v(287.5, 920.3) * mm});
            skLineSegment(sketch, "E2.10.29.1", {"start": v(312.5, 895.3) * mm, "end": v(312.5, 920.3) * mm});
            skLineSegment(sketch, "E2.10.29.2", {"start": v(312.5, 895.3) * mm, "end": v(287.5, 895.3) * mm});
            skLineSegment(sketch, "E2.10.29.3", {"start": v(287.5, 895.3) * mm, "end": v(287.5, 920.3) * mm});
            skLineSegment(sketch, "E2.10.30.0", {"start": v(312.5, 950.3) * mm, "end": v(287.5, 950.3) * mm});
            skLineSegment(sketch, "E2.10.30.1", {"start": v(312.5, 925.3) * mm, "end": v(312.5, 950.3) * mm});
            skLineSegment(sketch, "E2.10.30.2", {"start": v(312.5, 925.3) * mm, "end": v(287.5, 925.3) * mm});
            skLineSegment(sketch, "E2.10.30.3", {"start": v(287.5, 925.3) * mm, "end": v(287.5, 950.3) * mm});
            skLineSegment(sketch, "E2.direction1", {"start": v(-12.5, 50.3) * mm, "end": v(17.5, 50.3) * mm, "construction": true});
            skLineSegment(sketch, "E2.direction2", {"start": v(-12.5, 50.3) * mm, "end": v(-12.5, 80.3) * mm, "construction": true});
            skSolve(sketch);
        }
        {
            var Q0;
            {var subQ107=sQuery(id+"F0.wireOp",EDGE,"E0.bottom");Q0=makeQuery(id+"F0.imprint","IMPRINT",FACE,{"disambiguationData":[TD([[makeQuery(id+"F0.imprint","IMPRINT",EDGE,{"derivedFrom":subQ107}),1.0]])]});}
            extrude(context, id + "F1", {"entities" : qUnion([Q0]), "depth" : 25 * mm, "offsetDistance" : 25 * mm});
        }
        {
            var Q0;
            Q0=makeQuery(id+"F1.opExtrude","SWEPT_BODY",BODY,{"disambiguationData":[OSD([sQuery(id+"F0.wireOp",EDGE,"E0.bottom"),sQuery(id+"F0.wireOp",EDGE,"E0.top"),sQuery(id+"F0.wireOp",EDGE,"E0.left"),sQuery(id+"F0.wireOp",EDGE,"E0.right"),sQuery(id+"F0.wireOp",EDGE,"E1.bottom"),sQuery(id+"F0.wireOp",EDGE,"E1.top"),sQuery(id+"F0.wireOp",EDGE,"E1.left"),sQuery(id+"F0.wireOp",EDGE,"E2.0.1.0"),sQuery(id+"F0.wireOp",EDGE,"E2.0.1.1"),sQuery(id+"F0.wireOp",EDGE,"E2.0.1.2"),sQuery(id+"F0.wireOp",EDGE,"E2.0.2.0"),sQuery(id+"F0.wireOp",EDGE,"E2.0.2.1"),sQuery(id+"F0.wireOp",EDGE,"E2.0.2.2"),sQuery(id+"F0.wireOp",EDGE,"E2.0.3.0"),sQuery(id+"F0.wireOp",EDGE,"E2.0.3.1"),sQuery(id+"F0.wireOp",EDGE,"E2.0.3.2"),sQuery(id+"F0.wireOp",EDGE,"E2.0.4.0"),sQuery(id+"F0.wireOp",EDGE,"E2.0.4.1"),sQuery(id+"F0.wireOp",EDGE,"E2.0.4.2"),sQuery(id+"F0.wireOp",EDGE,"E2.0.5.0"),sQuery(id+"F0.wireOp",EDGE,"E2.0.5.1"),sQuery(id+"F0.wireOp",EDGE,"E2.0.5.2"),sQuery(id+"F0.wireOp",EDGE,"E2.0.6.0"),sQuery(id+"F0.wireOp",EDGE,"E2.0.6.1"),sQuery(id+"F0.wireOp",EDGE,"E2.0.6.2"),sQuery(id+"F0.wireOp",EDGE,"E2.0.7.0"),sQuery(id+"F0.wireOp",EDGE,"E2.0.7.1"),sQuery(id+"F0.wireOp",EDGE,"E2.0.7.2"),sQuery(id+"F0.wireOp",EDGE,"E2.0.8.0"),sQuery(id+"F0.wireOp",EDGE,"E2.0.8.1"),sQuery(id+"F0.wireOp",EDGE,"E2.0.8.2"),sQuery(id+"F0.wireOp",EDGE,"E2.0.9.0"),sQuery(id+"F0.wireOp",EDGE,"E2.0.9.1"),sQuery(id+"F0.wireOp",EDGE,"E2.0.9.2"),sQuery(id+"F0.wireOp",EDGE,"E2.0.10.0"),sQuery(id+"F0.wireOp",EDGE,"E2.0.10.1"),sQuery(id+"F0.wireOp",EDGE,"E2.0.10.2"),sQuery(id+"F0.wireOp",EDGE,"E2.0.11.0"),sQuery(id+"F0.wireOp",EDGE,"E2.0.11.1"),sQuery(id+"F0.wireOp",EDGE,"E2.0.11.2"),sQuery(id+"F0.wireOp",EDGE,"E2.0.12.0"),sQuery(id+"F0.wireOp",EDGE,"E2.0.12.1"),sQuery(id+"F0.wireOp",EDGE,"E2.0.12.2"),sQuery(id+"F0.wireOp",EDGE,"E2.0.13.0"),sQuery(id+"F0.wireOp",EDGE,"E2.0.13.1"),sQuery(id+"F0.wireOp",EDGE,"E2.0.13.2"),sQuery(id+"F0.wireOp",EDGE,"E2.0.14.0"),sQuery(id+"F0.wireOp",EDGE,"E2.0.14.1"),sQuery(id+"F0.wireOp",EDGE,"E2.0.14.2"),sQuery(id+"F0.wireOp",EDGE,"E2.0.15.0"),sQuery(id+"F0.wireOp",EDGE,"E2.0.15.1"),sQuery(id+"F0.wireOp",EDGE,"E2.0.15.2"),sQuery(id+"F0.wireOp",EDGE,"E2.0.16.0"),sQuery(id+"F0.wireOp",EDGE,"E2.0.16.1"),sQuery(id+"F0.wireOp",EDGE,"E2.0.16.2"),sQuery(id+"F0.wireOp",EDGE,"E2.0.17.0"),sQuery(id+"F0.wireOp",EDGE,"E2.0.17.1"),sQuery(id+"F0.wireOp",EDGE,"E2.0.17.2"),sQuery(id+"F0.wireOp",EDGE,"E2.0.18.0"),sQuery(id+"F0.wireOp",EDGE,"E2.0.18.1"),sQuery(id+"F0.wireOp",EDGE,"E2.0.18.2"),sQuery(id+"F0.wireOp",EDGE,"E2.0.19.0"),sQuery(id+"F0.wireOp",EDGE,"E2.0.19.1"),sQuery(id+"F0.wireOp",EDGE,"E2.0.19.2"),sQuery(id+"F0.wireOp",EDGE,"E2.0.20.0"),sQuery(id+"F0.wireOp",EDGE,"E2.0.20.1"),sQuery(id+"F0.wireOp",EDGE,"E2.0.20.2"),sQuery(id+"F0.wireOp",EDGE,"E2.0.21.0"),sQuery(id+"F0.wireOp",EDGE,"E2.0.21.1"),sQuery(id+"F0.wireOp",EDGE,"E2.0.21.2"),sQuery(id+"F0.wireOp",EDGE,"E2.0.22.0"),sQuery(id+"F0.wireOp",EDGE,"E2.0.22.1"),sQuery(id+"F0.wireOp",EDGE,"E2.0.22.2"),sQuery(id+"F0.wireOp",EDGE,"E2.0.23.0"),sQuery(id+"F0.wireOp",EDGE,"E2.0.23.1"),sQuery(id+"F0.wireOp",EDGE,"E2.0.23.2"),sQuery(id+"F0.wireOp",EDGE,"E2.0.24.0"),sQuery(id+"F0.wireOp",EDGE,"E2.0.24.1"),sQuery(id+"F0.wireOp",EDGE,"E2.0.24.2"),sQuery(id+"F0.wireOp",EDGE,"E2.0.25.0"),sQuery(id+"F0.wireOp",EDGE,"E2.0.25.1"),sQuery(id+"F0.wireOp",EDGE,"E2.0.25.2"),sQuery(id+"F0.wireOp",EDGE,"E2.0.26.0"),sQuery(id+"F0.wireOp",EDGE,"E2.0.26.1"),sQuery(id+"F0.wireOp",EDGE,"E2.0.26.2"),sQuery(id+"F0.wireOp",EDGE,"E2.0.27.0"),sQuery(id+"F0.wireOp",EDGE,"E2.0.27.1"),sQuery(id+"F0.wireOp",EDGE,"E2.0.27.2"),sQuery(id+"F0.wireOp",EDGE,"E2.0.28.0"),sQuery(id+"F0.wireOp",EDGE,"E2.0.28.1"),sQuery(id+"F0.wireOp",EDGE,"E2.0.28.2"),sQuery(id+"F0.wireOp",EDGE,"E2.0.29.0"),sQuery(id+"F0.wireOp",EDGE,"E2.0.29.1"),sQuery(id+"F0.wireOp",EDGE,"E2.0.29.2"),sQuery(id+"F0.wireOp",EDGE,"E2.0.30.1"),sQuery(id+"F0.wireOp",EDGE,"E2.0.30.2"),sQuery(id+"F0.wireOp",EDGE,"E2.1.0.0"),sQuery(id+"F0.wireOp",EDGE,"E2.1.0.1"),sQuery(id+"F0.wireOp",EDGE,"E2.1.0.2"),sQuery(id+"F0.wireOp",EDGE,"E2.1.0.3"),sQuery(id+"F0.wireOp",EDGE,"E2.1.1.0"),sQuery(id+"F0.wireOp",EDGE,"E2.1.1.1"),sQuery(id+"F0.wireOp",EDGE,"E2.1.1.2"),sQuery(id+"F0.wireOp",EDGE,"E2.1.1.3"),sQuery(id+"F0.wireOp",EDGE,"E2.1.2.0"),sQuery(id+"F0.wireOp",EDGE,"E2.1.2.1"),sQuery(id+"F0.wireOp",EDGE,"E2.1.2.2"),sQuery(id+"F0.wireOp",EDGE,"E2.1.2.3"),sQuery(id+"F0.wireOp",EDGE,"E2.1.3.0"),sQuery(id+"F0.wireOp",EDGE,"E2.1.3.1"),sQuery(id+"F0.wireOp",EDGE,"E2.1.3.2"),sQuery(id+"F0.wireOp",EDGE,"E2.1.3.3"),sQuery(id+"F0.wireOp",EDGE,"E2.1.4.0"),sQuery(id+"F0.wireOp",EDGE,"E2.1.4.1"),sQuery(id+"F0.wireOp",EDGE,"E2.1.4.2"),sQuery(id+"F0.wireOp",EDGE,"E2.1.4.3"),sQuery(id+"F0.wireOp",EDGE,"E2.1.5.0"),sQuery(id+"F0.wireOp",EDGE,"E2.1.5.1"),sQuery(id+"F0.wireOp",EDGE,"E2.1.5.2"),sQuery(id+"F0.wireOp",EDGE,"E2.1.5.3"),sQuery(id+"F0.wireOp",EDGE,"E2.1.6.0"),sQuery(id+"F0.wireOp",EDGE,"E2.1.6.1"),sQuery(id+"F0.wireOp",EDGE,"E2.1.6.2"),sQuery(id+"F0.wireOp",EDGE,"E2.1.6.3"),sQuery(id+"F0.wireOp",EDGE,"E2.1.7.0"),sQuery(id+"F0.wireOp",EDGE,"E2.1.7.1"),sQuery(id+"F0.wireOp",EDGE,"E2.1.7.2"),sQuery(id+"F0.wireOp",EDGE,"E2.1.7.3"),sQuery(id+"F0.wireOp",EDGE,"E2.1.8.0"),sQuery(id+"F0.wireOp",EDGE,"E2.1.8.1"),sQuery(id+"F0.wireOp",EDGE,"E2.1.8.2"),sQuery(id+"F0.wireOp",EDGE,"E2.1.8.3"),sQuery(id+"F0.wireOp",EDGE,"E2.1.9.0"),sQuery(id+"F0.wireOp",EDGE,"E2.1.9.1"),sQuery(id+"F0.wireOp",EDGE,"E2.1.9.2"),sQuery(id+"F0.wireOp",EDGE,"E2.1.9.3"),sQuery(id+"F0.wireOp",EDGE,"E2.1.10.0"),sQuery(id+"F0.wireOp",EDGE,"E2.1.10.1"),sQuery(id+"F0.wireOp",EDGE,"E2.1.10.2"),sQuery(id+"F0.wireOp",EDGE,"E2.1.10.3"),sQuery(id+"F0.wireOp",EDGE,"E2.1.11.0"),sQuery(id+"F0.wireOp",EDGE,"E2.1.11.1"),sQuery(id+"F0.wireOp",EDGE,"E2.1.11.2"),sQuery(id+"F0.wireOp",EDGE,"E2.1.11.3"),sQuery(id+"F0.wireOp",EDGE,"E2.1.12.0"),sQuery(id+"F0.wireOp",EDGE,"E2.1.12.1"),sQuery(id+"F0.wireOp",EDGE,"E2.1.12.2"),sQuery(id+"F0.wireOp",EDGE,"E2.1.12.3"),sQuery(id+"F0.wireOp",EDGE,"E2.1.13.0"),sQuery(id+"F0.wireOp",EDGE,"E2.1.13.1"),sQuery(id+"F0.wireOp",EDGE,"E2.1.13.2"),sQuery(id+"F0.wireOp",EDGE,"E2.1.13.3"),sQuery(id+"F0.wireOp",EDGE,"E2.1.14.0"),sQuery(id+"F0.wireOp",EDGE,"E2.1.14.1"),sQuery(id+"F0.wireOp",EDGE,"E2.1.14.2"),sQuery(id+"F0.wireOp",EDGE,"E2.1.14.3"),sQuery(id+"F0.wireOp",EDGE,"E2.1.15.0"),sQuery(id+"F0.wireOp",EDGE,"E2.1.15.1"),sQuery(id+"F0.wireOp",EDGE,"E2.1.15.2"),sQuery(id+"F0.wireOp",EDGE,"E2.1.15.3"),sQuery(id+"F0.wireOp",EDGE,"E2.1.16.0"),sQuery(id+"F0.wireOp",EDGE,"E2.1.16.1"),sQuery(id+"F0.wireOp",EDGE,"E2.1.16.2"),sQuery(id+"F0.wireOp",EDGE,"E2.1.16.3"),sQuery(id+"F0.wireOp",EDGE,"E2.1.17.0"),sQuery(id+"F0.wireOp",EDGE,"E2.1.17.1"),sQuery(id+"F0.wireOp",EDGE,"E2.1.17.2"),sQuery(id+"F0.wireOp",EDGE,"E2.1.17.3"),sQuery(id+"F0.wireOp",EDGE,"E2.1.18.0"),sQuery(id+"F0.wireOp",EDGE,"E2.1.18.1"),sQuery(id+"F0.wireOp",EDGE,"E2.1.18.2"),sQuery(id+"F0.wireOp",EDGE,"E2.1.18.3"),sQuery(id+"F0.wireOp",EDGE,"E2.1.19.0"),sQuery(id+"F0.wireOp",EDGE,"E2.1.19.1"),sQuery(id+"F0.wireOp",EDGE,"E2.1.19.2"),sQuery(id+"F0.wireOp",EDGE,"E2.1.19.3"),sQuery(id+"F0.wireOp",EDGE,"E2.1.20.0"),sQuery(id+"F0.wireOp",EDGE,"E2.1.20.1"),sQuery(id+"F0.wireOp",EDGE,"E2.1.20.2"),sQuery(id+"F0.wireOp",EDGE,"E2.1.20.3"),sQuery(id+"F0.wireOp",EDGE,"E2.1.21.0"),sQuery(id+"F0.wireOp",EDGE,"E2.1.21.1"),sQuery(id+"F0.wireOp",EDGE,"E2.1.21.2"),sQuery(id+"F0.wireOp",EDGE,"E2.1.21.3"),sQuery(id+"F0.wireOp",EDGE,"E2.1.22.0"),sQuery(id+"F0.wireOp",EDGE,"E2.1.22.1"),sQuery(id+"F0.wireOp",EDGE,"E2.1.22.2"),sQuery(id+"F0.wireOp",EDGE,"E2.1.22.3"),sQuery(id+"F0.wireOp",EDGE,"E2.1.23.0"),sQuery(id+"F0.wireOp",EDGE,"E2.1.23.1"),sQuery(id+"F0.wireOp",EDGE,"E2.1.23.2"),sQuery(id+"F0.wireOp",EDGE,"E2.1.23.3"),sQuery(id+"F0.wireOp",EDGE,"E2.1.24.0"),sQuery(id+"F0.wireOp",EDGE,"E2.1.24.1"),sQuery(id+"F0.wireOp",EDGE,"E2.1.24.2"),sQuery(id+"F0.wireOp",EDGE,"E2.1.24.3"),sQuery(id+"F0.wireOp",EDGE,"E2.1.25.0"),sQuery(id+"F0.wireOp",EDGE,"E2.1.25.1"),sQuery(id+"F0.wireOp",EDGE,"E2.1.25.2"),sQuery(id+"F0.wireOp",EDGE,"E2.1.25.3"),sQuery(id+"F0.wireOp",EDGE,"E2.1.26.0"),sQuery(id+"F0.wireOp",EDGE,"E2.1.26.1"),sQuery(id+"F0.wireOp",EDGE,"E2.1.26.2"),sQuery(id+"F0.wireOp",EDGE,"E2.1.26.3"),sQuery(id+"F0.wireOp",EDGE,"E2.1.27.0"),sQuery(id+"F0.wireOp",EDGE,"E2.1.27.1"),sQuery(id+"F0.wireOp",EDGE,"E2.1.27.2"),sQuery(id+"F0.wireOp",EDGE,"E2.1.27.3"),sQuery(id+"F0.wireOp",EDGE,"E2.1.28.0"),sQuery(id+"F0.wireOp",EDGE,"E2.1.28.1"),sQuery(id+"F0.wireOp",EDGE,"E2.1.28.2"),sQuery(id+"F0.wireOp",EDGE,"E2.1.28.3"),sQuery(id+"F0.wireOp",EDGE,"E2.1.29.0"),sQuery(id+"F0.wireOp",EDGE,"E2.1.29.1"),sQuery(id+"F0.wireOp",EDGE,"E2.1.29.2"),sQuery(id+"F0.wireOp",EDGE,"E2.1.29.3"),sQuery(id+"F0.wireOp",EDGE,"E2.1.30.1"),sQuery(id+"F0.wireOp",EDGE,"E2.1.30.2"),sQuery(id+"F0.wireOp",EDGE,"E2.1.30.3"),sQuery(id+"F0.wireOp",EDGE,"E2.2.0.0"),sQuery(id+"F0.wireOp",EDGE,"E2.2.0.1"),sQuery(id+"F0.wireOp",EDGE,"E2.2.0.2"),sQuery(id+"F0.wireOp",EDGE,"E2.2.0.3"),sQuery(id+"F0.wireOp",EDGE,"E2.2.1.0"),sQuery(id+"F0.wireOp",EDGE,"E2.2.1.1"),sQuery(id+"F0.wireOp",EDGE,"E2.2.1.2"),sQuery(id+"F0.wireOp",EDGE,"E2.2.1.3"),sQuery(id+"F0.wireOp",EDGE,"E2.2.2.0"),sQuery(id+"F0.wireOp",EDGE,"E2.2.2.1"),sQuery(id+"F0.wireOp",EDGE,"E2.2.2.2"),sQuery(id+"F0.wireOp",EDGE,"E2.2.2.3"),sQuery(id+"F0.wireOp",EDGE,"E2.2.3.0"),sQuery(id+"F0.wireOp",EDGE,"E2.2.3.1"),sQuery(id+"F0.wireOp",EDGE,"E2.2.3.2"),sQuery(id+"F0.wireOp",EDGE,"E2.2.3.3"),sQuery(id+"F0.wireOp",EDGE,"E2.2.4.0"),sQuery(id+"F0.wireOp",EDGE,"E2.2.4.1"),sQuery(id+"F0.wireOp",EDGE,"E2.2.4.2"),sQuery(id+"F0.wireOp",EDGE,"E2.2.4.3"),sQuery(id+"F0.wireOp",EDGE,"E2.2.5.0"),sQuery(id+"F0.wireOp",EDGE,"E2.2.5.1"),sQuery(id+"F0.wireOp",EDGE,"E2.2.5.2"),sQuery(id+"F0.wireOp",EDGE,"E2.2.5.3"),sQuery(id+"F0.wireOp",EDGE,"E2.2.6.0"),sQuery(id+"F0.wireOp",EDGE,"E2.2.6.1"),sQuery(id+"F0.wireOp",EDGE,"E2.2.6.2"),sQuery(id+"F0.wireOp",EDGE,"E2.2.6.3"),sQuery(id+"F0.wireOp",EDGE,"E2.2.7.0"),sQuery(id+"F0.wireOp",EDGE,"E2.2.7.1"),sQuery(id+"F0.wireOp",EDGE,"E2.2.7.2"),sQuery(id+"F0.wireOp",EDGE,"E2.2.7.3"),sQuery(id+"F0.wireOp",EDGE,"E2.2.8.0"),sQuery(id+"F0.wireOp",EDGE,"E2.2.8.1"),sQuery(id+"F0.wireOp",EDGE,"E2.2.8.2"),sQuery(id+"F0.wireOp",EDGE,"E2.2.8.3"),sQuery(id+"F0.wireOp",EDGE,"E2.2.9.0"),sQuery(id+"F0.wireOp",EDGE,"E2.2.9.1"),sQuery(id+"F0.wireOp",EDGE,"E2.2.9.2"),sQuery(id+"F0.wireOp",EDGE,"E2.2.9.3"),sQuery(id+"F0.wireOp",EDGE,"E2.2.10.0"),sQuery(id+"F0.wireOp",EDGE,"E2.2.10.1"),sQuery(id+"F0.wireOp",EDGE,"E2.2.10.2"),sQuery(id+"F0.wireOp",EDGE,"E2.2.10.3"),sQuery(id+"F0.wireOp",EDGE,"E2.2.11.0"),sQuery(id+"F0.wireOp",EDGE,"E2.2.11.1"),sQuery(id+"F0.wireOp",EDGE,"E2.2.11.2"),sQuery(id+"F0.wireOp",EDGE,"E2.2.11.3"),sQuery(id+"F0.wireOp",EDGE,"E2.2.12.0"),sQuery(id+"F0.wireOp",EDGE,"E2.2.12.1"),sQuery(id+"F0.wireOp",EDGE,"E2.2.12.2"),sQuery(id+"F0.wireOp",EDGE,"E2.2.12.3"),sQuery(id+"F0.wireOp",EDGE,"E2.2.13.0"),sQuery(id+"F0.wireOp",EDGE,"E2.2.13.1"),sQuery(id+"F0.wireOp",EDGE,"E2.2.13.2"),sQuery(id+"F0.wireOp",EDGE,"E2.2.13.3"),sQuery(id+"F0.wireOp",EDGE,"E2.2.14.0"),sQuery(id+"F0.wireOp",EDGE,"E2.2.14.1"),sQuery(id+"F0.wireOp",EDGE,"E2.2.14.2"),sQuery(id+"F0.wireOp",EDGE,"E2.2.14.3"),sQuery(id+"F0.wireOp",EDGE,"E2.2.15.0"),sQuery(id+"F0.wireOp",EDGE,"E2.2.15.1"),sQuery(id+"F0.wireOp",EDGE,"E2.2.15.2"),sQuery(id+"F0.wireOp",EDGE,"E2.2.15.3"),sQuery(id+"F0.wireOp",EDGE,"E2.2.16.0"),sQuery(id+"F0.wireOp",EDGE,"E2.2.16.1"),sQuery(id+"F0.wireOp",EDGE,"E2.2.16.2"),sQuery(id+"F0.wireOp",EDGE,"E2.2.16.3"),sQuery(id+"F0.wireOp",EDGE,"E2.2.17.0"),sQuery(id+"F0.wireOp",EDGE,"E2.2.17.1"),sQuery(id+"F0.wireOp",EDGE,"E2.2.17.2"),sQuery(id+"F0.wireOp",EDGE,"E2.2.17.3"),sQuery(id+"F0.wireOp",EDGE,"E2.2.18.0"),sQuery(id+"F0.wireOp",EDGE,"E2.2.18.1"),sQuery(id+"F0.wireOp",EDGE,"E2.2.18.2"),sQuery(id+"F0.wireOp",EDGE,"E2.2.18.3"),sQuery(id+"F0.wireOp",EDGE,"E2.2.19.0"),sQuery(id+"F0.wireOp",EDGE,"E2.2.19.1"),sQuery(id+"F0.wireOp",EDGE,"E2.2.19.2"),sQuery(id+"F0.wireOp",EDGE,"E2.2.19.3"),sQuery(id+"F0.wireOp",EDGE,"E2.2.20.0"),sQuery(id+"F0.wireOp",EDGE,"E2.2.20.1"),sQuery(id+"F0.wireOp",EDGE,"E2.2.20.2"),sQuery(id+"F0.wireOp",EDGE,"E2.2.20.3"),sQuery(id+"F0.wireOp",EDGE,"E2.2.21.0"),sQuery(id+"F0.wireOp",EDGE,"E2.2.21.1"),sQuery(id+"F0.wireOp",EDGE,"E2.2.21.2"),sQuery(id+"F0.wireOp",EDGE,"E2.2.21.3"),sQuery(id+"F0.wireOp",EDGE,"E2.2.22.0"),sQuery(id+"F0.wireOp",EDGE,"E2.2.22.1"),sQuery(id+"F0.wireOp",EDGE,"E2.2.22.2"),sQuery(id+"F0.wireOp",EDGE,"E2.2.22.3"),sQuery(id+"F0.wireOp",EDGE,"E2.2.23.0"),sQuery(id+"F0.wireOp",EDGE,"E2.2.23.1"),sQuery(id+"F0.wireOp",EDGE,"E2.2.23.2"),sQuery(id+"F0.wireOp",EDGE,"E2.2.23.3"),sQuery(id+"F0.wireOp",EDGE,"E2.2.24.0"),sQuery(id+"F0.wireOp",EDGE,"E2.2.24.1"),sQuery(id+"F0.wireOp",EDGE,"E2.2.24.2"),sQuery(id+"F0.wireOp",EDGE,"E2.2.24.3"),sQuery(id+"F0.wireOp",EDGE,"E2.2.25.0"),sQuery(id+"F0.wireOp",EDGE,"E2.2.25.1"),sQuery(id+"F0.wireOp",EDGE,"E2.2.25.2"),sQuery(id+"F0.wireOp",EDGE,"E2.2.25.3"),sQuery(id+"F0.wireOp",EDGE,"E2.2.26.0"),sQuery(id+"F0.wireOp",EDGE,"E2.2.26.1"),sQuery(id+"F0.wireOp",EDGE,"E2.2.26.2"),sQuery(id+"F0.wireOp",EDGE,"E2.2.26.3"),sQuery(id+"F0.wireOp",EDGE,"E2.2.27.0"),sQuery(id+"F0.wireOp",EDGE,"E2.2.27.1"),sQuery(id+"F0.wireOp",EDGE,"E2.2.27.2"),sQuery(id+"F0.wireOp",EDGE,"E2.2.27.3"),sQuery(id+"F0.wireOp",EDGE,"E2.2.28.0"),sQuery(id+"F0.wireOp",EDGE,"E2.2.28.1"),sQuery(id+"F0.wireOp",EDGE,"E2.2.28.2"),sQuery(id+"F0.wireOp",EDGE,"E2.2.28.3"),sQuery(id+"F0.wireOp",EDGE,"E2.2.29.0"),sQuery(id+"F0.wireOp",EDGE,"E2.2.29.1"),sQuery(id+"F0.wireOp",EDGE,"E2.2.29.2"),sQuery(id+"F0.wireOp",EDGE,"E2.2.29.3"),sQuery(id+"F0.wireOp",EDGE,"E2.2.30.1"),sQuery(id+"F0.wireOp",EDGE,"E2.2.30.2"),sQuery(id+"F0.wireOp",EDGE,"E2.2.30.3"),sQuery(id+"F0.wireOp",EDGE,"E2.3.0.0"),sQuery(id+"F0.wireOp",EDGE,"E2.3.0.1"),sQuery(id+"F0.wireOp",EDGE,"E2.3.0.2"),sQuery(id+"F0.wireOp",EDGE,"E2.3.0.3"),sQuery(id+"F0.wireOp",EDGE,"E2.3.1.0"),sQuery(id+"F0.wireOp",EDGE,"E2.3.1.1"),sQuery(id+"F0.wireOp",EDGE,"E2.3.1.2"),sQuery(id+"F0.wireOp",EDGE,"E2.3.1.3"),sQuery(id+"F0.wireOp",EDGE,"E2.3.2.0"),sQuery(id+"F0.wireOp",EDGE,"E2.3.2.1"),sQuery(id+"F0.wireOp",EDGE,"E2.3.2.2"),sQuery(id+"F0.wireOp",EDGE,"E2.3.2.3"),sQuery(id+"F0.wireOp",EDGE,"E2.3.3.0"),sQuery(id+"F0.wireOp",EDGE,"E2.3.3.1"),sQuery(id+"F0.wireOp",EDGE,"E2.3.3.2"),sQuery(id+"F0.wireOp",EDGE,"E2.3.3.3"),sQuery(id+"F0.wireOp",EDGE,"E2.3.4.0"),sQuery(id+"F0.wireOp",EDGE,"E2.3.4.1"),sQuery(id+"F0.wireOp",EDGE,"E2.3.4.2"),sQuery(id+"F0.wireOp",EDGE,"E2.3.4.3"),sQuery(id+"F0.wireOp",EDGE,"E2.3.5.0"),sQuery(id+"F0.wireOp",EDGE,"E2.3.5.1"),sQuery(id+"F0.wireOp",EDGE,"E2.3.5.2"),sQuery(id+"F0.wireOp",EDGE,"E2.3.5.3"),sQuery(id+"F0.wireOp",EDGE,"E2.3.6.0"),sQuery(id+"F0.wireOp",EDGE,"E2.3.6.1"),sQuery(id+"F0.wireOp",EDGE,"E2.3.6.2"),sQuery(id+"F0.wireOp",EDGE,"E2.3.6.3"),sQuery(id+"F0.wireOp",EDGE,"E2.3.7.0"),sQuery(id+"F0.wireOp",EDGE,"E2.3.7.1"),sQuery(id+"F0.wireOp",EDGE,"E2.3.7.2"),sQuery(id+"F0.wireOp",EDGE,"E2.3.7.3"),sQuery(id+"F0.wireOp",EDGE,"E2.3.8.0"),sQuery(id+"F0.wireOp",EDGE,"E2.3.8.1"),sQuery(id+"F0.wireOp",EDGE,"E2.3.8.2"),sQuery(id+"F0.wireOp",EDGE,"E2.3.8.3"),sQuery(id+"F0.wireOp",EDGE,"E2.3.9.0"),sQuery(id+"F0.wireOp",EDGE,"E2.3.9.1"),sQuery(id+"F0.wireOp",EDGE,"E2.3.9.2"),sQuery(id+"F0.wireOp",EDGE,"E2.3.9.3"),sQuery(id+"F0.wireOp",EDGE,"E2.3.10.0"),sQuery(id+"F0.wireOp",EDGE,"E2.3.10.1"),sQuery(id+"F0.wireOp",EDGE,"E2.3.10.2"),sQuery(id+"F0.wireOp",EDGE,"E2.3.10.3"),sQuery(id+"F0.wireOp",EDGE,"E2.3.11.0"),sQuery(id+"F0.wireOp",EDGE,"E2.3.11.1"),sQuery(id+"F0.wireOp",EDGE,"E2.3.11.2"),sQuery(id+"F0.wireOp",EDGE,"E2.3.11.3"),sQuery(id+"F0.wireOp",EDGE,"E2.3.12.0"),sQuery(id+"F0.wireOp",EDGE,"E2.3.12.1"),sQuery(id+"F0.wireOp",EDGE,"E2.3.12.2"),sQuery(id+"F0.wireOp",EDGE,"E2.3.12.3"),sQuery(id+"F0.wireOp",EDGE,"E2.3.13.0"),sQuery(id+"F0.wireOp",EDGE,"E2.3.13.1"),sQuery(id+"F0.wireOp",EDGE,"E2.3.13.2"),sQuery(id+"F0.wireOp",EDGE,"E2.3.13.3"),sQuery(id+"F0.wireOp",EDGE,"E2.3.14.0"),sQuery(id+"F0.wireOp",EDGE,"E2.3.14.1"),sQuery(id+"F0.wireOp",EDGE,"E2.3.14.2"),sQuery(id+"F0.wireOp",EDGE,"E2.3.14.3"),sQuery(id+"F0.wireOp",EDGE,"E2.3.15.0"),sQuery(id+"F0.wireOp",EDGE,"E2.3.15.1"),sQuery(id+"F0.wireOp",EDGE,"E2.3.15.2"),sQuery(id+"F0.wireOp",EDGE,"E2.3.15.3"),sQuery(id+"F0.wireOp",EDGE,"E2.3.16.0"),sQuery(id+"F0.wireOp",EDGE,"E2.3.16.1"),sQuery(id+"F0.wireOp",EDGE,"E2.3.16.2"),sQuery(id+"F0.wireOp",EDGE,"E2.3.16.3"),sQuery(id+"F0.wireOp",EDGE,"E2.3.17.0"),sQuery(id+"F0.wireOp",EDGE,"E2.3.17.1"),sQuery(id+"F0.wireOp",EDGE,"E2.3.17.2"),sQuery(id+"F0.wireOp",EDGE,"E2.3.17.3"),sQuery(id+"F0.wireOp",EDGE,"E2.3.18.0"),sQuery(id+"F0.wireOp",EDGE,"E2.3.18.1"),sQuery(id+"F0.wireOp",EDGE,"E2.3.18.2"),sQuery(id+"F0.wireOp",EDGE,"E2.3.18.3"),sQuery(id+"F0.wireOp",EDGE,"E2.3.19.0"),sQuery(id+"F0.wireOp",EDGE,"E2.3.19.1"),sQuery(id+"F0.wireOp",EDGE,"E2.3.19.2"),sQuery(id+"F0.wireOp",EDGE,"E2.3.19.3"),sQuery(id+"F0.wireOp",EDGE,"E2.3.20.0"),sQuery(id+"F0.wireOp",EDGE,"E2.3.20.1"),sQuery(id+"F0.wireOp",EDGE,"E2.3.20.2"),sQuery(id+"F0.wireOp",EDGE,"E2.3.20.3"),sQuery(id+"F0.wireOp",EDGE,"E2.3.21.0"),sQuery(id+"F0.wireOp",EDGE,"E2.3.21.1"),sQuery(id+"F0.wireOp",EDGE,"E2.3.21.2"),sQuery(id+"F0.wireOp",EDGE,"E2.3.21.3"),sQuery(id+"F0.wireOp",EDGE,"E2.3.22.0"),sQuery(id+"F0.wireOp",EDGE,"E2.3.22.1"),sQuery(id+"F0.wireOp",EDGE,"E2.3.22.2"),sQuery(id+"F0.wireOp",EDGE,"E2.3.22.3"),sQuery(id+"F0.wireOp",EDGE,"E2.3.23.0"),sQuery(id+"F0.wireOp",EDGE,"E2.3.23.1"),sQuery(id+"F0.wireOp",EDGE,"E2.3.23.2"),sQuery(id+"F0.wireOp",EDGE,"E2.3.23.3"),sQuery(id+"F0.wireOp",EDGE,"E2.3.24.0"),sQuery(id+"F0.wireOp",EDGE,"E2.3.24.1"),sQuery(id+"F0.wireOp",EDGE,"E2.3.24.2"),sQuery(id+"F0.wireOp",EDGE,"E2.3.24.3"),sQuery(id+"F0.wireOp",EDGE,"E2.3.25.0"),sQuery(id+"F0.wireOp",EDGE,"E2.3.25.1"),sQuery(id+"F0.wireOp",EDGE,"E2.3.25.2"),sQuery(id+"F0.wireOp",EDGE,"E2.3.25.3"),sQuery(id+"F0.wireOp",EDGE,"E2.3.26.0"),sQuery(id+"F0.wireOp",EDGE,"E2.3.26.1"),sQuery(id+"F0.wireOp",EDGE,"E2.3.26.2"),sQuery(id+"F0.wireOp",EDGE,"E2.3.26.3"),sQuery(id+"F0.wireOp",EDGE,"E2.3.27.0"),sQuery(id+"F0.wireOp",EDGE,"E2.3.27.1"),sQuery(id+"F0.wireOp",EDGE,"E2.3.27.2"),sQuery(id+"F0.wireOp",EDGE,"E2.3.27.3"),sQuery(id+"F0.wireOp",EDGE,"E2.3.28.0"),sQuery(id+"F0.wireOp",EDGE,"E2.3.28.1"),sQuery(id+"F0.wireOp",EDGE,"E2.3.28.2"),sQuery(id+"F0.wireOp",EDGE,"E2.3.28.3"),sQuery(id+"F0.wireOp",EDGE,"E2.3.29.0"),sQuery(id+"F0.wireOp",EDGE,"E2.3.29.1"),sQuery(id+"F0.wireOp",EDGE,"E2.3.29.2"),sQuery(id+"F0.wireOp",EDGE,"E2.3.29.3"),sQuery(id+"F0.wireOp",EDGE,"E2.3.30.1"),sQuery(id+"F0.wireOp",EDGE,"E2.3.30.2"),sQuery(id+"F0.wireOp",EDGE,"E2.3.30.3"),sQuery(id+"F0.wireOp",EDGE,"E2.4.0.0"),sQuery(id+"F0.wireOp",EDGE,"E2.4.0.1"),sQuery(id+"F0.wireOp",EDGE,"E2.4.0.2"),sQuery(id+"F0.wireOp",EDGE,"E2.4.0.3"),sQuery(id+"F0.wireOp",EDGE,"E2.4.1.0"),sQuery(id+"F0.wireOp",EDGE,"E2.4.1.1"),sQuery(id+"F0.wireOp",EDGE,"E2.4.1.2"),sQuery(id+"F0.wireOp",EDGE,"E2.4.1.3"),sQuery(id+"F0.wireOp",EDGE,"E2.4.2.0"),sQuery(id+"F0.wireOp",EDGE,"E2.4.2.1"),sQuery(id+"F0.wireOp",EDGE,"E2.4.2.2"),sQuery(id+"F0.wireOp",EDGE,"E2.4.2.3"),sQuery(id+"F0.wireOp",EDGE,"E2.4.3.0"),sQuery(id+"F0.wireOp",EDGE,"E2.4.3.1"),sQuery(id+"F0.wireOp",EDGE,"E2.4.3.2"),sQuery(id+"F0.wireOp",EDGE,"E2.4.3.3"),sQuery(id+"F0.wireOp",EDGE,"E2.4.4.0"),sQuery(id+"F0.wireOp",EDGE,"E2.4.4.1"),sQuery(id+"F0.wireOp",EDGE,"E2.4.4.2"),sQuery(id+"F0.wireOp",EDGE,"E2.4.4.3"),sQuery(id+"F0.wireOp",EDGE,"E2.4.5.0"),sQuery(id+"F0.wireOp",EDGE,"E2.4.5.1"),sQuery(id+"F0.wireOp",EDGE,"E2.4.5.2"),sQuery(id+"F0.wireOp",EDGE,"E2.4.5.3"),sQuery(id+"F0.wireOp",EDGE,"E2.4.6.0"),sQuery(id+"F0.wireOp",EDGE,"E2.4.6.1"),sQuery(id+"F0.wireOp",EDGE,"E2.4.6.2"),sQuery(id+"F0.wireOp",EDGE,"E2.4.6.3"),sQuery(id+"F0.wireOp",EDGE,"E2.4.7.0"),sQuery(id+"F0.wireOp",EDGE,"E2.4.7.1"),sQuery(id+"F0.wireOp",EDGE,"E2.4.7.2"),sQuery(id+"F0.wireOp",EDGE,"E2.4.7.3"),sQuery(id+"F0.wireOp",EDGE,"E2.4.8.0"),sQuery(id+"F0.wireOp",EDGE,"E2.4.8.1"),sQuery(id+"F0.wireOp",EDGE,"E2.4.8.2"),sQuery(id+"F0.wireOp",EDGE,"E2.4.8.3"),sQuery(id+"F0.wireOp",EDGE,"E2.4.9.0"),sQuery(id+"F0.wireOp",EDGE,"E2.4.9.1"),sQuery(id+"F0.wireOp",EDGE,"E2.4.9.2"),sQuery(id+"F0.wireOp",EDGE,"E2.4.9.3"),sQuery(id+"F0.wireOp",EDGE,"E2.4.10.0"),sQuery(id+"F0.wireOp",EDGE,"E2.4.10.1"),sQuery(id+"F0.wireOp",EDGE,"E2.4.10.2"),sQuery(id+"F0.wireOp",EDGE,"E2.4.10.3"),sQuery(id+"F0.wireOp",EDGE,"E2.4.11.0"),sQuery(id+"F0.wireOp",EDGE,"E2.4.11.1"),sQuery(id+"F0.wireOp",EDGE,"E2.4.11.2"),sQuery(id+"F0.wireOp",EDGE,"E2.4.11.3"),sQuery(id+"F0.wireOp",EDGE,"E2.4.12.0"),sQuery(id+"F0.wireOp",EDGE,"E2.4.12.1"),sQuery(id+"F0.wireOp",EDGE,"E2.4.12.2"),sQuery(id+"F0.wireOp",EDGE,"E2.4.12.3"),sQuery(id+"F0.wireOp",EDGE,"E2.4.13.0"),sQuery(id+"F0.wireOp",EDGE,"E2.4.13.1"),sQuery(id+"F0.wireOp",EDGE,"E2.4.13.2"),sQuery(id+"F0.wireOp",EDGE,"E2.4.13.3"),sQuery(id+"F0.wireOp",EDGE,"E2.4.14.0"),sQuery(id+"F0.wireOp",EDGE,"E2.4.14.1"),sQuery(id+"F0.wireOp",EDGE,"E2.4.14.2"),sQuery(id+"F0.wireOp",EDGE,"E2.4.14.3"),sQuery(id+"F0.wireOp",EDGE,"E2.4.15.0"),sQuery(id+"F0.wireOp",EDGE,"E2.4.15.1"),sQuery(id+"F0.wireOp",EDGE,"E2.4.15.2"),sQuery(id+"F0.wireOp",EDGE,"E2.4.15.3"),sQuery(id+"F0.wireOp",EDGE,"E2.4.16.0"),sQuery(id+"F0.wireOp",EDGE,"E2.4.16.1"),sQuery(id+"F0.wireOp",EDGE,"E2.4.16.2"),sQuery(id+"F0.wireOp",EDGE,"E2.4.16.3"),sQuery(id+"F0.wireOp",EDGE,"E2.4.17.0"),sQuery(id+"F0.wireOp",EDGE,"E2.4.17.1"),sQuery(id+"F0.wireOp",EDGE,"E2.4.17.2"),sQuery(id+"F0.wireOp",EDGE,"E2.4.17.3"),sQuery(id+"F0.wireOp",EDGE,"E2.4.18.0"),sQuery(id+"F0.wireOp",EDGE,"E2.4.18.1"),sQuery(id+"F0.wireOp",EDGE,"E2.4.18.2"),sQuery(id+"F0.wireOp",EDGE,"E2.4.18.3"),sQuery(id+"F0.wireOp",EDGE,"E2.4.19.0"),sQuery(id+"F0.wireOp",EDGE,"E2.4.19.1"),sQuery(id+"F0.wireOp",EDGE,"E2.4.19.2"),sQuery(id+"F0.wireOp",EDGE,"E2.4.19.3"),sQuery(id+"F0.wireOp",EDGE,"E2.4.20.0"),sQuery(id+"F0.wireOp",EDGE,"E2.4.20.1"),sQuery(id+"F0.wireOp",EDGE,"E2.4.20.2"),sQuery(id+"F0.wireOp",EDGE,"E2.4.20.3"),sQuery(id+"F0.wireOp",EDGE,"E2.4.21.0"),sQuery(id+"F0.wireOp",EDGE,"E2.4.21.1"),sQuery(id+"F0.wireOp",EDGE,"E2.4.21.2"),sQuery(id+"F0.wireOp",EDGE,"E2.4.21.3"),sQuery(id+"F0.wireOp",EDGE,"E2.4.22.0"),sQuery(id+"F0.wireOp",EDGE,"E2.4.22.1"),sQuery(id+"F0.wireOp",EDGE,"E2.4.22.2"),sQuery(id+"F0.wireOp",EDGE,"E2.4.22.3"),sQuery(id+"F0.wireOp",EDGE,"E2.4.23.0"),sQuery(id+"F0.wireOp",EDGE,"E2.4.23.1"),sQuery(id+"F0.wireOp",EDGE,"E2.4.23.2"),sQuery(id+"F0.wireOp",EDGE,"E2.4.23.3"),sQuery(id+"F0.wireOp",EDGE,"E2.4.24.0"),sQuery(id+"F0.wireOp",EDGE,"E2.4.24.1"),sQuery(id+"F0.wireOp",EDGE,"E2.4.24.2"),sQuery(id+"F0.wireOp",EDGE,"E2.4.24.3"),sQuery(id+"F0.wireOp",EDGE,"E2.4.25.0"),sQuery(id+"F0.wireOp",EDGE,"E2.4.25.1"),sQuery(id+"F0.wireOp",EDGE,"E2.4.25.2"),sQuery(id+"F0.wireOp",EDGE,"E2.4.25.3"),sQuery(id+"F0.wireOp",EDGE,"E2.4.26.0"),sQuery(id+"F0.wireOp",EDGE,"E2.4.26.1"),sQuery(id+"F0.wireOp",EDGE,"E2.4.26.2"),sQuery(id+"F0.wireOp",EDGE,"E2.4.26.3"),sQuery(id+"F0.wireOp",EDGE,"E2.4.27.0"),sQuery(id+"F0.wireOp",EDGE,"E2.4.27.1"),sQuery(id+"F0.wireOp",EDGE,"E2.4.27.2"),sQuery(id+"F0.wireOp",EDGE,"E2.4.27.3"),sQuery(id+"F0.wireOp",EDGE,"E2.4.28.0"),sQuery(id+"F0.wireOp",EDGE,"E2.4.28.1"),sQuery(id+"F0.wireOp",EDGE,"E2.4.28.2"),sQuery(id+"F0.wireOp",EDGE,"E2.4.28.3"),sQuery(id+"F0.wireOp",EDGE,"E2.4.29.0"),sQuery(id+"F0.wireOp",EDGE,"E2.4.29.1"),sQuery(id+"F0.wireOp",EDGE,"E2.4.29.2"),sQuery(id+"F0.wireOp",EDGE,"E2.4.29.3"),sQuery(id+"F0.wireOp",EDGE,"E2.4.30.1"),sQuery(id+"F0.wireOp",EDGE,"E2.4.30.2"),sQuery(id+"F0.wireOp",EDGE,"E2.4.30.3"),sQuery(id+"F0.wireOp",EDGE,"E2.5.0.0"),sQuery(id+"F0.wireOp",EDGE,"E2.5.0.1"),sQuery(id+"F0.wireOp",EDGE,"E2.5.0.2"),sQuery(id+"F0.wireOp",EDGE,"E2.5.0.3"),sQuery(id+"F0.wireOp",EDGE,"E2.5.1.0"),sQuery(id+"F0.wireOp",EDGE,"E2.5.1.1"),sQuery(id+"F0.wireOp",EDGE,"E2.5.1.2"),sQuery(id+"F0.wireOp",EDGE,"E2.5.1.3"),sQuery(id+"F0.wireOp",EDGE,"E2.5.2.0"),sQuery(id+"F0.wireOp",EDGE,"E2.5.2.1"),sQuery(id+"F0.wireOp",EDGE,"E2.5.2.2"),sQuery(id+"F0.wireOp",EDGE,"E2.5.2.3"),sQuery(id+"F0.wireOp",EDGE,"E2.5.3.0"),sQuery(id+"F0.wireOp",EDGE,"E2.5.3.1"),sQuery(id+"F0.wireOp",EDGE,"E2.5.3.2"),sQuery(id+"F0.wireOp",EDGE,"E2.5.3.3"),sQuery(id+"F0.wireOp",EDGE,"E2.5.4.0"),sQuery(id+"F0.wireOp",EDGE,"E2.5.4.1"),sQuery(id+"F0.wireOp",EDGE,"E2.5.4.2"),sQuery(id+"F0.wireOp",EDGE,"E2.5.4.3"),sQuery(id+"F0.wireOp",EDGE,"E2.5.5.0"),sQuery(id+"F0.wireOp",EDGE,"E2.5.5.1"),sQuery(id+"F0.wireOp",EDGE,"E2.5.5.2"),sQuery(id+"F0.wireOp",EDGE,"E2.5.5.3"),sQuery(id+"F0.wireOp",EDGE,"E2.5.6.0"),sQuery(id+"F0.wireOp",EDGE,"E2.5.6.1"),sQuery(id+"F0.wireOp",EDGE,"E2.5.6.2"),sQuery(id+"F0.wireOp",EDGE,"E2.5.6.3"),sQuery(id+"F0.wireOp",EDGE,"E2.5.7.0"),sQuery(id+"F0.wireOp",EDGE,"E2.5.7.1"),sQuery(id+"F0.wireOp",EDGE,"E2.5.7.2"),sQuery(id+"F0.wireOp",EDGE,"E2.5.7.3"),sQuery(id+"F0.wireOp",EDGE,"E2.5.8.0"),sQuery(id+"F0.wireOp",EDGE,"E2.5.8.1"),sQuery(id+"F0.wireOp",EDGE,"E2.5.8.2"),sQuery(id+"F0.wireOp",EDGE,"E2.5.8.3"),sQuery(id+"F0.wireOp",EDGE,"E2.5.9.0"),sQuery(id+"F0.wireOp",EDGE,"E2.5.9.1"),sQuery(id+"F0.wireOp",EDGE,"E2.5.9.2"),sQuery(id+"F0.wireOp",EDGE,"E2.5.9.3"),sQuery(id+"F0.wireOp",EDGE,"E2.5.10.0"),sQuery(id+"F0.wireOp",EDGE,"E2.5.10.1"),sQuery(id+"F0.wireOp",EDGE,"E2.5.10.2"),sQuery(id+"F0.wireOp",EDGE,"E2.5.10.3"),sQuery(id+"F0.wireOp",EDGE,"E2.5.11.0"),sQuery(id+"F0.wireOp",EDGE,"E2.5.11.1"),sQuery(id+"F0.wireOp",EDGE,"E2.5.11.2"),sQuery(id+"F0.wireOp",EDGE,"E2.5.11.3"),sQuery(id+"F0.wireOp",EDGE,"E2.5.12.0"),sQuery(id+"F0.wireOp",EDGE,"E2.5.12.1"),sQuery(id+"F0.wireOp",EDGE,"E2.5.12.2"),sQuery(id+"F0.wireOp",EDGE,"E2.5.12.3"),sQuery(id+"F0.wireOp",EDGE,"E2.5.13.0"),sQuery(id+"F0.wireOp",EDGE,"E2.5.13.1"),sQuery(id+"F0.wireOp",EDGE,"E2.5.13.2"),sQuery(id+"F0.wireOp",EDGE,"E2.5.13.3"),sQuery(id+"F0.wireOp",EDGE,"E2.5.14.0"),sQuery(id+"F0.wireOp",EDGE,"E2.5.14.1"),sQuery(id+"F0.wireOp",EDGE,"E2.5.14.2"),sQuery(id+"F0.wireOp",EDGE,"E2.5.14.3"),sQuery(id+"F0.wireOp",EDGE,"E2.5.15.0"),sQuery(id+"F0.wireOp",EDGE,"E2.5.15.1"),sQuery(id+"F0.wireOp",EDGE,"E2.5.15.2"),sQuery(id+"F0.wireOp",EDGE,"E2.5.15.3"),sQuery(id+"F0.wireOp",EDGE,"E2.5.16.0"),sQuery(id+"F0.wireOp",EDGE,"E2.5.16.1"),sQuery(id+"F0.wireOp",EDGE,"E2.5.16.2"),sQuery(id+"F0.wireOp",EDGE,"E2.5.16.3"),sQuery(id+"F0.wireOp",EDGE,"E2.5.17.0"),sQuery(id+"F0.wireOp",EDGE,"E2.5.17.1"),sQuery(id+"F0.wireOp",EDGE,"E2.5.17.2"),sQuery(id+"F0.wireOp",EDGE,"E2.5.17.3"),sQuery(id+"F0.wireOp",EDGE,"E2.5.18.0"),sQuery(id+"F0.wireOp",EDGE,"E2.5.18.1"),sQuery(id+"F0.wireOp",EDGE,"E2.5.18.2"),sQuery(id+"F0.wireOp",EDGE,"E2.5.18.3"),sQuery(id+"F0.wireOp",EDGE,"E2.5.19.0"),sQuery(id+"F0.wireOp",EDGE,"E2.5.19.1"),sQuery(id+"F0.wireOp",EDGE,"E2.5.19.2"),sQuery(id+"F0.wireOp",EDGE,"E2.5.19.3"),sQuery(id+"F0.wireOp",EDGE,"E2.5.20.0"),sQuery(id+"F0.wireOp",EDGE,"E2.5.20.1"),sQuery(id+"F0.wireOp",EDGE,"E2.5.20.2"),sQuery(id+"F0.wireOp",EDGE,"E2.5.20.3"),sQuery(id+"F0.wireOp",EDGE,"E2.5.21.0"),sQuery(id+"F0.wireOp",EDGE,"E2.5.21.1"),sQuery(id+"F0.wireOp",EDGE,"E2.5.21.2"),sQuery(id+"F0.wireOp",EDGE,"E2.5.21.3"),sQuery(id+"F0.wireOp",EDGE,"E2.5.22.0"),sQuery(id+"F0.wireOp",EDGE,"E2.5.22.1"),sQuery(id+"F0.wireOp",EDGE,"E2.5.22.2"),sQuery(id+"F0.wireOp",EDGE,"E2.5.22.3"),sQuery(id+"F0.wireOp",EDGE,"E2.5.23.0"),sQuery(id+"F0.wireOp",EDGE,"E2.5.23.1"),sQuery(id+"F0.wireOp",EDGE,"E2.5.23.2"),sQuery(id+"F0.wireOp",EDGE,"E2.5.23.3"),sQuery(id+"F0.wireOp",EDGE,"E2.5.24.0"),sQuery(id+"F0.wireOp",EDGE,"E2.5.24.1"),sQuery(id+"F0.wireOp",EDGE,"E2.5.24.2"),sQuery(id+"F0.wireOp",EDGE,"E2.5.24.3"),sQuery(id+"F0.wireOp",EDGE,"E2.5.25.0"),sQuery(id+"F0.wireOp",EDGE,"E2.5.25.1"),sQuery(id+"F0.wireOp",EDGE,"E2.5.25.2"),sQuery(id+"F0.wireOp",EDGE,"E2.5.25.3"),sQuery(id+"F0.wireOp",EDGE,"E2.5.26.0"),sQuery(id+"F0.wireOp",EDGE,"E2.5.26.1"),sQuery(id+"F0.wireOp",EDGE,"E2.5.26.2"),sQuery(id+"F0.wireOp",EDGE,"E2.5.26.3"),sQuery(id+"F0.wireOp",EDGE,"E2.5.27.0"),sQuery(id+"F0.wireOp",EDGE,"E2.5.27.1"),sQuery(id+"F0.wireOp",EDGE,"E2.5.27.2"),sQuery(id+"F0.wireOp",EDGE,"E2.5.27.3"),sQuery(id+"F0.wireOp",EDGE,"E2.5.28.0"),sQuery(id+"F0.wireOp",EDGE,"E2.5.28.1"),sQuery(id+"F0.wireOp",EDGE,"E2.5.28.2"),sQuery(id+"F0.wireOp",EDGE,"E2.5.28.3"),sQuery(id+"F0.wireOp",EDGE,"E2.5.29.0"),sQuery(id+"F0.wireOp",EDGE,"E2.5.29.1"),sQuery(id+"F0.wireOp",EDGE,"E2.5.29.2"),sQuery(id+"F0.wireOp",EDGE,"E2.5.29.3"),sQuery(id+"F0.wireOp",EDGE,"E2.5.30.1"),sQuery(id+"F0.wireOp",EDGE,"E2.5.30.2"),sQuery(id+"F0.wireOp",EDGE,"E2.5.30.3"),sQuery(id+"F0.wireOp",EDGE,"E2.6.0.0"),sQuery(id+"F0.wireOp",EDGE,"E2.6.0.1"),sQuery(id+"F0.wireOp",EDGE,"E2.6.0.2"),sQuery(id+"F0.wireOp",EDGE,"E2.6.0.3"),sQuery(id+"F0.wireOp",EDGE,"E2.6.1.0"),sQuery(id+"F0.wireOp",EDGE,"E2.6.1.1"),sQuery(id+"F0.wireOp",EDGE,"E2.6.1.2"),sQuery(id+"F0.wireOp",EDGE,"E2.6.1.3"),sQuery(id+"F0.wireOp",EDGE,"E2.6.2.0"),sQuery(id+"F0.wireOp",EDGE,"E2.6.2.1"),sQuery(id+"F0.wireOp",EDGE,"E2.6.2.2"),sQuery(id+"F0.wireOp",EDGE,"E2.6.2.3"),sQuery(id+"F0.wireOp",EDGE,"E2.6.3.0"),sQuery(id+"F0.wireOp",EDGE,"E2.6.3.1"),sQuery(id+"F0.wireOp",EDGE,"E2.6.3.2"),sQuery(id+"F0.wireOp",EDGE,"E2.6.3.3"),sQuery(id+"F0.wireOp",EDGE,"E2.6.4.0"),sQuery(id+"F0.wireOp",EDGE,"E2.6.4.1"),sQuery(id+"F0.wireOp",EDGE,"E2.6.4.2"),sQuery(id+"F0.wireOp",EDGE,"E2.6.4.3"),sQuery(id+"F0.wireOp",EDGE,"E2.6.5.0"),sQuery(id+"F0.wireOp",EDGE,"E2.6.5.1"),sQuery(id+"F0.wireOp",EDGE,"E2.6.5.2"),sQuery(id+"F0.wireOp",EDGE,"E2.6.5.3"),sQuery(id+"F0.wireOp",EDGE,"E2.6.6.0"),sQuery(id+"F0.wireOp",EDGE,"E2.6.6.1"),sQuery(id+"F0.wireOp",EDGE,"E2.6.6.2"),sQuery(id+"F0.wireOp",EDGE,"E2.6.6.3"),sQuery(id+"F0.wireOp",EDGE,"E2.6.7.0"),sQuery(id+"F0.wireOp",EDGE,"E2.6.7.1"),sQuery(id+"F0.wireOp",EDGE,"E2.6.7.2"),sQuery(id+"F0.wireOp",EDGE,"E2.6.7.3"),sQuery(id+"F0.wireOp",EDGE,"E2.6.8.0"),sQuery(id+"F0.wireOp",EDGE,"E2.6.8.1"),sQuery(id+"F0.wireOp",EDGE,"E2.6.8.2"),sQuery(id+"F0.wireOp",EDGE,"E2.6.8.3"),sQuery(id+"F0.wireOp",EDGE,"E2.6.9.0"),sQuery(id+"F0.wireOp",EDGE,"E2.6.9.1"),sQuery(id+"F0.wireOp",EDGE,"E2.6.9.2"),sQuery(id+"F0.wireOp",EDGE,"E2.6.9.3"),sQuery(id+"F0.wireOp",EDGE,"E2.6.10.0"),sQuery(id+"F0.wireOp",EDGE,"E2.6.10.1"),sQuery(id+"F0.wireOp",EDGE,"E2.6.10.2"),sQuery(id+"F0.wireOp",EDGE,"E2.6.10.3"),sQuery(id+"F0.wireOp",EDGE,"E2.6.11.0"),sQuery(id+"F0.wireOp",EDGE,"E2.6.11.1"),sQuery(id+"F0.wireOp",EDGE,"E2.6.11.2"),sQuery(id+"F0.wireOp",EDGE,"E2.6.11.3"),sQuery(id+"F0.wireOp",EDGE,"E2.6.12.0"),sQuery(id+"F0.wireOp",EDGE,"E2.6.12.1"),sQuery(id+"F0.wireOp",EDGE,"E2.6.12.2"),sQuery(id+"F0.wireOp",EDGE,"E2.6.12.3"),sQuery(id+"F0.wireOp",EDGE,"E2.6.13.0"),sQuery(id+"F0.wireOp",EDGE,"E2.6.13.1"),sQuery(id+"F0.wireOp",EDGE,"E2.6.13.2"),sQuery(id+"F0.wireOp",EDGE,"E2.6.13.3"),sQuery(id+"F0.wireOp",EDGE,"E2.6.14.0"),sQuery(id+"F0.wireOp",EDGE,"E2.6.14.1"),sQuery(id+"F0.wireOp",EDGE,"E2.6.14.2"),sQuery(id+"F0.wireOp",EDGE,"E2.6.14.3"),sQuery(id+"F0.wireOp",EDGE,"E2.6.15.0"),sQuery(id+"F0.wireOp",EDGE,"E2.6.15.1"),sQuery(id+"F0.wireOp",EDGE,"E2.6.15.2"),sQuery(id+"F0.wireOp",EDGE,"E2.6.15.3"),sQuery(id+"F0.wireOp",EDGE,"E2.6.16.0"),sQuery(id+"F0.wireOp",EDGE,"E2.6.16.1"),sQuery(id+"F0.wireOp",EDGE,"E2.6.16.2"),sQuery(id+"F0.wireOp",EDGE,"E2.6.16.3"),sQuery(id+"F0.wireOp",EDGE,"E2.6.17.0"),sQuery(id+"F0.wireOp",EDGE,"E2.6.17.1"),sQuery(id+"F0.wireOp",EDGE,"E2.6.17.2"),sQuery(id+"F0.wireOp",EDGE,"E2.6.17.3"),sQuery(id+"F0.wireOp",EDGE,"E2.6.18.0"),sQuery(id+"F0.wireOp",EDGE,"E2.6.18.1"),sQuery(id+"F0.wireOp",EDGE,"E2.6.18.2"),sQuery(id+"F0.wireOp",EDGE,"E2.6.18.3"),sQuery(id+"F0.wireOp",EDGE,"E2.6.19.0"),sQuery(id+"F0.wireOp",EDGE,"E2.6.19.1"),sQuery(id+"F0.wireOp",EDGE,"E2.6.19.2"),sQuery(id+"F0.wireOp",EDGE,"E2.6.19.3"),sQuery(id+"F0.wireOp",EDGE,"E2.6.20.0"),sQuery(id+"F0.wireOp",EDGE,"E2.6.20.1"),sQuery(id+"F0.wireOp",EDGE,"E2.6.20.2"),sQuery(id+"F0.wireOp",EDGE,"E2.6.20.3"),sQuery(id+"F0.wireOp",EDGE,"E2.6.21.0"),sQuery(id+"F0.wireOp",EDGE,"E2.6.21.1"),sQuery(id+"F0.wireOp",EDGE,"E2.6.21.2"),sQuery(id+"F0.wireOp",EDGE,"E2.6.21.3"),sQuery(id+"F0.wireOp",EDGE,"E2.6.22.0"),sQuery(id+"F0.wireOp",EDGE,"E2.6.22.1"),sQuery(id+"F0.wireOp",EDGE,"E2.6.22.2"),sQuery(id+"F0.wireOp",EDGE,"E2.6.22.3"),sQuery(id+"F0.wireOp",EDGE,"E2.6.23.0"),sQuery(id+"F0.wireOp",EDGE,"E2.6.23.1"),sQuery(id+"F0.wireOp",EDGE,"E2.6.23.2"),sQuery(id+"F0.wireOp",EDGE,"E2.6.23.3"),sQuery(id+"F0.wireOp",EDGE,"E2.6.24.0"),sQuery(id+"F0.wireOp",EDGE,"E2.6.24.1"),sQuery(id+"F0.wireOp",EDGE,"E2.6.24.2"),sQuery(id+"F0.wireOp",EDGE,"E2.6.24.3"),sQuery(id+"F0.wireOp",EDGE,"E2.6.25.0"),sQuery(id+"F0.wireOp",EDGE,"E2.6.25.1"),sQuery(id+"F0.wireOp",EDGE,"E2.6.25.2"),sQuery(id+"F0.wireOp",EDGE,"E2.6.25.3"),sQuery(id+"F0.wireOp",EDGE,"E2.6.26.0"),sQuery(id+"F0.wireOp",EDGE,"E2.6.26.1"),sQuery(id+"F0.wireOp",EDGE,"E2.6.26.2"),sQuery(id+"F0.wireOp",EDGE,"E2.6.26.3"),sQuery(id+"F0.wireOp",EDGE,"E2.6.27.0"),sQuery(id+"F0.wireOp",EDGE,"E2.6.27.1"),sQuery(id+"F0.wireOp",EDGE,"E2.6.27.2"),sQuery(id+"F0.wireOp",EDGE,"E2.6.27.3"),sQuery(id+"F0.wireOp",EDGE,"E2.6.28.0"),sQuery(id+"F0.wireOp",EDGE,"E2.6.28.1"),sQuery(id+"F0.wireOp",EDGE,"E2.6.28.2"),sQuery(id+"F0.wireOp",EDGE,"E2.6.28.3"),sQuery(id+"F0.wireOp",EDGE,"E2.6.29.0"),sQuery(id+"F0.wireOp",EDGE,"E2.6.29.1"),sQuery(id+"F0.wireOp",EDGE,"E2.6.29.2"),sQuery(id+"F0.wireOp",EDGE,"E2.6.29.3"),sQuery(id+"F0.wireOp",EDGE,"E2.6.30.1"),sQuery(id+"F0.wireOp",EDGE,"E2.6.30.2"),sQuery(id+"F0.wireOp",EDGE,"E2.6.30.3"),sQuery(id+"F0.wireOp",EDGE,"E2.7.0.0"),sQuery(id+"F0.wireOp",EDGE,"E2.7.0.1"),sQuery(id+"F0.wireOp",EDGE,"E2.7.0.2"),sQuery(id+"F0.wireOp",EDGE,"E2.7.0.3"),sQuery(id+"F0.wireOp",EDGE,"E2.7.1.0"),sQuery(id+"F0.wireOp",EDGE,"E2.7.1.1"),sQuery(id+"F0.wireOp",EDGE,"E2.7.1.2"),sQuery(id+"F0.wireOp",EDGE,"E2.7.1.3"),sQuery(id+"F0.wireOp",EDGE,"E2.7.2.0"),sQuery(id+"F0.wireOp",EDGE,"E2.7.2.1"),sQuery(id+"F0.wireOp",EDGE,"E2.7.2.2"),sQuery(id+"F0.wireOp",EDGE,"E2.7.2.3"),sQuery(id+"F0.wireOp",EDGE,"E2.7.3.0"),sQuery(id+"F0.wireOp",EDGE,"E2.7.3.1"),sQuery(id+"F0.wireOp",EDGE,"E2.7.3.2"),sQuery(id+"F0.wireOp",EDGE,"E2.7.3.3"),sQuery(id+"F0.wireOp",EDGE,"E2.7.4.0"),sQuery(id+"F0.wireOp",EDGE,"E2.7.4.1"),sQuery(id+"F0.wireOp",EDGE,"E2.7.4.2"),sQuery(id+"F0.wireOp",EDGE,"E2.7.4.3"),sQuery(id+"F0.wireOp",EDGE,"E2.7.5.0"),sQuery(id+"F0.wireOp",EDGE,"E2.7.5.1"),sQuery(id+"F0.wireOp",EDGE,"E2.7.5.2"),sQuery(id+"F0.wireOp",EDGE,"E2.7.5.3"),sQuery(id+"F0.wireOp",EDGE,"E2.7.6.0"),sQuery(id+"F0.wireOp",EDGE,"E2.7.6.1"),sQuery(id+"F0.wireOp",EDGE,"E2.7.6.2"),sQuery(id+"F0.wireOp",EDGE,"E2.7.6.3"),sQuery(id+"F0.wireOp",EDGE,"E2.7.7.0"),sQuery(id+"F0.wireOp",EDGE,"E2.7.7.1"),sQuery(id+"F0.wireOp",EDGE,"E2.7.7.2"),sQuery(id+"F0.wireOp",EDGE,"E2.7.7.3"),sQuery(id+"F0.wireOp",EDGE,"E2.7.8.0"),sQuery(id+"F0.wireOp",EDGE,"E2.7.8.1"),sQuery(id+"F0.wireOp",EDGE,"E2.7.8.2"),sQuery(id+"F0.wireOp",EDGE,"E2.7.8.3"),sQuery(id+"F0.wireOp",EDGE,"E2.7.9.0"),sQuery(id+"F0.wireOp",EDGE,"E2.7.9.1"),sQuery(id+"F0.wireOp",EDGE,"E2.7.9.2"),sQuery(id+"F0.wireOp",EDGE,"E2.7.9.3"),sQuery(id+"F0.wireOp",EDGE,"E2.7.10.0"),sQuery(id+"F0.wireOp",EDGE,"E2.7.10.1"),sQuery(id+"F0.wireOp",EDGE,"E2.7.10.2"),sQuery(id+"F0.wireOp",EDGE,"E2.7.10.3"),sQuery(id+"F0.wireOp",EDGE,"E2.7.11.0"),sQuery(id+"F0.wireOp",EDGE,"E2.7.11.1"),sQuery(id+"F0.wireOp",EDGE,"E2.7.11.2"),sQuery(id+"F0.wireOp",EDGE,"E2.7.11.3"),sQuery(id+"F0.wireOp",EDGE,"E2.7.12.0"),sQuery(id+"F0.wireOp",EDGE,"E2.7.12.1"),sQuery(id+"F0.wireOp",EDGE,"E2.7.12.2"),sQuery(id+"F0.wireOp",EDGE,"E2.7.12.3"),sQuery(id+"F0.wireOp",EDGE,"E2.7.13.0"),sQuery(id+"F0.wireOp",EDGE,"E2.7.13.1"),sQuery(id+"F0.wireOp",EDGE,"E2.7.13.2"),sQuery(id+"F0.wireOp",EDGE,"E2.7.13.3"),sQuery(id+"F0.wireOp",EDGE,"E2.7.14.0"),sQuery(id+"F0.wireOp",EDGE,"E2.7.14.1"),sQuery(id+"F0.wireOp",EDGE,"E2.7.14.2"),sQuery(id+"F0.wireOp",EDGE,"E2.7.14.3"),sQuery(id+"F0.wireOp",EDGE,"E2.7.15.0"),sQuery(id+"F0.wireOp",EDGE,"E2.7.15.1"),sQuery(id+"F0.wireOp",EDGE,"E2.7.15.2"),sQuery(id+"F0.wireOp",EDGE,"E2.7.15.3"),sQuery(id+"F0.wireOp",EDGE,"E2.7.16.0"),sQuery(id+"F0.wireOp",EDGE,"E2.7.16.1"),sQuery(id+"F0.wireOp",EDGE,"E2.7.16.2"),sQuery(id+"F0.wireOp",EDGE,"E2.7.16.3"),sQuery(id+"F0.wireOp",EDGE,"E2.7.17.0"),sQuery(id+"F0.wireOp",EDGE,"E2.7.17.1"),sQuery(id+"F0.wireOp",EDGE,"E2.7.17.2"),sQuery(id+"F0.wireOp",EDGE,"E2.7.17.3"),sQuery(id+"F0.wireOp",EDGE,"E2.7.18.0"),sQuery(id+"F0.wireOp",EDGE,"E2.7.18.1"),sQuery(id+"F0.wireOp",EDGE,"E2.7.18.2"),sQuery(id+"F0.wireOp",EDGE,"E2.7.18.3"),sQuery(id+"F0.wireOp",EDGE,"E2.7.19.0"),sQuery(id+"F0.wireOp",EDGE,"E2.7.19.1"),sQuery(id+"F0.wireOp",EDGE,"E2.7.19.2"),sQuery(id+"F0.wireOp",EDGE,"E2.7.19.3"),sQuery(id+"F0.wireOp",EDGE,"E2.7.20.0"),sQuery(id+"F0.wireOp",EDGE,"E2.7.20.1"),sQuery(id+"F0.wireOp",EDGE,"E2.7.20.2"),sQuery(id+"F0.wireOp",EDGE,"E2.7.20.3"),sQuery(id+"F0.wireOp",EDGE,"E2.7.21.0"),sQuery(id+"F0.wireOp",EDGE,"E2.7.21.1"),sQuery(id+"F0.wireOp",EDGE,"E2.7.21.2"),sQuery(id+"F0.wireOp",EDGE,"E2.7.21.3"),sQuery(id+"F0.wireOp",EDGE,"E2.7.22.0"),sQuery(id+"F0.wireOp",EDGE,"E2.7.22.1"),sQuery(id+"F0.wireOp",EDGE,"E2.7.22.2"),sQuery(id+"F0.wireOp",EDGE,"E2.7.22.3"),sQuery(id+"F0.wireOp",EDGE,"E2.7.23.0"),sQuery(id+"F0.wireOp",EDGE,"E2.7.23.1"),sQuery(id+"F0.wireOp",EDGE,"E2.7.23.2"),sQuery(id+"F0.wireOp",EDGE,"E2.7.23.3"),sQuery(id+"F0.wireOp",EDGE,"E2.7.24.0"),sQuery(id+"F0.wireOp",EDGE,"E2.7.24.1"),sQuery(id+"F0.wireOp",EDGE,"E2.7.24.2"),sQuery(id+"F0.wireOp",EDGE,"E2.7.24.3"),sQuery(id+"F0.wireOp",EDGE,"E2.7.25.0"),sQuery(id+"F0.wireOp",EDGE,"E2.7.25.1"),sQuery(id+"F0.wireOp",EDGE,"E2.7.25.2"),sQuery(id+"F0.wireOp",EDGE,"E2.7.25.3"),sQuery(id+"F0.wireOp",EDGE,"E2.7.26.0"),sQuery(id+"F0.wireOp",EDGE,"E2.7.26.1"),sQuery(id+"F0.wireOp",EDGE,"E2.7.26.2"),sQuery(id+"F0.wireOp",EDGE,"E2.7.26.3"),sQuery(id+"F0.wireOp",EDGE,"E2.7.27.0"),sQuery(id+"F0.wireOp",EDGE,"E2.7.27.1"),sQuery(id+"F0.wireOp",EDGE,"E2.7.27.2"),sQuery(id+"F0.wireOp",EDGE,"E2.7.27.3"),sQuery(id+"F0.wireOp",EDGE,"E2.7.28.0"),sQuery(id+"F0.wireOp",EDGE,"E2.7.28.1"),sQuery(id+"F0.wireOp",EDGE,"E2.7.28.2"),sQuery(id+"F0.wireOp",EDGE,"E2.7.28.3"),sQuery(id+"F0.wireOp",EDGE,"E2.7.29.0"),sQuery(id+"F0.wireOp",EDGE,"E2.7.29.1"),sQuery(id+"F0.wireOp",EDGE,"E2.7.29.2"),sQuery(id+"F0.wireOp",EDGE,"E2.7.29.3"),sQuery(id+"F0.wireOp",EDGE,"E2.7.30.1"),sQuery(id+"F0.wireOp",EDGE,"E2.7.30.2"),sQuery(id+"F0.wireOp",EDGE,"E2.7.30.3"),sQuery(id+"F0.wireOp",EDGE,"E2.8.0.0"),sQuery(id+"F0.wireOp",EDGE,"E2.8.0.1"),sQuery(id+"F0.wireOp",EDGE,"E2.8.0.2"),sQuery(id+"F0.wireOp",EDGE,"E2.8.0.3"),sQuery(id+"F0.wireOp",EDGE,"E2.8.1.0"),sQuery(id+"F0.wireOp",EDGE,"E2.8.1.1"),sQuery(id+"F0.wireOp",EDGE,"E2.8.1.2"),sQuery(id+"F0.wireOp",EDGE,"E2.8.1.3"),sQuery(id+"F0.wireOp",EDGE,"E2.8.2.0"),sQuery(id+"F0.wireOp",EDGE,"E2.8.2.1"),sQuery(id+"F0.wireOp",EDGE,"E2.8.2.2"),sQuery(id+"F0.wireOp",EDGE,"E2.8.2.3"),sQuery(id+"F0.wireOp",EDGE,"E2.8.3.0"),sQuery(id+"F0.wireOp",EDGE,"E2.8.3.1"),sQuery(id+"F0.wireOp",EDGE,"E2.8.3.2"),sQuery(id+"F0.wireOp",EDGE,"E2.8.3.3"),sQuery(id+"F0.wireOp",EDGE,"E2.8.4.0"),sQuery(id+"F0.wireOp",EDGE,"E2.8.4.1"),sQuery(id+"F0.wireOp",EDGE,"E2.8.4.2"),sQuery(id+"F0.wireOp",EDGE,"E2.8.4.3"),sQuery(id+"F0.wireOp",EDGE,"E2.8.5.0"),sQuery(id+"F0.wireOp",EDGE,"E2.8.5.1"),sQuery(id+"F0.wireOp",EDGE,"E2.8.5.2"),sQuery(id+"F0.wireOp",EDGE,"E2.8.5.3"),sQuery(id+"F0.wireOp",EDGE,"E2.8.6.0"),sQuery(id+"F0.wireOp",EDGE,"E2.8.6.1"),sQuery(id+"F0.wireOp",EDGE,"E2.8.6.2"),sQuery(id+"F0.wireOp",EDGE,"E2.8.6.3"),sQuery(id+"F0.wireOp",EDGE,"E2.8.7.0"),sQuery(id+"F0.wireOp",EDGE,"E2.8.7.1"),sQuery(id+"F0.wireOp",EDGE,"E2.8.7.2"),sQuery(id+"F0.wireOp",EDGE,"E2.8.7.3"),sQuery(id+"F0.wireOp",EDGE,"E2.8.8.0"),sQuery(id+"F0.wireOp",EDGE,"E2.8.8.1"),sQuery(id+"F0.wireOp",EDGE,"E2.8.8.2"),sQuery(id+"F0.wireOp",EDGE,"E2.8.8.3"),sQuery(id+"F0.wireOp",EDGE,"E2.8.9.0"),sQuery(id+"F0.wireOp",EDGE,"E2.8.9.1"),sQuery(id+"F0.wireOp",EDGE,"E2.8.9.2"),sQuery(id+"F0.wireOp",EDGE,"E2.8.9.3"),sQuery(id+"F0.wireOp",EDGE,"E2.8.10.0"),sQuery(id+"F0.wireOp",EDGE,"E2.8.10.1"),sQuery(id+"F0.wireOp",EDGE,"E2.8.10.2"),sQuery(id+"F0.wireOp",EDGE,"E2.8.10.3"),sQuery(id+"F0.wireOp",EDGE,"E2.8.11.0"),sQuery(id+"F0.wireOp",EDGE,"E2.8.11.1"),sQuery(id+"F0.wireOp",EDGE,"E2.8.11.2"),sQuery(id+"F0.wireOp",EDGE,"E2.8.11.3"),sQuery(id+"F0.wireOp",EDGE,"E2.8.12.0"),sQuery(id+"F0.wireOp",EDGE,"E2.8.12.1"),sQuery(id+"F0.wireOp",EDGE,"E2.8.12.2"),sQuery(id+"F0.wireOp",EDGE,"E2.8.12.3"),sQuery(id+"F0.wireOp",EDGE,"E2.8.13.0"),sQuery(id+"F0.wireOp",EDGE,"E2.8.13.1"),sQuery(id+"F0.wireOp",EDGE,"E2.8.13.2"),sQuery(id+"F0.wireOp",EDGE,"E2.8.13.3"),sQuery(id+"F0.wireOp",EDGE,"E2.8.14.0"),sQuery(id+"F0.wireOp",EDGE,"E2.8.14.1"),sQuery(id+"F0.wireOp",EDGE,"E2.8.14.2"),sQuery(id+"F0.wireOp",EDGE,"E2.8.14.3"),sQuery(id+"F0.wireOp",EDGE,"E2.8.15.0"),sQuery(id+"F0.wireOp",EDGE,"E2.8.15.1"),sQuery(id+"F0.wireOp",EDGE,"E2.8.15.2"),sQuery(id+"F0.wireOp",EDGE,"E2.8.15.3"),sQuery(id+"F0.wireOp",EDGE,"E2.8.16.0"),sQuery(id+"F0.wireOp",EDGE,"E2.8.16.1"),sQuery(id+"F0.wireOp",EDGE,"E2.8.16.2"),sQuery(id+"F0.wireOp",EDGE,"E2.8.16.3"),sQuery(id+"F0.wireOp",EDGE,"E2.8.17.0"),sQuery(id+"F0.wireOp",EDGE,"E2.8.17.1"),sQuery(id+"F0.wireOp",EDGE,"E2.8.17.2"),sQuery(id+"F0.wireOp",EDGE,"E2.8.17.3"),sQuery(id+"F0.wireOp",EDGE,"E2.8.18.0"),sQuery(id+"F0.wireOp",EDGE,"E2.8.18.1"),sQuery(id+"F0.wireOp",EDGE,"E2.8.18.2"),sQuery(id+"F0.wireOp",EDGE,"E2.8.18.3"),sQuery(id+"F0.wireOp",EDGE,"E2.8.19.0"),sQuery(id+"F0.wireOp",EDGE,"E2.8.19.1"),sQuery(id+"F0.wireOp",EDGE,"E2.8.19.2"),sQuery(id+"F0.wireOp",EDGE,"E2.8.19.3"),sQuery(id+"F0.wireOp",EDGE,"E2.8.20.0"),sQuery(id+"F0.wireOp",EDGE,"E2.8.20.1"),sQuery(id+"F0.wireOp",EDGE,"E2.8.20.2"),sQuery(id+"F0.wireOp",EDGE,"E2.8.20.3"),sQuery(id+"F0.wireOp",EDGE,"E2.8.21.0"),sQuery(id+"F0.wireOp",EDGE,"E2.8.21.1"),sQuery(id+"F0.wireOp",EDGE,"E2.8.21.2"),sQuery(id+"F0.wireOp",EDGE,"E2.8.21.3"),sQuery(id+"F0.wireOp",EDGE,"E2.8.22.0"),sQuery(id+"F0.wireOp",EDGE,"E2.8.22.1"),sQuery(id+"F0.wireOp",EDGE,"E2.8.22.2"),sQuery(id+"F0.wireOp",EDGE,"E2.8.22.3"),sQuery(id+"F0.wireOp",EDGE,"E2.8.23.0"),sQuery(id+"F0.wireOp",EDGE,"E2.8.23.1"),sQuery(id+"F0.wireOp",EDGE,"E2.8.23.2"),sQuery(id+"F0.wireOp",EDGE,"E2.8.23.3"),sQuery(id+"F0.wireOp",EDGE,"E2.8.24.0"),sQuery(id+"F0.wireOp",EDGE,"E2.8.24.1"),sQuery(id+"F0.wireOp",EDGE,"E2.8.24.2"),sQuery(id+"F0.wireOp",EDGE,"E2.8.24.3"),sQuery(id+"F0.wireOp",EDGE,"E2.8.25.0"),sQuery(id+"F0.wireOp",EDGE,"E2.8.25.1"),sQuery(id+"F0.wireOp",EDGE,"E2.8.25.2"),sQuery(id+"F0.wireOp",EDGE,"E2.8.25.3"),sQuery(id+"F0.wireOp",EDGE,"E2.8.26.0"),sQuery(id+"F0.wireOp",EDGE,"E2.8.26.1"),sQuery(id+"F0.wireOp",EDGE,"E2.8.26.2"),sQuery(id+"F0.wireOp",EDGE,"E2.8.26.3"),sQuery(id+"F0.wireOp",EDGE,"E2.8.27.0"),sQuery(id+"F0.wireOp",EDGE,"E2.8.27.1"),sQuery(id+"F0.wireOp",EDGE,"E2.8.27.2"),sQuery(id+"F0.wireOp",EDGE,"E2.8.27.3"),sQuery(id+"F0.wireOp",EDGE,"E2.8.28.0"),sQuery(id+"F0.wireOp",EDGE,"E2.8.28.1"),sQuery(id+"F0.wireOp",EDGE,"E2.8.28.2"),sQuery(id+"F0.wireOp",EDGE,"E2.8.28.3"),sQuery(id+"F0.wireOp",EDGE,"E2.8.29.0"),sQuery(id+"F0.wireOp",EDGE,"E2.8.29.1"),sQuery(id+"F0.wireOp",EDGE,"E2.8.29.2"),sQuery(id+"F0.wireOp",EDGE,"E2.8.29.3"),sQuery(id+"F0.wireOp",EDGE,"E2.8.30.1"),sQuery(id+"F0.wireOp",EDGE,"E2.8.30.2"),sQuery(id+"F0.wireOp",EDGE,"E2.8.30.3"),sQuery(id+"F0.wireOp",EDGE,"E2.9.0.0"),sQuery(id+"F0.wireOp",EDGE,"E2.9.0.1"),sQuery(id+"F0.wireOp",EDGE,"E2.9.0.2"),sQuery(id+"F0.wireOp",EDGE,"E2.9.0.3"),sQuery(id+"F0.wireOp",EDGE,"E2.9.1.0"),sQuery(id+"F0.wireOp",EDGE,"E2.9.1.1"),sQuery(id+"F0.wireOp",EDGE,"E2.9.1.2"),sQuery(id+"F0.wireOp",EDGE,"E2.9.1.3"),sQuery(id+"F0.wireOp",EDGE,"E2.9.2.0"),sQuery(id+"F0.wireOp",EDGE,"E2.9.2.1"),sQuery(id+"F0.wireOp",EDGE,"E2.9.2.2"),sQuery(id+"F0.wireOp",EDGE,"E2.9.2.3"),sQuery(id+"F0.wireOp",EDGE,"E2.9.3.0"),sQuery(id+"F0.wireOp",EDGE,"E2.9.3.1"),sQuery(id+"F0.wireOp",EDGE,"E2.9.3.2"),sQuery(id+"F0.wireOp",EDGE,"E2.9.3.3"),sQuery(id+"F0.wireOp",EDGE,"E2.9.4.0"),sQuery(id+"F0.wireOp",EDGE,"E2.9.4.1"),sQuery(id+"F0.wireOp",EDGE,"E2.9.4.2"),sQuery(id+"F0.wireOp",EDGE,"E2.9.4.3"),sQuery(id+"F0.wireOp",EDGE,"E2.9.5.0"),sQuery(id+"F0.wireOp",EDGE,"E2.9.5.1"),sQuery(id+"F0.wireOp",EDGE,"E2.9.5.2"),sQuery(id+"F0.wireOp",EDGE,"E2.9.5.3"),sQuery(id+"F0.wireOp",EDGE,"E2.9.6.0"),sQuery(id+"F0.wireOp",EDGE,"E2.9.6.1"),sQuery(id+"F0.wireOp",EDGE,"E2.9.6.2"),sQuery(id+"F0.wireOp",EDGE,"E2.9.6.3"),sQuery(id+"F0.wireOp",EDGE,"E2.9.7.0"),sQuery(id+"F0.wireOp",EDGE,"E2.9.7.1"),sQuery(id+"F0.wireOp",EDGE,"E2.9.7.2"),sQuery(id+"F0.wireOp",EDGE,"E2.9.7.3"),sQuery(id+"F0.wireOp",EDGE,"E2.9.8.0"),sQuery(id+"F0.wireOp",EDGE,"E2.9.8.1"),sQuery(id+"F0.wireOp",EDGE,"E2.9.8.2"),sQuery(id+"F0.wireOp",EDGE,"E2.9.8.3"),sQuery(id+"F0.wireOp",EDGE,"E2.9.9.0"),sQuery(id+"F0.wireOp",EDGE,"E2.9.9.1"),sQuery(id+"F0.wireOp",EDGE,"E2.9.9.2"),sQuery(id+"F0.wireOp",EDGE,"E2.9.9.3"),sQuery(id+"F0.wireOp",EDGE,"E2.9.10.0"),sQuery(id+"F0.wireOp",EDGE,"E2.9.10.1"),sQuery(id+"F0.wireOp",EDGE,"E2.9.10.2"),sQuery(id+"F0.wireOp",EDGE,"E2.9.10.3"),sQuery(id+"F0.wireOp",EDGE,"E2.9.11.0"),sQuery(id+"F0.wireOp",EDGE,"E2.9.11.1"),sQuery(id+"F0.wireOp",EDGE,"E2.9.11.2"),sQuery(id+"F0.wireOp",EDGE,"E2.9.11.3"),sQuery(id+"F0.wireOp",EDGE,"E2.9.12.0"),sQuery(id+"F0.wireOp",EDGE,"E2.9.12.1"),sQuery(id+"F0.wireOp",EDGE,"E2.9.12.2"),sQuery(id+"F0.wireOp",EDGE,"E2.9.12.3"),sQuery(id+"F0.wireOp",EDGE,"E2.9.13.0"),sQuery(id+"F0.wireOp",EDGE,"E2.9.13.1"),sQuery(id+"F0.wireOp",EDGE,"E2.9.13.2"),sQuery(id+"F0.wireOp",EDGE,"E2.9.13.3"),sQuery(id+"F0.wireOp",EDGE,"E2.9.14.0"),sQuery(id+"F0.wireOp",EDGE,"E2.9.14.1"),sQuery(id+"F0.wireOp",EDGE,"E2.9.14.2"),sQuery(id+"F0.wireOp",EDGE,"E2.9.14.3"),sQuery(id+"F0.wireOp",EDGE,"E2.9.15.0"),sQuery(id+"F0.wireOp",EDGE,"E2.9.15.1"),sQuery(id+"F0.wireOp",EDGE,"E2.9.15.2"),sQuery(id+"F0.wireOp",EDGE,"E2.9.15.3"),sQuery(id+"F0.wireOp",EDGE,"E2.9.16.0"),sQuery(id+"F0.wireOp",EDGE,"E2.9.16.1"),sQuery(id+"F0.wireOp",EDGE,"E2.9.16.2"),sQuery(id+"F0.wireOp",EDGE,"E2.9.16.3"),sQuery(id+"F0.wireOp",EDGE,"E2.9.17.0"),sQuery(id+"F0.wireOp",EDGE,"E2.9.17.1"),sQuery(id+"F0.wireOp",EDGE,"E2.9.17.2"),sQuery(id+"F0.wireOp",EDGE,"E2.9.17.3"),sQuery(id+"F0.wireOp",EDGE,"E2.9.18.0"),sQuery(id+"F0.wireOp",EDGE,"E2.9.18.1"),sQuery(id+"F0.wireOp",EDGE,"E2.9.18.2"),sQuery(id+"F0.wireOp",EDGE,"E2.9.18.3"),sQuery(id+"F0.wireOp",EDGE,"E2.9.19.0"),sQuery(id+"F0.wireOp",EDGE,"E2.9.19.1"),sQuery(id+"F0.wireOp",EDGE,"E2.9.19.2"),sQuery(id+"F0.wireOp",EDGE,"E2.9.19.3"),sQuery(id+"F0.wireOp",EDGE,"E2.9.20.0"),sQuery(id+"F0.wireOp",EDGE,"E2.9.20.1"),sQuery(id+"F0.wireOp",EDGE,"E2.9.20.2"),sQuery(id+"F0.wireOp",EDGE,"E2.9.20.3"),sQuery(id+"F0.wireOp",EDGE,"E2.9.21.0"),sQuery(id+"F0.wireOp",EDGE,"E2.9.21.1"),sQuery(id+"F0.wireOp",EDGE,"E2.9.21.2"),sQuery(id+"F0.wireOp",EDGE,"E2.9.21.3"),sQuery(id+"F0.wireOp",EDGE,"E2.9.22.0"),sQuery(id+"F0.wireOp",EDGE,"E2.9.22.1"),sQuery(id+"F0.wireOp",EDGE,"E2.9.22.2"),sQuery(id+"F0.wireOp",EDGE,"E2.9.22.3"),sQuery(id+"F0.wireOp",EDGE,"E2.9.23.0"),sQuery(id+"F0.wireOp",EDGE,"E2.9.23.1"),sQuery(id+"F0.wireOp",EDGE,"E2.9.23.2"),sQuery(id+"F0.wireOp",EDGE,"E2.9.23.3"),sQuery(id+"F0.wireOp",EDGE,"E2.9.24.0"),sQuery(id+"F0.wireOp",EDGE,"E2.9.24.1"),sQuery(id+"F0.wireOp",EDGE,"E2.9.24.2"),sQuery(id+"F0.wireOp",EDGE,"E2.9.24.3"),sQuery(id+"F0.wireOp",EDGE,"E2.9.25.0"),sQuery(id+"F0.wireOp",EDGE,"E2.9.25.1"),sQuery(id+"F0.wireOp",EDGE,"E2.9.25.2"),sQuery(id+"F0.wireOp",EDGE,"E2.9.25.3"),sQuery(id+"F0.wireOp",EDGE,"E2.9.26.0"),sQuery(id+"F0.wireOp",EDGE,"E2.9.26.1"),sQuery(id+"F0.wireOp",EDGE,"E2.9.26.2"),sQuery(id+"F0.wireOp",EDGE,"E2.9.26.3"),sQuery(id+"F0.wireOp",EDGE,"E2.9.27.0"),sQuery(id+"F0.wireOp",EDGE,"E2.9.27.1"),sQuery(id+"F0.wireOp",EDGE,"E2.9.27.2"),sQuery(id+"F0.wireOp",EDGE,"E2.9.27.3"),sQuery(id+"F0.wireOp",EDGE,"E2.9.28.0"),sQuery(id+"F0.wireOp",EDGE,"E2.9.28.1"),sQuery(id+"F0.wireOp",EDGE,"E2.9.28.2"),sQuery(id+"F0.wireOp",EDGE,"E2.9.28.3"),sQuery(id+"F0.wireOp",EDGE,"E2.9.29.0"),sQuery(id+"F0.wireOp",EDGE,"E2.9.29.1"),sQuery(id+"F0.wireOp",EDGE,"E2.9.29.2"),sQuery(id+"F0.wireOp",EDGE,"E2.9.29.3"),sQuery(id+"F0.wireOp",EDGE,"E2.9.30.1"),sQuery(id+"F0.wireOp",EDGE,"E2.9.30.2"),sQuery(id+"F0.wireOp",EDGE,"E2.9.30.3"),sQuery(id+"F0.wireOp",EDGE,"E2.10.0.0"),sQuery(id+"F0.wireOp",EDGE,"E2.10.0.2"),sQuery(id+"F0.wireOp",EDGE,"E2.10.0.3"),sQuery(id+"F0.wireOp",EDGE,"E2.10.1.0"),sQuery(id+"F0.wireOp",EDGE,"E2.10.1.2"),sQuery(id+"F0.wireOp",EDGE,"E2.10.1.3"),sQuery(id+"F0.wireOp",EDGE,"E2.10.2.0"),sQuery(id+"F0.wireOp",EDGE,"E2.10.2.2"),sQuery(id+"F0.wireOp",EDGE,"E2.10.2.3"),sQuery(id+"F0.wireOp",EDGE,"E2.10.3.0"),sQuery(id+"F0.wireOp",EDGE,"E2.10.3.2"),sQuery(id+"F0.wireOp",EDGE,"E2.10.3.3"),sQuery(id+"F0.wireOp",EDGE,"E2.10.4.0"),sQuery(id+"F0.wireOp",EDGE,"E2.10.4.2"),sQuery(id+"F0.wireOp",EDGE,"E2.10.4.3"),sQuery(id+"F0.wireOp",EDGE,"E2.10.5.0"),sQuery(id+"F0.wireOp",EDGE,"E2.10.5.2"),sQuery(id+"F0.wireOp",EDGE,"E2.10.5.3"),sQuery(id+"F0.wireOp",EDGE,"E2.10.6.0"),sQuery(id+"F0.wireOp",EDGE,"E2.10.6.2"),sQuery(id+"F0.wireOp",EDGE,"E2.10.6.3"),sQuery(id+"F0.wireOp",EDGE,"E2.10.7.0"),sQuery(id+"F0.wireOp",EDGE,"E2.10.7.2"),sQuery(id+"F0.wireOp",EDGE,"E2.10.7.3"),sQuery(id+"F0.wireOp",EDGE,"E2.10.8.0"),sQuery(id+"F0.wireOp",EDGE,"E2.10.8.2"),sQuery(id+"F0.wireOp",EDGE,"E2.10.8.3"),sQuery(id+"F0.wireOp",EDGE,"E2.10.9.0"),sQuery(id+"F0.wireOp",EDGE,"E2.10.9.2"),sQuery(id+"F0.wireOp",EDGE,"E2.10.9.3"),sQuery(id+"F0.wireOp",EDGE,"E2.10.10.0"),sQuery(id+"F0.wireOp",EDGE,"E2.10.10.2"),sQuery(id+"F0.wireOp",EDGE,"E2.10.10.3"),sQuery(id+"F0.wireOp",EDGE,"E2.10.11.0"),sQuery(id+"F0.wireOp",EDGE,"E2.10.11.2"),sQuery(id+"F0.wireOp",EDGE,"E2.10.11.3"),sQuery(id+"F0.wireOp",EDGE,"E2.10.12.0"),sQuery(id+"F0.wireOp",EDGE,"E2.10.12.2"),sQuery(id+"F0.wireOp",EDGE,"E2.10.12.3"),sQuery(id+"F0.wireOp",EDGE,"E2.10.13.0"),sQuery(id+"F0.wireOp",EDGE,"E2.10.13.2"),sQuery(id+"F0.wireOp",EDGE,"E2.10.13.3"),sQuery(id+"F0.wireOp",EDGE,"E2.10.14.0"),sQuery(id+"F0.wireOp",EDGE,"E2.10.14.2"),sQuery(id+"F0.wireOp",EDGE,"E2.10.14.3"),sQuery(id+"F0.wireOp",EDGE,"E2.10.15.0"),sQuery(id+"F0.wireOp",EDGE,"E2.10.15.2"),sQuery(id+"F0.wireOp",EDGE,"E2.10.15.3"),sQuery(id+"F0.wireOp",EDGE,"E2.10.16.0"),sQuery(id+"F0.wireOp",EDGE,"E2.10.16.2"),sQuery(id+"F0.wireOp",EDGE,"E2.10.16.3"),sQuery(id+"F0.wireOp",EDGE,"E2.10.17.0"),sQuery(id+"F0.wireOp",EDGE,"E2.10.17.2"),sQuery(id+"F0.wireOp",EDGE,"E2.10.17.3"),sQuery(id+"F0.wireOp",EDGE,"E2.10.18.0"),sQuery(id+"F0.wireOp",EDGE,"E2.10.18.2"),sQuery(id+"F0.wireOp",EDGE,"E2.10.18.3"),sQuery(id+"F0.wireOp",EDGE,"E2.10.19.0"),sQuery(id+"F0.wireOp",EDGE,"E2.10.19.2"),sQuery(id+"F0.wireOp",EDGE,"E2.10.19.3"),sQuery(id+"F0.wireOp",EDGE,"E2.10.20.0"),sQuery(id+"F0.wireOp",EDGE,"E2.10.20.2"),sQuery(id+"F0.wireOp",EDGE,"E2.10.20.3"),sQuery(id+"F0.wireOp",EDGE,"E2.10.21.0"),sQuery(id+"F0.wireOp",EDGE,"E2.10.21.2"),sQuery(id+"F0.wireOp",EDGE,"E2.10.21.3"),sQuery(id+"F0.wireOp",EDGE,"E2.10.22.0"),sQuery(id+"F0.wireOp",EDGE,"E2.10.22.2"),sQuery(id+"F0.wireOp",EDGE,"E2.10.22.3"),sQuery(id+"F0.wireOp",EDGE,"E2.10.23.0"),sQuery(id+"F0.wireOp",EDGE,"E2.10.23.2"),sQuery(id+"F0.wireOp",EDGE,"E2.10.23.3"),sQuery(id+"F0.wireOp",EDGE,"E2.10.24.0"),sQuery(id+"F0.wireOp",EDGE,"E2.10.24.2"),sQuery(id+"F0.wireOp",EDGE,"E2.10.24.3"),sQuery(id+"F0.wireOp",EDGE,"E2.10.25.0"),sQuery(id+"F0.wireOp",EDGE,"E2.10.25.2"),sQuery(id+"F0.wireOp",EDGE,"E2.10.25.3"),sQuery(id+"F0.wireOp",EDGE,"E2.10.26.0"),sQuery(id+"F0.wireOp",EDGE,"E2.10.26.2"),sQuery(id+"F0.wireOp",EDGE,"E2.10.26.3"),sQuery(id+"F0.wireOp",EDGE,"E2.10.27.0"),sQuery(id+"F0.wireOp",EDGE,"E2.10.27.2"),sQuery(id+"F0.wireOp",EDGE,"E2.10.27.3"),sQuery(id+"F0.wireOp",EDGE,"E2.10.28.0"),sQuery(id+"F0.wireOp",EDGE,"E2.10.28.2"),sQuery(id+"F0.wireOp",EDGE,"E2.10.28.3"),sQuery(id+"F0.wireOp",EDGE,"E2.10.29.0"),sQuery(id+"F0.wireOp",EDGE,"E2.10.29.2"),sQuery(id+"F0.wireOp",EDGE,"E2.10.29.3"),sQuery(id+"F0.wireOp",EDGE,"E2.10.30.2"),sQuery(id+"F0.wireOp",EDGE,"E2.10.30.3")])]});
            transform(context, id + "F2", {"entities" : qUnion([Q0]), "transformType" : TransformType.TRANSLATION_3D, "dx" : 0 * mm, "dy" : 0 * mm, "dz" : 0 * mm, "makeCopy" : true});
        }
    });
